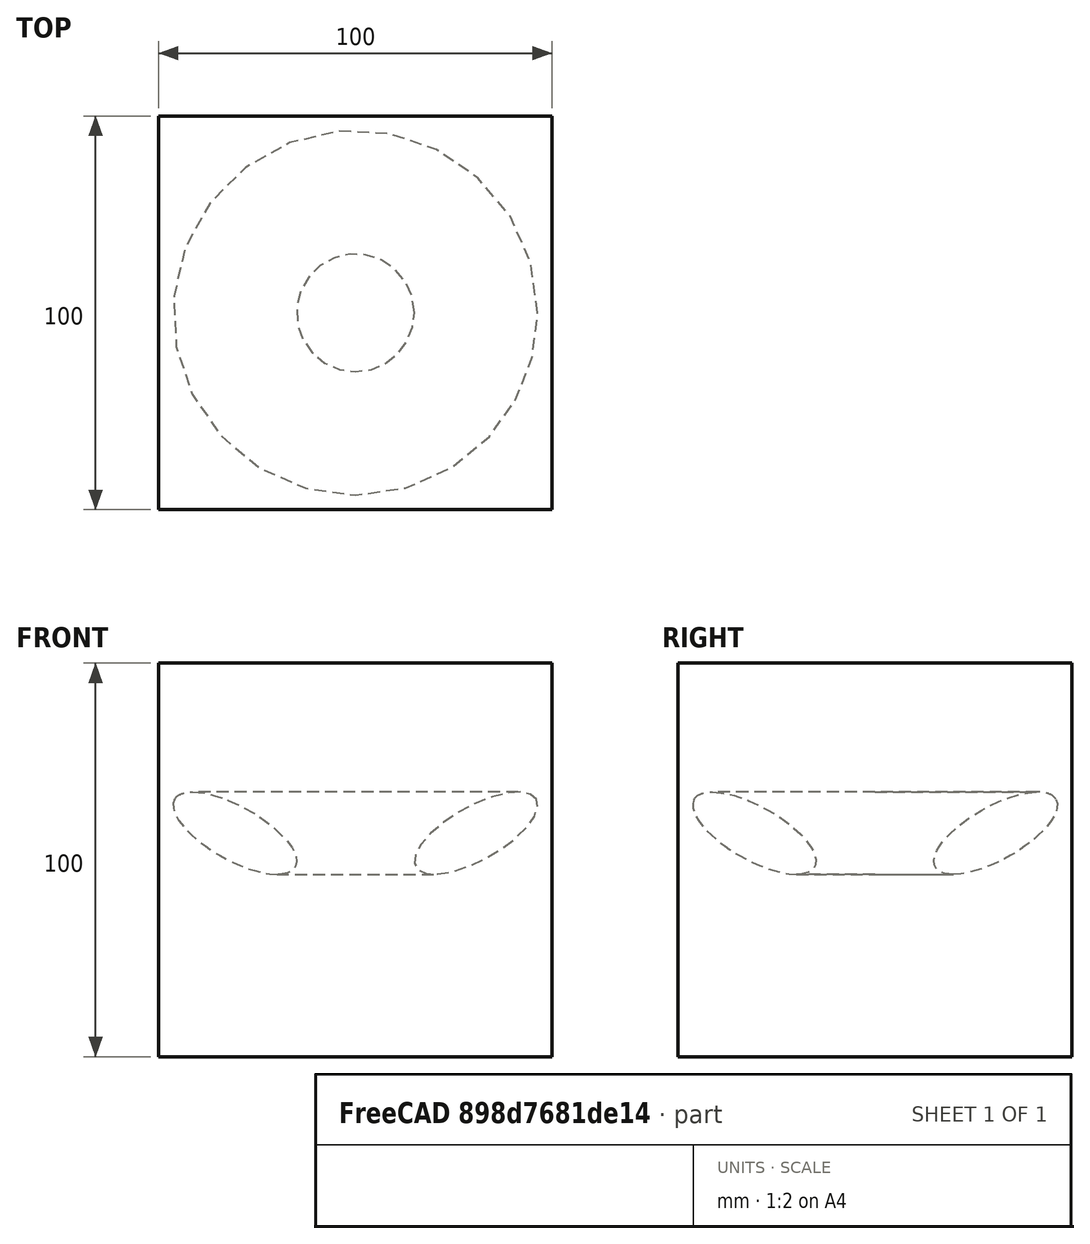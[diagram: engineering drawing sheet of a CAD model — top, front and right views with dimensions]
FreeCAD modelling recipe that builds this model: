
FCSTD DOCUMENT  (FreeCAD 1.0R39109 (Git))
Label: revolveSingleEdge
License: All rights reserved
LicenseURL: http://en.wikipedia.org/wiki/All_rights_reserved
objects: App::DocumentObjectGroupPython×1248, App::Part×2, Part::FeaturePython×1, Sketcher::SketchObject×1, Part::Revolution×1
note: 4 computed .brp shape members not serialized (recipe doc carries the construction recipe); baked Part::Feature solids carry a one-line shape summary decoded from their .brp

FEATURE [App::DocumentObjectGroupPython] HALFPI  # scripted group (container) (typed FeaturePython)
  name = HALFPI
  value = pi/2.
FEATURE [App::DocumentObjectGroupPython] PI  # scripted group (container) (typed FeaturePython)
  name = PI
  value = 1.*pi
FEATURE [App::DocumentObjectGroupPython] TWOPI  # scripted group (container) (typed FeaturePython)
  name = TWOPI
  value = 2.*pi
FEATURE [App::DocumentObjectGroupPython] Constants  # scripted group (container) (typed FeaturePython)
  Group = -> [HALFPI,PI,TWOPI]
FEATURE [App::DocumentObjectGroupPython] Variables  # scripted group (container) (typed FeaturePython)
FEATURE [App::DocumentObjectGroupPython] Quantities  # scripted group (container) (typed FeaturePython)
FEATURE [App::DocumentObjectGroupPython] Isotopes  # scripted group (container) (typed FeaturePython)
FEATURE [App::DocumentObjectGroupPython] Elements  # scripted group (container) (typed FeaturePython)
FEATURE [App::DocumentObjectGroupPython] G4Isotopes  # scripted group (container) (typed FeaturePython)
FEATURE [App::DocumentObjectGroupPython] H_element  # scripted group (container) (typed FeaturePython)
  Z = 1
  atom_value = 1.008
  formula = H
  name = H_element
FEATURE [App::DocumentObjectGroupPython] He_element  # scripted group (container) (typed FeaturePython)
  Z = 2
  atom_value = 4.0026
  formula = He
  name = He_element
FEATURE [App::DocumentObjectGroupPython] Li_element  # scripted group (container) (typed FeaturePython)
  Z = 3
  atom_value = 6.94
  formula = Li
  name = Li_element
FEATURE [App::DocumentObjectGroupPython] Be_element  # scripted group (container) (typed FeaturePython)
  Z = 4
  atom_value = 9.01218
  formula = Be
  name = Be_element
FEATURE [App::DocumentObjectGroupPython] B_element  # scripted group (container) (typed FeaturePython)
  Z = 5
  atom_value = 10.81
  formula = B
  name = B_element
FEATURE [App::DocumentObjectGroupPython] C_element  # scripted group (container) (typed FeaturePython)
  Z = 6
  atom_value = 12.011
  formula = C
  name = C_element
FEATURE [App::DocumentObjectGroupPython] N_element  # scripted group (container) (typed FeaturePython)
  Z = 7
  atom_value = 14.007
  formula = N
  name = N_element
FEATURE [App::DocumentObjectGroupPython] O_element  # scripted group (container) (typed FeaturePython)
  Z = 8
  atom_value = 15.999
  formula = O
  name = O_element
FEATURE [App::DocumentObjectGroupPython] F_element  # scripted group (container) (typed FeaturePython)
  Z = 9
  atom_value = 18.9984
  formula = F
  name = F_element
FEATURE [App::DocumentObjectGroupPython] Ne_element  # scripted group (container) (typed FeaturePython)
  Z = 10
  atom_value = 20.1797
  formula = Ne
  name = Ne_element
FEATURE [App::DocumentObjectGroupPython] Na_element  # scripted group (container) (typed FeaturePython)
  Z = 11
  atom_value = 22.9898
  formula = Na
  name = Na_element
FEATURE [App::DocumentObjectGroupPython] Mg_element  # scripted group (container) (typed FeaturePython)
  Z = 12
  atom_value = 24.305
  formula = Mg
  name = Mg_element
FEATURE [App::DocumentObjectGroupPython] Al_element  # scripted group (container) (typed FeaturePython)
  Z = 13
  atom_value = 26.9815
  formula = Al
  name = Al_element
FEATURE [App::DocumentObjectGroupPython] Si_element  # scripted group (container) (typed FeaturePython)
  Z = 14
  atom_value = 28.085
  formula = Si
  name = Si_element
FEATURE [App::DocumentObjectGroupPython] P_element  # scripted group (container) (typed FeaturePython)
  Z = 15
  atom_value = 30.9738
  formula = P
  name = P_element
FEATURE [App::DocumentObjectGroupPython] S_element  # scripted group (container) (typed FeaturePython)
  Z = 16
  atom_value = 32.06
  formula = S
  name = S_element
FEATURE [App::DocumentObjectGroupPython] Cl_element  # scripted group (container) (typed FeaturePython)
  Z = 17
  atom_value = 35.45
  formula = Cl
  name = Cl_element
FEATURE [App::DocumentObjectGroupPython] Ar_element  # scripted group (container) (typed FeaturePython)
  Z = 18
  atom_value = 39.95
  formula = Ar
  name = Ar_element
FEATURE [App::DocumentObjectGroupPython] K_element  # scripted group (container) (typed FeaturePython)
  Z = 19
  atom_value = 39.0983
  formula = K
  name = K_element
FEATURE [App::DocumentObjectGroupPython] Ca_element  # scripted group (container) (typed FeaturePython)
  Z = 20
  atom_value = 40.078
  formula = Ca
  name = Ca_element
FEATURE [App::DocumentObjectGroupPython] Sc_element  # scripted group (container) (typed FeaturePython)
  Z = 21
  atom_value = 44.9559
  formula = Sc
  name = Sc_element
FEATURE [App::DocumentObjectGroupPython] Ti_element  # scripted group (container) (typed FeaturePython)
  Z = 22
  atom_value = 47.867
  formula = Ti
  name = Ti_element
FEATURE [App::DocumentObjectGroupPython] V_element  # scripted group (container) (typed FeaturePython)
  Z = 23
  atom_value = 50.9415
  formula = V
  name = V_element
FEATURE [App::DocumentObjectGroupPython] Cr_element  # scripted group (container) (typed FeaturePython)
  Z = 24
  atom_value = 51.9961
  formula = Cr
  name = Cr_element
FEATURE [App::DocumentObjectGroupPython] Mn_element  # scripted group (container) (typed FeaturePython)
  Z = 25
  atom_value = 54.938
  formula = Mn
  name = Mn_element
FEATURE [App::DocumentObjectGroupPython] Fe_element  # scripted group (container) (typed FeaturePython)
  Z = 26
  atom_value = 55.845
  formula = Fe
  name = Fe_element
FEATURE [App::DocumentObjectGroupPython] Co_element  # scripted group (container) (typed FeaturePython)
  Z = 27
  atom_value = 58.9332
  formula = Co
  name = Co_element
FEATURE [App::DocumentObjectGroupPython] Ni_element  # scripted group (container) (typed FeaturePython)
  Z = 28
  atom_value = 58.6934
  formula = Ni
  name = Ni_element
FEATURE [App::DocumentObjectGroupPython] Cu_element  # scripted group (container) (typed FeaturePython)
  Z = 29
  atom_value = 63.546
  formula = Cu
  name = Cu_element
FEATURE [App::DocumentObjectGroupPython] Zn_element  # scripted group (container) (typed FeaturePython)
  Z = 30
  atom_value = 65.38
  formula = Zn
  name = Zn_element
FEATURE [App::DocumentObjectGroupPython] Ga_element  # scripted group (container) (typed FeaturePython)
  Z = 31
  atom_value = 69.723
  formula = Ga
  name = Ga_element
FEATURE [App::DocumentObjectGroupPython] Ge_element  # scripted group (container) (typed FeaturePython)
  Z = 32
  atom_value = 72.63
  formula = Ge
  name = Ge_element
FEATURE [App::DocumentObjectGroupPython] As_element  # scripted group (container) (typed FeaturePython)
  Z = 33
  atom_value = 74.9216
  formula = As
  name = As_element
FEATURE [App::DocumentObjectGroupPython] Se_element  # scripted group (container) (typed FeaturePython)
  Z = 34
  atom_value = 78.971
  formula = Se
  name = Se_element
FEATURE [App::DocumentObjectGroupPython] Br_element  # scripted group (container) (typed FeaturePython)
  Z = 35
  atom_value = 79.904
  formula = Br
  name = Br_element
FEATURE [App::DocumentObjectGroupPython] Kr_element  # scripted group (container) (typed FeaturePython)
  Z = 36
  atom_value = 83.798
  formula = Kr
  name = Kr_element
FEATURE [App::DocumentObjectGroupPython] Rb_element  # scripted group (container) (typed FeaturePython)
  Z = 37
  atom_value = 85.4678
  formula = Rb
  name = Rb_element
FEATURE [App::DocumentObjectGroupPython] Sr_element  # scripted group (container) (typed FeaturePython)
  Z = 38
  atom_value = 87.62
  formula = Sr
  name = Sr_element
FEATURE [App::DocumentObjectGroupPython] Y_element  # scripted group (container) (typed FeaturePython)
  Z = 39
  atom_value = 88.9058
  formula = Y
  name = Y_element
FEATURE [App::DocumentObjectGroupPython] Zr_element  # scripted group (container) (typed FeaturePython)
  Z = 40
  atom_value = 91.224
  formula = Zr
  name = Zr_element
FEATURE [App::DocumentObjectGroupPython] Nb_element  # scripted group (container) (typed FeaturePython)
  Z = 41
  atom_value = 92.9064
  formula = Nb
  name = Nb_element
FEATURE [App::DocumentObjectGroupPython] Mo_element  # scripted group (container) (typed FeaturePython)
  Z = 42
  atom_value = 95.95
  formula = Mo
  name = Mo_element
FEATURE [App::DocumentObjectGroupPython] Tc_element  # scripted group (container) (typed FeaturePython)
  Z = 43
  atom_value = 97
  formula = Tc
  name = Tc_element
FEATURE [App::DocumentObjectGroupPython] Ru_element  # scripted group (container) (typed FeaturePython)
  Z = 44
  atom_value = 101.07
  formula = Ru
  name = Ru_element
FEATURE [App::DocumentObjectGroupPython] Rh_element  # scripted group (container) (typed FeaturePython)
  Z = 45
  atom_value = 102.905
  formula = Rh
  name = Rh_element
FEATURE [App::DocumentObjectGroupPython] Pd_element  # scripted group (container) (typed FeaturePython)
  Z = 46
  atom_value = 106.42
  formula = Pd
  name = Pd_element
FEATURE [App::DocumentObjectGroupPython] Ag_element  # scripted group (container) (typed FeaturePython)
  Z = 47
  atom_value = 107.868
  formula = Ag
  name = Ag_element
FEATURE [App::DocumentObjectGroupPython] Cd_element  # scripted group (container) (typed FeaturePython)
  Z = 48
  atom_value = 112.414
  formula = Cd
  name = Cd_element
FEATURE [App::DocumentObjectGroupPython] In_element  # scripted group (container) (typed FeaturePython)
  Z = 49
  atom_value = 114.818
  formula = In
  name = In_element
FEATURE [App::DocumentObjectGroupPython] Sn_element  # scripted group (container) (typed FeaturePython)
  Z = 50
  atom_value = 118.71
  formula = Sn
  name = Sn_element
FEATURE [App::DocumentObjectGroupPython] Sb_element  # scripted group (container) (typed FeaturePython)
  Z = 51
  atom_value = 121.76
  formula = Sb
  name = Sb_element
FEATURE [App::DocumentObjectGroupPython] Te_element  # scripted group (container) (typed FeaturePython)
  Z = 52
  atom_value = 127.6
  formula = Te
  name = Te_element
FEATURE [App::DocumentObjectGroupPython] I_element  # scripted group (container) (typed FeaturePython)
  Z = 53
  atom_value = 126.904
  formula = I
  name = I_element
FEATURE [App::DocumentObjectGroupPython] Xe_element  # scripted group (container) (typed FeaturePython)
  Z = 54
  atom_value = 131.293
  formula = Xe
  name = Xe_element
FEATURE [App::DocumentObjectGroupPython] Cs_element  # scripted group (container) (typed FeaturePython)
  Z = 55
  atom_value = 132.905
  formula = Cs
  name = Cs_element
FEATURE [App::DocumentObjectGroupPython] Ba_element  # scripted group (container) (typed FeaturePython)
  Z = 56
  atom_value = 137.327
  formula = Ba
  name = Ba_element
FEATURE [App::DocumentObjectGroupPython] La_element  # scripted group (container) (typed FeaturePython)
  Z = 57
  atom_value = 138.905
  formula = La
  name = La_element
FEATURE [App::DocumentObjectGroupPython] Ce_element  # scripted group (container) (typed FeaturePython)
  Z = 58
  atom_value = 140.116
  formula = Ce
  name = Ce_element
FEATURE [App::DocumentObjectGroupPython] Pr_element  # scripted group (container) (typed FeaturePython)
  Z = 59
  atom_value = 140.908
  formula = Pr
  name = Pr_element
FEATURE [App::DocumentObjectGroupPython] Nd_element  # scripted group (container) (typed FeaturePython)
  Z = 60
  atom_value = 144.242
  formula = Nd
  name = Nd_element
FEATURE [App::DocumentObjectGroupPython] Pm_element  # scripted group (container) (typed FeaturePython)
  Z = 61
  atom_value = 145
  formula = Pm
  name = Pm_element
FEATURE [App::DocumentObjectGroupPython] Sm_element  # scripted group (container) (typed FeaturePython)
  Z = 62
  atom_value = 150.36
  formula = Sm
  name = Sm_element
FEATURE [App::DocumentObjectGroupPython] Eu_element  # scripted group (container) (typed FeaturePython)
  Z = 63
  atom_value = 151.964
  formula = Eu
  name = Eu_element
FEATURE [App::DocumentObjectGroupPython] Gd_element  # scripted group (container) (typed FeaturePython)
  Z = 64
  atom_value = 157.25
  formula = Gd
  name = Gd_element
FEATURE [App::DocumentObjectGroupPython] Tb_element  # scripted group (container) (typed FeaturePython)
  Z = 65
  atom_value = 158.925
  formula = Tb
  name = Tb_element
FEATURE [App::DocumentObjectGroupPython] Dy_element  # scripted group (container) (typed FeaturePython)
  Z = 66
  atom_value = 162.5
  formula = Dy
  name = Dy_element
FEATURE [App::DocumentObjectGroupPython] Ho_element  # scripted group (container) (typed FeaturePython)
  Z = 67
  atom_value = 164.93
  formula = Ho
  name = Ho_element
FEATURE [App::DocumentObjectGroupPython] Er_element  # scripted group (container) (typed FeaturePython)
  Z = 68
  atom_value = 167.259
  formula = Er
  name = Er_element
FEATURE [App::DocumentObjectGroupPython] Tm_element  # scripted group (container) (typed FeaturePython)
  Z = 69
  atom_value = 168.934
  formula = Tm
  name = Tm_element
FEATURE [App::DocumentObjectGroupPython] Yb_element  # scripted group (container) (typed FeaturePython)
  Z = 70
  atom_value = 173.045
  formula = Yb
  name = Yb_element
FEATURE [App::DocumentObjectGroupPython] Lu_element  # scripted group (container) (typed FeaturePython)
  Z = 71
  atom_value = 174.967
  formula = Lu
  name = Lu_element
FEATURE [App::DocumentObjectGroupPython] Hf_element  # scripted group (container) (typed FeaturePython)
  Z = 72
  atom_value = 178.49
  formula = Hf
  name = Hf_element
FEATURE [App::DocumentObjectGroupPython] Ta_element  # scripted group (container) (typed FeaturePython)
  Z = 73
  atom_value = 180.948
  formula = Ta
  name = Ta_element
FEATURE [App::DocumentObjectGroupPython] W_element  # scripted group (container) (typed FeaturePython)
  Z = 74
  atom_value = 183.84
  formula = W
  name = W_element
FEATURE [App::DocumentObjectGroupPython] Re_element  # scripted group (container) (typed FeaturePython)
  Z = 75
  atom_value = 186.207
  formula = Re
  name = Re_element
FEATURE [App::DocumentObjectGroupPython] Os_element  # scripted group (container) (typed FeaturePython)
  Z = 76
  atom_value = 190.23
  formula = Os
  name = Os_element
FEATURE [App::DocumentObjectGroupPython] Ir_element  # scripted group (container) (typed FeaturePython)
  Z = 77
  atom_value = 192.217
  formula = Ir
  name = Ir_element
FEATURE [App::DocumentObjectGroupPython] Pt_element  # scripted group (container) (typed FeaturePython)
  Z = 78
  atom_value = 195.084
  formula = Pt
  name = Pt_element
FEATURE [App::DocumentObjectGroupPython] Au_element  # scripted group (container) (typed FeaturePython)
  Z = 79
  atom_value = 196.967
  formula = Au
  name = Au_element
FEATURE [App::DocumentObjectGroupPython] Hg_element  # scripted group (container) (typed FeaturePython)
  Z = 80
  atom_value = 200.592
  formula = Hg
  name = Hg_element
FEATURE [App::DocumentObjectGroupPython] Tl_element  # scripted group (container) (typed FeaturePython)
  Z = 81
  atom_value = 204.38
  formula = Tl
  name = Tl_element
FEATURE [App::DocumentObjectGroupPython] Pb_element  # scripted group (container) (typed FeaturePython)
  Z = 82
  atom_value = 207.2
  formula = Pb
  name = Pb_element
FEATURE [App::DocumentObjectGroupPython] Bi_element  # scripted group (container) (typed FeaturePython)
  Z = 83
  atom_value = 208.98
  formula = Bi
  name = Bi_element
FEATURE [App::DocumentObjectGroupPython] Po_element  # scripted group (container) (typed FeaturePython)
  Z = 84
  atom_value = 209
  formula = Po
  name = Po_element
FEATURE [App::DocumentObjectGroupPython] At_element  # scripted group (container) (typed FeaturePython)
  Z = 85
  atom_value = 210
  formula = At
  name = At_element
FEATURE [App::DocumentObjectGroupPython] Rn_element  # scripted group (container) (typed FeaturePython)
  Z = 86
  atom_value = 222
  formula = Rn
  name = Rn_element
FEATURE [App::DocumentObjectGroupPython] Fr_element  # scripted group (container) (typed FeaturePython)
  Z = 87
  atom_value = 223
  formula = Fr
  name = Fr_element
FEATURE [App::DocumentObjectGroupPython] Ra_element  # scripted group (container) (typed FeaturePython)
  Z = 88
  atom_value = 226
  formula = Ra
  name = Ra_element
FEATURE [App::DocumentObjectGroupPython] Ac_element  # scripted group (container) (typed FeaturePython)
  Z = 89
  atom_value = 227
  formula = Ac
  name = Ac_element
FEATURE [App::DocumentObjectGroupPython] Th_element  # scripted group (container) (typed FeaturePython)
  Z = 90
  atom_value = 232.038
  formula = Th
  name = Th_element
FEATURE [App::DocumentObjectGroupPython] Pa_element  # scripted group (container) (typed FeaturePython)
  Z = 91
  atom_value = 231.036
  formula = Pa
  name = Pa_element
FEATURE [App::DocumentObjectGroupPython] U_element  # scripted group (container) (typed FeaturePython)
  Z = 92
  atom_value = 238.029
  formula = U
  name = U_element
FEATURE [App::DocumentObjectGroupPython] Np_element  # scripted group (container) (typed FeaturePython)
  Z = 93
  atom_value = 237
  formula = Np
  name = Np_element
FEATURE [App::DocumentObjectGroupPython] Pu_element  # scripted group (container) (typed FeaturePython)
  Z = 94
  atom_value = 244
  formula = Pu
  name = Pu_element
FEATURE [App::DocumentObjectGroupPython] Am_element  # scripted group (container) (typed FeaturePython)
  Z = 95
  atom_value = 243
  formula = Am
  name = Am_element
FEATURE [App::DocumentObjectGroupPython] Cm_element  # scripted group (container) (typed FeaturePython)
  Z = 96
  atom_value = 247
  formula = Cm
  name = Cm_element
FEATURE [App::DocumentObjectGroupPython] Bk_element  # scripted group (container) (typed FeaturePython)
  Z = 97
  atom_value = 247
  formula = Bk
  name = Bk_element
FEATURE [App::DocumentObjectGroupPython] Cf_element  # scripted group (container) (typed FeaturePython)
  Z = 98
  atom_value = 251
  formula = Cf
  name = Cf_element
FEATURE [App::DocumentObjectGroupPython] G4Elements  # scripted group (container) (typed FeaturePython)
  Group = -> [H_element,He_element,Li_element,Be_element,B_element,C_element,N_element,O_element,F_element,Ne_element,Na_element,Mg_element,Al_element,Si_element,P_element,S_element,Cl_element,Ar_element,K_element,Ca_element,Sc_element,Ti_element,V_element,Cr_element,Mn_element,Fe_element,Co_element,Ni_element,Cu_element,Zn_element,Ga_element,Ge_element,As_element,Se_element,Br_element,Kr_element,Rb_element,+61 more]
FEATURE [App::DocumentObjectGroupPython] H_element001  label="H_element : 0.101"  # scripted group (container) (typed FeaturePython)
  n = 0.101327
FEATURE [App::DocumentObjectGroupPython] C_element001  label="C_element : 0.775"  # scripted group (container) (typed FeaturePython)
  n = 0.7755
FEATURE [App::DocumentObjectGroupPython] N_element001  label="N_element : 0.035"  # scripted group (container) (typed FeaturePython)
  n = 0.035057
FEATURE [App::DocumentObjectGroupPython] O_element001  label="O_element : 0.052"  # scripted group (container) (typed FeaturePython)
  n = 0.0523159
FEATURE [App::DocumentObjectGroupPython] F_element001  label="F_element : 0.017"  # scripted group (container) (typed FeaturePython)
  n = 0.017422
FEATURE [App::DocumentObjectGroupPython] Ca_element001  label="Ca_element : 0.018"  # scripted group (container) (typed FeaturePython)
  n = 0.018378
FEATURE [App::DocumentObjectGroupPython] G4_A_150_TISSUE  label="G4_A-150_TISSUE"  # scripted group (container) (typed FeaturePython)
  Dunit = g/cm3
  Dvalue = 1.127
  Group = -> [H_element001,C_element001,N_element001,O_element001,F_element001,Ca_element001]
  conduct = 2
  density = 1
  expand = 3
  formula = G4_A-150_TISSUE
  name = G4_A-150_TISSUE
  specific = 4
FEATURE [App::DocumentObjectGroupPython] C_element002  label="C_element : 3"  # scripted group (container) (typed FeaturePython)
  n = 3
  ref = C_element
FEATURE [App::DocumentObjectGroupPython] H_element002  label="H_element : 6"  # scripted group (container) (typed FeaturePython)
  n = 6
  ref = H_element
FEATURE [App::DocumentObjectGroupPython] O_element002  label="O_element : 1"  # scripted group (container) (typed FeaturePython)
  n = 1
  ref = O_element
FEATURE [App::DocumentObjectGroupPython] G4_ACETONE  # scripted group (container) (typed FeaturePython)
  Dunit = g/cm3
  Dvalue = 0.7899
  Group = -> [C_element002,H_element002,O_element002]
  conduct = 2
  density = 1
  expand = 3
  formula = G4_ACETONE
  name = G4_ACETONE
  specific = 4
FEATURE [App::DocumentObjectGroupPython] C_element003  label="C_element : 2"  # scripted group (container) (typed FeaturePython)
  n = 2
  ref = C_element
FEATURE [App::DocumentObjectGroupPython] H_element003  label="H_element : 2"  # scripted group (container) (typed FeaturePython)
  n = 2
  ref = H_element
FEATURE [App::DocumentObjectGroupPython] G4_ACETYLENE  # scripted group (container) (typed FeaturePython)
  Dunit = g/cm3
  Dvalue = 0.0010967
  Group = -> [C_element003,H_element003]
  conduct = 2
  density = 1
  expand = 3
  formula = G4_ACETYLENE
  name = G4_ACETYLENE
  specific = 4
FEATURE [App::DocumentObjectGroupPython] C_element004  label="C_element : 5"  # scripted group (container) (typed FeaturePython)
  n = 5
  ref = C_element
FEATURE [App::DocumentObjectGroupPython] H_element004  label="H_element : 5"  # scripted group (container) (typed FeaturePython)
  n = 5
  ref = H_element
FEATURE [App::DocumentObjectGroupPython] N_element002  label="N_element : 5"  # scripted group (container) (typed FeaturePython)
  n = 5
  ref = N_element
FEATURE [App::DocumentObjectGroupPython] G4_ADENINE  # scripted group (container) (typed FeaturePython)
  Dunit = g/cm3
  Dvalue = 1.6
  Group = -> [C_element004,H_element004,N_element002]
  conduct = 2
  density = 1
  expand = 3
  formula = G4_ADENINE
  name = G4_ADENINE
  specific = 4
FEATURE [App::DocumentObjectGroupPython] H_element005  label="H_element : 0.114"  # scripted group (container) (typed FeaturePython)
  n = 0.114
FEATURE [App::DocumentObjectGroupPython] C_element005  label="C_element : 0.598"  # scripted group (container) (typed FeaturePython)
  n = 0.598
FEATURE [App::DocumentObjectGroupPython] N_element003  label="N_element : 0.007"  # scripted group (container) (typed FeaturePython)
  n = 0.007
FEATURE [App::DocumentObjectGroupPython] O_element003  label="O_element : 0.278"  # scripted group (container) (typed FeaturePython)
  n = 0.278
FEATURE [App::DocumentObjectGroupPython] Na_element001  label="Na_element : 0.001"  # scripted group (container) (typed FeaturePython)
  n = 0.001
FEATURE [App::DocumentObjectGroupPython] S_element001  label="S_element : 0.001"  # scripted group (container) (typed FeaturePython)
  n = 0.001
FEATURE [App::DocumentObjectGroupPython] Cl_element001  label="Cl_element : 0.001"  # scripted group (container) (typed FeaturePython)
  n = 0.001
FEATURE [App::DocumentObjectGroupPython] G4_ADIPOSE_TISSUE_ICRP  # scripted group (container) (typed FeaturePython)
  Dunit = g/cm3
  Dvalue = 0.95
  Group = -> [H_element005,C_element005,N_element003,O_element003,Na_element001,S_element001,Cl_element001]
  conduct = 2
  density = 1
  expand = 3
  formula = G4_ADIPOSE_TISSUE_ICRP
  name = G4_ADIPOSE_TISSUE_ICRP
  specific = 4
FEATURE [App::DocumentObjectGroupPython] C_element006  label="C_element : 0.000"  # scripted group (container) (typed FeaturePython)
  n = 0.000124
FEATURE [App::DocumentObjectGroupPython] N_element004  label="N_element : 0.755"  # scripted group (container) (typed FeaturePython)
  n = 0.755268
FEATURE [App::DocumentObjectGroupPython] O_element004  label="O_element : 0.232"  # scripted group (container) (typed FeaturePython)
  n = 0.231781
FEATURE [App::DocumentObjectGroupPython] Ar_element001  label="Ar_element : 0.013"  # scripted group (container) (typed FeaturePython)
  n = 0.012827
FEATURE [App::DocumentObjectGroupPython] G4_AIR  # scripted group (container) (typed FeaturePython)
  Dunit = g/cm3
  Dvalue = 0.00120479
  Group = -> [C_element006,N_element004,O_element004,Ar_element001]
  conduct = 2
  density = 1
  expand = 3
  formula = G4_AIR
  name = G4_AIR
  specific = 4
FEATURE [App::DocumentObjectGroupPython] C_element007  label="C_element : 006"  # scripted group (container) (typed FeaturePython)
  n = 3
  ref = C_element
FEATURE [App::DocumentObjectGroupPython] H_element006  label="H_element : 7"  # scripted group (container) (typed FeaturePython)
  n = 7
  ref = H_element
FEATURE [App::DocumentObjectGroupPython] N_element005  label="N_element : 1"  # scripted group (container) (typed FeaturePython)
  n = 1
  ref = N_element
FEATURE [App::DocumentObjectGroupPython] O_element005  label="O_element : 2"  # scripted group (container) (typed FeaturePython)
  n = 2
  ref = O_element
FEATURE [App::DocumentObjectGroupPython] G4_ALANINE  # scripted group (container) (typed FeaturePython)
  Dunit = g/cm3
  Dvalue = 1.42
  Group = -> [C_element007,H_element006,N_element005,O_element005]
  conduct = 2
  density = 1
  expand = 3
  formula = G4_ALANINE
  name = G4_ALANINE
  specific = 4
FEATURE [App::DocumentObjectGroupPython] Al_element001  label="Al_element : 2"  # scripted group (container) (typed FeaturePython)
  n = 2
  ref = Al_element
FEATURE [App::DocumentObjectGroupPython] O_element006  label="O_element : 3"  # scripted group (container) (typed FeaturePython)
  n = 3
  ref = O_element
FEATURE [App::DocumentObjectGroupPython] G4_ALUMINUM_OXIDE  # scripted group (container) (typed FeaturePython)
  Dunit = g/cm3
  Dvalue = 3.97
  Group = -> [Al_element001,O_element006]
  conduct = 2
  density = 1
  expand = 3
  formula = G4_ALUMINUM_OXIDE
  name = G4_ALUMINUM_OXIDE
  specific = 4
FEATURE [App::DocumentObjectGroupPython] H_element007  label="H_element : 0.106"  # scripted group (container) (typed FeaturePython)
  n = 0.10593
FEATURE [App::DocumentObjectGroupPython] C_element008  label="C_element : 0.789"  # scripted group (container) (typed FeaturePython)
  n = 0.788974
FEATURE [App::DocumentObjectGroupPython] O_element007  label="O_element : 0.105"  # scripted group (container) (typed FeaturePython)
  n = 0.105096
FEATURE [App::DocumentObjectGroupPython] G4_AMBER  # scripted group (container) (typed FeaturePython)
  Dunit = g/cm3
  Dvalue = 1.1
  Group = -> [H_element007,C_element008,O_element007]
  conduct = 2
  density = 1
  expand = 3
  formula = G4_AMBER
  name = G4_AMBER
  specific = 4
FEATURE [App::DocumentObjectGroupPython] N_element006  label="N_element : 006"  # scripted group (container) (typed FeaturePython)
  n = 1
  ref = N_element
FEATURE [App::DocumentObjectGroupPython] H_element008  label="H_element : 3"  # scripted group (container) (typed FeaturePython)
  n = 3
  ref = H_element
FEATURE [App::DocumentObjectGroupPython] G4_AMMONIA  # scripted group (container) (typed FeaturePython)
  Dunit = g/cm3
  Dvalue = 0.000826019
  Group = -> [N_element006,H_element008]
  conduct = 2
  density = 1
  expand = 3
  formula = G4_AMMONIA
  name = G4_AMMONIA
  specific = 4
FEATURE [App::DocumentObjectGroupPython] C_element009  label="C_element : 6"  # scripted group (container) (typed FeaturePython)
  n = 6
  ref = C_element
FEATURE [App::DocumentObjectGroupPython] H_element009  label="H_element : 008"  # scripted group (container) (typed FeaturePython)
  n = 7
  ref = H_element
FEATURE [App::DocumentObjectGroupPython] N_element007  label="N_element : 007"  # scripted group (container) (typed FeaturePython)
  n = 1
  ref = N_element
FEATURE [App::DocumentObjectGroupPython] G4_ANILINE  # scripted group (container) (typed FeaturePython)
  Dunit = g/cm3
  Dvalue = 1.0235
  Group = -> [C_element009,H_element009,N_element007]
  conduct = 2
  density = 1
  expand = 3
  formula = G4_ANILINE
  name = G4_ANILINE
  specific = 4
FEATURE [App::DocumentObjectGroupPython] C_element010  label="C_element : 14"  # scripted group (container) (typed FeaturePython)
  n = 14
  ref = C_element
FEATURE [App::DocumentObjectGroupPython] H_element010  label="H_element : 10"  # scripted group (container) (typed FeaturePython)
  n = 10
  ref = H_element
FEATURE [App::DocumentObjectGroupPython] G4_ANTHRACENE  # scripted group (container) (typed FeaturePython)
  Dunit = g/cm3
  Dvalue = 1.283
  Group = -> [C_element010,H_element010]
  conduct = 2
  density = 1
  expand = 3
  formula = G4_ANTHRACENE
  name = G4_ANTHRACENE
  specific = 4
FEATURE [App::DocumentObjectGroupPython] H_element011  label="H_element : 0.065"  # scripted group (container) (typed FeaturePython)
  n = 0.0654709
FEATURE [App::DocumentObjectGroupPython] C_element011  label="C_element : 0.537"  # scripted group (container) (typed FeaturePython)
  n = 0.536944
FEATURE [App::DocumentObjectGroupPython] N_element008  label="N_element : 0.021"  # scripted group (container) (typed FeaturePython)
  n = 0.0215
FEATURE [App::DocumentObjectGroupPython] O_element008  label="O_element : 0.032"  # scripted group (container) (typed FeaturePython)
  n = 0.032085
FEATURE [App::DocumentObjectGroupPython] F_element002  label="F_element : 0.167"  # scripted group (container) (typed FeaturePython)
  n = 0.167411
FEATURE [App::DocumentObjectGroupPython] Ca_element002  label="Ca_element : 0.177"  # scripted group (container) (typed FeaturePython)
  n = 0.176589
FEATURE [App::DocumentObjectGroupPython] G4_B_100_BONE  label="G4_B-100_BONE"  # scripted group (container) (typed FeaturePython)
  Dunit = g/cm3
  Dvalue = 1.45
  Group = -> [H_element011,C_element011,N_element008,O_element008,F_element002,Ca_element002]
  conduct = 2
  density = 1
  expand = 3
  formula = G4_B-100_BONE
  name = G4_B-100_BONE
  specific = 4
FEATURE [App::DocumentObjectGroupPython] H_element012  label="H_element : 0.057"  # scripted group (container) (typed FeaturePython)
  n = 0.057441
FEATURE [App::DocumentObjectGroupPython] C_element012  label="C_element : 0.790"  # scripted group (container) (typed FeaturePython)
  n = 0.774591
FEATURE [App::DocumentObjectGroupPython] O_element009  label="O_element : 0.168"  # scripted group (container) (typed FeaturePython)
  n = 0.167968
FEATURE [App::DocumentObjectGroupPython] G4_BAKELITE  # scripted group (container) (typed FeaturePython)
  Dunit = g/cm3
  Dvalue = 1.25
  Group = -> [H_element012,C_element012,O_element009]
  conduct = 2
  density = 1
  expand = 3
  formula = G4_BAKELITE
  name = G4_BAKELITE
  specific = 4
FEATURE [App::DocumentObjectGroupPython] Ba_element001  label="Ba_element : 1"  # scripted group (container) (typed FeaturePython)
  n = 1
  ref = Ba_element
FEATURE [App::DocumentObjectGroupPython] F_element003  label="F_element : 2"  # scripted group (container) (typed FeaturePython)
  n = 2
  ref = F_element
FEATURE [App::DocumentObjectGroupPython] G4_BARIUM_FLUORIDE  # scripted group (container) (typed FeaturePython)
  Dunit = g/cm3
  Dvalue = 4.89
  Group = -> [Ba_element001,F_element003]
  conduct = 2
  density = 1
  expand = 3
  formula = G4_BARIUM_FLUORIDE
  name = G4_BARIUM_FLUORIDE
  specific = 4
FEATURE [App::DocumentObjectGroupPython] Ba_element002  label="Ba_element : 002"  # scripted group (container) (typed FeaturePython)
  n = 1
  ref = Ba_element
FEATURE [App::DocumentObjectGroupPython] S_element002  label="S_element : 1"  # scripted group (container) (typed FeaturePython)
  n = 1
  ref = S_element
FEATURE [App::DocumentObjectGroupPython] O_element010  label="O_element : 4"  # scripted group (container) (typed FeaturePython)
  n = 4
  ref = O_element
FEATURE [App::DocumentObjectGroupPython] G4_BARIUM_SULFATE  # scripted group (container) (typed FeaturePython)
  Dunit = g/cm3
  Dvalue = 4.5
  Group = -> [Ba_element002,S_element002,O_element010]
  conduct = 2
  density = 1
  expand = 3
  formula = G4_BARIUM_SULFATE
  name = G4_BARIUM_SULFATE
  specific = 4
FEATURE [App::DocumentObjectGroupPython] C_element013  label="C_element : 007"  # scripted group (container) (typed FeaturePython)
  n = 6
  ref = C_element
FEATURE [App::DocumentObjectGroupPython] H_element013  label="H_element : 009"  # scripted group (container) (typed FeaturePython)
  n = 6
  ref = H_element
FEATURE [App::DocumentObjectGroupPython] G4_BENZENE  # scripted group (container) (typed FeaturePython)
  Dunit = g/cm3
  Dvalue = 0.87865
  Group = -> [C_element013,H_element013]
  conduct = 2
  density = 1
  expand = 3
  formula = G4_BENZENE
  name = G4_BENZENE
  specific = 4
FEATURE [App::DocumentObjectGroupPython] Be_element001  label="Be_element : 1"  # scripted group (container) (typed FeaturePython)
  n = 1
  ref = Be_element
FEATURE [App::DocumentObjectGroupPython] O_element011  label="O_element : 005"  # scripted group (container) (typed FeaturePython)
  n = 1
  ref = O_element
FEATURE [App::DocumentObjectGroupPython] G4_BERYLLIUM_OXIDE  # scripted group (container) (typed FeaturePython)
  Dunit = g/cm3
  Dvalue = 3.01
  Group = -> [Be_element001,O_element011]
  conduct = 2
  density = 1
  expand = 3
  formula = G4_BERYLLIUM_OXIDE
  name = G4_BERYLLIUM_OXIDE
  specific = 4
FEATURE [App::DocumentObjectGroupPython] Bi_element001  label="Bi_element : 4"  # scripted group (container) (typed FeaturePython)
  n = 4
  ref = Bi_element
FEATURE [App::DocumentObjectGroupPython] Ge_element001  label="Ge_element : 3"  # scripted group (container) (typed FeaturePython)
  n = 3
  ref = Ge_element
FEATURE [App::DocumentObjectGroupPython] O_element012  label="O_element : 12"  # scripted group (container) (typed FeaturePython)
  n = 12
  ref = O_element
FEATURE [App::DocumentObjectGroupPython] G4_BGO  # scripted group (container) (typed FeaturePython)
  Dunit = g/cm3
  Dvalue = 7.13
  Group = -> [Bi_element001,Ge_element001,O_element012]
  conduct = 2
  density = 1
  expand = 3
  formula = G4_BGO
  name = G4_BGO
  specific = 4
FEATURE [App::DocumentObjectGroupPython] H_element014  label="H_element : 0.102"  # scripted group (container) (typed FeaturePython)
  n = 0.102
FEATURE [App::DocumentObjectGroupPython] C_element014  label="C_element : 0.110"  # scripted group (container) (typed FeaturePython)
  n = 0.11
FEATURE [App::DocumentObjectGroupPython] N_element009  label="N_element : 0.033"  # scripted group (container) (typed FeaturePython)
  n = 0.033
FEATURE [App::DocumentObjectGroupPython] O_element013  label="O_element : 0.745"  # scripted group (container) (typed FeaturePython)
  n = 0.745
FEATURE [App::DocumentObjectGroupPython] Na_element002  label="Na_element : 0.002"  # scripted group (container) (typed FeaturePython)
  n = 0.001
FEATURE [App::DocumentObjectGroupPython] P_element001  label="P_element : 0.001"  # scripted group (container) (typed FeaturePython)
  n = 0.001
FEATURE [App::DocumentObjectGroupPython] S_element003  label="S_element : 0.002"  # scripted group (container) (typed FeaturePython)
  n = 0.002
FEATURE [App::DocumentObjectGroupPython] Cl_element002  label="Cl_element : 0.003"  # scripted group (container) (typed FeaturePython)
  n = 0.003
FEATURE [App::DocumentObjectGroupPython] K_element001  label="K_element : 0.002"  # scripted group (container) (typed FeaturePython)
  n = 0.002
FEATURE [App::DocumentObjectGroupPython] Fe_element001  label="Fe_element : 0.001"  # scripted group (container) (typed FeaturePython)
  n = 0.001
FEATURE [App::DocumentObjectGroupPython] G4_BLOOD_ICRP  # scripted group (container) (typed FeaturePython)
  Dunit = g/cm3
  Dvalue = 1.06
  Group = -> [H_element014,C_element014,N_element009,O_element013,Na_element002,P_element001,S_element003,Cl_element002,K_element001,Fe_element001]
  conduct = 2
  density = 1
  expand = 3
  formula = G4_BLOOD_ICRP
  name = G4_BLOOD_ICRP
  specific = 4
FEATURE [App::DocumentObjectGroupPython] H_element015  label="H_element : 0.064"  # scripted group (container) (typed FeaturePython)
  n = 0.064
FEATURE [App::DocumentObjectGroupPython] C_element015  label="C_element : 0.278"  # scripted group (container) (typed FeaturePython)
  n = 0.278
FEATURE [App::DocumentObjectGroupPython] N_element010  label="N_element : 0.027"  # scripted group (container) (typed FeaturePython)
  n = 0.027
FEATURE [App::DocumentObjectGroupPython] O_element014  label="O_element : 0.410"  # scripted group (container) (typed FeaturePython)
  n = 0.41
FEATURE [App::DocumentObjectGroupPython] Mg_element001  label="Mg_element : 0.002"  # scripted group (container) (typed FeaturePython)
  n = 0.002
FEATURE [App::DocumentObjectGroupPython] P_element002  label="P_element : 0.070"  # scripted group (container) (typed FeaturePython)
  n = 0.07
FEATURE [App::DocumentObjectGroupPython] S_element004  label="S_element : 0.003"  # scripted group (container) (typed FeaturePython)
  n = 0.002
FEATURE [App::DocumentObjectGroupPython] Ca_element003  label="Ca_element : 0.147"  # scripted group (container) (typed FeaturePython)
  n = 0.147
FEATURE [App::DocumentObjectGroupPython] G4_BONE_COMPACT_ICRU  # scripted group (container) (typed FeaturePython)
  Dunit = g/cm3
  Dvalue = 1.85
  Group = -> [H_element015,C_element015,N_element010,O_element014,Mg_element001,P_element002,S_element004,Ca_element003]
  conduct = 2
  density = 1
  expand = 3
  formula = G4_BONE_COMPACT_ICRU
  name = G4_BONE_COMPACT_ICRU
  specific = 4
FEATURE [App::DocumentObjectGroupPython] H_element016  label="H_element : 0.034"  # scripted group (container) (typed FeaturePython)
  n = 0.034
FEATURE [App::DocumentObjectGroupPython] C_element016  label="C_element : 0.155"  # scripted group (container) (typed FeaturePython)
  n = 0.155
FEATURE [App::DocumentObjectGroupPython] N_element011  label="N_element : 0.042"  # scripted group (container) (typed FeaturePython)
  n = 0.042
FEATURE [App::DocumentObjectGroupPython] O_element015  label="O_element : 0.435"  # scripted group (container) (typed FeaturePython)
  n = 0.435
FEATURE [App::DocumentObjectGroupPython] Na_element003  label="Na_element : 0.003"  # scripted group (container) (typed FeaturePython)
  n = 0.001
FEATURE [App::DocumentObjectGroupPython] Mg_element002  label="Mg_element : 0.003"  # scripted group (container) (typed FeaturePython)
  n = 0.002
FEATURE [App::DocumentObjectGroupPython] P_element003  label="P_element : 0.103"  # scripted group (container) (typed FeaturePython)
  n = 0.103
FEATURE [App::DocumentObjectGroupPython] S_element005  label="S_element : 0.004"  # scripted group (container) (typed FeaturePython)
  n = 0.003
FEATURE [App::DocumentObjectGroupPython] Ca_element004  label="Ca_element : 0.225"  # scripted group (container) (typed FeaturePython)
  n = 0.225
FEATURE [App::DocumentObjectGroupPython] G4_BONE_CORTICAL_ICRP  # scripted group (container) (typed FeaturePython)
  Dunit = g/cm3
  Dvalue = 1.92
  Group = -> [H_element016,C_element016,N_element011,O_element015,Na_element003,Mg_element002,P_element003,S_element005,Ca_element004]
  conduct = 2
  density = 1
  expand = 3
  formula = G4_BONE_CORTICAL_ICRP
  name = G4_BONE_CORTICAL_ICRP
  specific = 4
FEATURE [App::DocumentObjectGroupPython] B_element001  label="B_element : 4"  # scripted group (container) (typed FeaturePython)
  n = 4
  ref = B_element
FEATURE [App::DocumentObjectGroupPython] C_element017  label="C_element : 1"  # scripted group (container) (typed FeaturePython)
  n = 1
  ref = C_element
FEATURE [App::DocumentObjectGroupPython] G4_BORON_CARBIDE  # scripted group (container) (typed FeaturePython)
  Dunit = g/cm3
  Dvalue = 2.52
  Group = -> [B_element001,C_element017]
  conduct = 2
  density = 1
  expand = 3
  formula = G4_BORON_CARBIDE
  name = G4_BORON_CARBIDE
  specific = 4
FEATURE [App::DocumentObjectGroupPython] B_element002  label="B_element : 2"  # scripted group (container) (typed FeaturePython)
  n = 2
  ref = B_element
FEATURE [App::DocumentObjectGroupPython] O_element016  label="O_element : 006"  # scripted group (container) (typed FeaturePython)
  n = 3
  ref = O_element
FEATURE [App::DocumentObjectGroupPython] G4_BORON_OXIDE  # scripted group (container) (typed FeaturePython)
  Dunit = g/cm3
  Dvalue = 1.812
  Group = -> [B_element002,O_element016]
  conduct = 2
  density = 1
  expand = 3
  formula = G4_BORON_OXIDE
  name = G4_BORON_OXIDE
  specific = 4
FEATURE [App::DocumentObjectGroupPython] H_element017  label="H_element : 0.107"  # scripted group (container) (typed FeaturePython)
  n = 0.107
FEATURE [App::DocumentObjectGroupPython] C_element018  label="C_element : 0.145"  # scripted group (container) (typed FeaturePython)
  n = 0.145
FEATURE [App::DocumentObjectGroupPython] N_element012  label="N_element : 0.022"  # scripted group (container) (typed FeaturePython)
  n = 0.022
FEATURE [App::DocumentObjectGroupPython] O_element017  label="O_element : 0.712"  # scripted group (container) (typed FeaturePython)
  n = 0.712
FEATURE [App::DocumentObjectGroupPython] Na_element004  label="Na_element : 0.004"  # scripted group (container) (typed FeaturePython)
  n = 0.002
FEATURE [App::DocumentObjectGroupPython] P_element004  label="P_element : 0.004"  # scripted group (container) (typed FeaturePython)
  n = 0.004
FEATURE [App::DocumentObjectGroupPython] S_element006  label="S_element : 0.005"  # scripted group (container) (typed FeaturePython)
  n = 0.002
FEATURE [App::DocumentObjectGroupPython] Cl_element003  label="Cl_element : 0.004"  # scripted group (container) (typed FeaturePython)
  n = 0.003
FEATURE [App::DocumentObjectGroupPython] K_element002  label="K_element : 0.003"  # scripted group (container) (typed FeaturePython)
  n = 0.003
FEATURE [App::DocumentObjectGroupPython] G4_BRAIN_ICRP  # scripted group (container) (typed FeaturePython)
  Dunit = g/cm3
  Dvalue = 1.04
  Group = -> [H_element017,C_element018,N_element012,O_element017,Na_element004,P_element004,S_element006,Cl_element003,K_element002]
  conduct = 2
  density = 1
  expand = 3
  formula = G4_BRAIN_ICRP
  name = G4_BRAIN_ICRP
  specific = 4
FEATURE [App::DocumentObjectGroupPython] C_element019  label="C_element : 4"  # scripted group (container) (typed FeaturePython)
  n = 4
  ref = C_element
FEATURE [App::DocumentObjectGroupPython] H_element018  label="H_element : 010"  # scripted group (container) (typed FeaturePython)
  n = 10
  ref = H_element
FEATURE [App::DocumentObjectGroupPython] G4_BUTANE  # scripted group (container) (typed FeaturePython)
  Dunit = g/cm3
  Dvalue = 0.00249343
  Group = -> [C_element019,H_element018]
  conduct = 2
  density = 1
  expand = 3
  formula = G4_BUTANE
  name = G4_BUTANE
  specific = 4
FEATURE [App::DocumentObjectGroupPython] C_element020  label="C_element : 008"  # scripted group (container) (typed FeaturePython)
  n = 4
  ref = C_element
FEATURE [App::DocumentObjectGroupPython] H_element019  label="H_element : 011"  # scripted group (container) (typed FeaturePython)
  n = 10
  ref = H_element
FEATURE [App::DocumentObjectGroupPython] O_element018  label="O_element : 007"  # scripted group (container) (typed FeaturePython)
  n = 1
  ref = O_element
FEATURE [App::DocumentObjectGroupPython] G4_N_BUTYL_ALCOHOL  label="G4_N-BUTYL_ALCOHOL"  # scripted group (container) (typed FeaturePython)
  Dunit = g/cm3
  Dvalue = 0.8098
  Group = -> [C_element020,H_element019,O_element018]
  conduct = 2
  density = 1
  expand = 3
  formula = G4_N-BUTYL_ALCOHOL
  name = G4_N-BUTYL_ALCOHOL
  specific = 4
FEATURE [App::DocumentObjectGroupPython] H_element020  label="H_element : 0.025"  # scripted group (container) (typed FeaturePython)
  n = 0.02468
FEATURE [App::DocumentObjectGroupPython] C_element021  label="C_element : 0.502"  # scripted group (container) (typed FeaturePython)
  n = 0.501611
FEATURE [App::DocumentObjectGroupPython] O_element019  label="O_element : 0.005"  # scripted group (container) (typed FeaturePython)
  n = 0.004527
FEATURE [App::DocumentObjectGroupPython] F_element004  label="F_element : 0.465"  # scripted group (container) (typed FeaturePython)
  n = 0.465209
FEATURE [App::DocumentObjectGroupPython] Si_element001  label="Si_element : 0.004"  # scripted group (container) (typed FeaturePython)
  n = 0.003973
FEATURE [App::DocumentObjectGroupPython] G4_C_552  label="G4_C-552"  # scripted group (container) (typed FeaturePython)
  Dunit = g/cm3
  Dvalue = 1.76
  Group = -> [H_element020,C_element021,O_element019,F_element004,Si_element001]
  conduct = 2
  density = 1
  expand = 3
  formula = G4_C-552
  name = G4_C-552
  specific = 4
FEATURE [App::DocumentObjectGroupPython] Cd_element001  label="Cd_element : 1"  # scripted group (container) (typed FeaturePython)
  n = 1
  ref = Cd_element
FEATURE [App::DocumentObjectGroupPython] Te_element001  label="Te_element : 1"  # scripted group (container) (typed FeaturePython)
  n = 1
  ref = Te_element
FEATURE [App::DocumentObjectGroupPython] G4_CADMIUM_TELLURIDE  # scripted group (container) (typed FeaturePython)
  Dunit = g/cm3
  Dvalue = 6.2
  Group = -> [Cd_element001,Te_element001]
  conduct = 2
  density = 1
  expand = 3
  formula = G4_CADMIUM_TELLURIDE
  name = G4_CADMIUM_TELLURIDE
  specific = 4
FEATURE [App::DocumentObjectGroupPython] Cd_element002  label="Cd_element : 002"  # scripted group (container) (typed FeaturePython)
  n = 1
  ref = Cd_element
FEATURE [App::DocumentObjectGroupPython] W_element001  label="W_element : 1"  # scripted group (container) (typed FeaturePython)
  n = 1
  ref = W_element
FEATURE [App::DocumentObjectGroupPython] O_element020  label="O_element : 008"  # scripted group (container) (typed FeaturePython)
  n = 4
  ref = O_element
FEATURE [App::DocumentObjectGroupPython] G4_CADMIUM_TUNGSTATE  # scripted group (container) (typed FeaturePython)
  Dunit = g/cm3
  Dvalue = 7.9
  Group = -> [Cd_element002,W_element001,O_element020]
  conduct = 2
  density = 1
  expand = 3
  formula = G4_CADMIUM_TUNGSTATE
  name = G4_CADMIUM_TUNGSTATE
  specific = 4
FEATURE [App::DocumentObjectGroupPython] Ca_element005  label="Ca_element : 1"  # scripted group (container) (typed FeaturePython)
  n = 1
  ref = Ca_element
FEATURE [App::DocumentObjectGroupPython] C_element022  label="C_element : 009"  # scripted group (container) (typed FeaturePython)
  n = 1
  ref = C_element
FEATURE [App::DocumentObjectGroupPython] O_element021  label="O_element : 009"  # scripted group (container) (typed FeaturePython)
  n = 3
  ref = O_element
FEATURE [App::DocumentObjectGroupPython] G4_CALCIUM_CARBONATE  # scripted group (container) (typed FeaturePython)
  Dunit = g/cm3
  Dvalue = 2.8
  Group = -> [Ca_element005,C_element022,O_element021]
  conduct = 2
  density = 1
  expand = 3
  formula = G4_CALCIUM_CARBONATE
  name = G4_CALCIUM_CARBONATE
  specific = 4
FEATURE [App::DocumentObjectGroupPython] Ca_element006  label="Ca_element : 002"  # scripted group (container) (typed FeaturePython)
  n = 1
  ref = Ca_element
FEATURE [App::DocumentObjectGroupPython] F_element005  label="F_element : 003"  # scripted group (container) (typed FeaturePython)
  n = 2
  ref = F_element
FEATURE [App::DocumentObjectGroupPython] G4_CALCIUM_FLUORIDE  # scripted group (container) (typed FeaturePython)
  Dunit = g/cm3
  Dvalue = 3.18
  Group = -> [Ca_element006,F_element005]
  conduct = 2
  density = 1
  expand = 3
  formula = G4_CALCIUM_FLUORIDE
  name = G4_CALCIUM_FLUORIDE
  specific = 4
FEATURE [App::DocumentObjectGroupPython] Ca_element007  label="Ca_element : 003"  # scripted group (container) (typed FeaturePython)
  n = 1
  ref = Ca_element
FEATURE [App::DocumentObjectGroupPython] O_element022  label="O_element : 010"  # scripted group (container) (typed FeaturePython)
  n = 1
  ref = O_element
FEATURE [App::DocumentObjectGroupPython] G4_CALCIUM_OXIDE  # scripted group (container) (typed FeaturePython)
  Dunit = g/cm3
  Dvalue = 3.3
  Group = -> [Ca_element007,O_element022]
  conduct = 2
  density = 1
  expand = 3
  formula = G4_CALCIUM_OXIDE
  name = G4_CALCIUM_OXIDE
  specific = 4
FEATURE [App::DocumentObjectGroupPython] Ca_element008  label="Ca_element : 004"  # scripted group (container) (typed FeaturePython)
  n = 1
  ref = Ca_element
FEATURE [App::DocumentObjectGroupPython] S_element007  label="S_element : 002"  # scripted group (container) (typed FeaturePython)
  n = 1
  ref = S_element
FEATURE [App::DocumentObjectGroupPython] O_element023  label="O_element : 011"  # scripted group (container) (typed FeaturePython)
  n = 4
  ref = O_element
FEATURE [App::DocumentObjectGroupPython] G4_CALCIUM_SULFATE  # scripted group (container) (typed FeaturePython)
  Dunit = g/cm3
  Dvalue = 2.96
  Group = -> [Ca_element008,S_element007,O_element023]
  conduct = 2
  density = 1
  expand = 3
  formula = G4_CALCIUM_SULFATE
  name = G4_CALCIUM_SULFATE
  specific = 4
FEATURE [App::DocumentObjectGroupPython] Ca_element009  label="Ca_element : 005"  # scripted group (container) (typed FeaturePython)
  n = 1
  ref = Ca_element
FEATURE [App::DocumentObjectGroupPython] W_element002  label="W_element : 002"  # scripted group (container) (typed FeaturePython)
  n = 1
  ref = W_element
FEATURE [App::DocumentObjectGroupPython] O_element024  label="O_element : 012"  # scripted group (container) (typed FeaturePython)
  n = 4
  ref = O_element
FEATURE [App::DocumentObjectGroupPython] G4_CALCIUM_TUNGSTATE  # scripted group (container) (typed FeaturePython)
  Dunit = g/cm3
  Dvalue = 6.062
  Group = -> [Ca_element009,W_element002,O_element024]
  conduct = 2
  density = 1
  expand = 3
  formula = G4_CALCIUM_TUNGSTATE
  name = G4_CALCIUM_TUNGSTATE
  specific = 4
FEATURE [App::DocumentObjectGroupPython] C_element023  label="C_element : 010"  # scripted group (container) (typed FeaturePython)
  n = 1
  ref = C_element
FEATURE [App::DocumentObjectGroupPython] O_element025  label="O_element : 013"  # scripted group (container) (typed FeaturePython)
  n = 2
  ref = O_element
FEATURE [App::DocumentObjectGroupPython] G4_CARBON_DIOXIDE  # scripted group (container) (typed FeaturePython)
  Dunit = g/cm3
  Dvalue = 0.00184212
  Group = -> [C_element023,O_element025]
  conduct = 2
  density = 1
  expand = 3
  formula = G4_CARBON_DIOXIDE
  name = G4_CARBON_DIOXIDE
  specific = 4
FEATURE [App::DocumentObjectGroupPython] C_element024  label="C_element : 011"  # scripted group (container) (typed FeaturePython)
  n = 1
  ref = C_element
FEATURE [App::DocumentObjectGroupPython] Cl_element004  label="Cl_element : 4"  # scripted group (container) (typed FeaturePython)
  n = 4
  ref = Cl_element
FEATURE [App::DocumentObjectGroupPython] G4_CARBON_TETRACHLORIDE  # scripted group (container) (typed FeaturePython)
  Dunit = g/cm3
  Dvalue = 1.594
  Group = -> [C_element024,Cl_element004]
  conduct = 2
  density = 1
  expand = 3
  formula = G4_CARBON_TETRACHLORIDE
  name = G4_CARBON_TETRACHLORIDE
  specific = 4
FEATURE [App::DocumentObjectGroupPython] C_element025  label="C_element : 012"  # scripted group (container) (typed FeaturePython)
  n = 6
  ref = C_element
FEATURE [App::DocumentObjectGroupPython] H_element021  label="H_element : 012"  # scripted group (container) (typed FeaturePython)
  n = 10
  ref = H_element
FEATURE [App::DocumentObjectGroupPython] O_element026  label="O_element : 5"  # scripted group (container) (typed FeaturePython)
  n = 5
  ref = O_element
FEATURE [App::DocumentObjectGroupPython] G4_CELLULOSE_CELLOPHANE  # scripted group (container) (typed FeaturePython)
  Dunit = g/cm3
  Dvalue = 1.42
  Group = -> [C_element025,H_element021,O_element026]
  conduct = 2
  density = 1
  expand = 3
  formula = G4_CELLULOSE_CELLOPHANE
  name = G4_CELLULOSE_CELLOPHANE
  specific = 4
FEATURE [App::DocumentObjectGroupPython] H_element022  label="H_element : 0.067"  # scripted group (container) (typed FeaturePython)
  n = 0.067125
FEATURE [App::DocumentObjectGroupPython] C_element026  label="C_element : 0.545"  # scripted group (container) (typed FeaturePython)
  n = 0.545403
FEATURE [App::DocumentObjectGroupPython] O_element027  label="O_element : 0.387"  # scripted group (container) (typed FeaturePython)
  n = 0.387472
FEATURE [App::DocumentObjectGroupPython] G4_CELLULOSE_BUTYRATE  # scripted group (container) (typed FeaturePython)
  Dunit = g/cm3
  Dvalue = 1.2
  Group = -> [H_element022,C_element026,O_element027]
  conduct = 2
  density = 1
  expand = 3
  formula = G4_CELLULOSE_BUTYRATE
  name = G4_CELLULOSE_BUTYRATE
  specific = 4
FEATURE [App::DocumentObjectGroupPython] H_element023  label="H_element : 0.029"  # scripted group (container) (typed FeaturePython)
  n = 0.029216
FEATURE [App::DocumentObjectGroupPython] C_element027  label="C_element : 0.271"  # scripted group (container) (typed FeaturePython)
  n = 0.271296
FEATURE [App::DocumentObjectGroupPython] N_element013  label="N_element : 0.121"  # scripted group (container) (typed FeaturePython)
  n = 0.121276
FEATURE [App::DocumentObjectGroupPython] O_element028  label="O_element : 0.578"  # scripted group (container) (typed FeaturePython)
  n = 0.578212
FEATURE [App::DocumentObjectGroupPython] G4_CELLULOSE_NITRATE  # scripted group (container) (typed FeaturePython)
  Dunit = g/cm3
  Dvalue = 1.49
  Group = -> [H_element023,C_element027,N_element013,O_element028]
  conduct = 2
  density = 1
  expand = 3
  formula = G4_CELLULOSE_NITRATE
  name = G4_CELLULOSE_NITRATE
  specific = 4
FEATURE [App::DocumentObjectGroupPython] H_element024  label="H_element : 0.108"  # scripted group (container) (typed FeaturePython)
  n = 0.107596
FEATURE [App::DocumentObjectGroupPython] N_element014  label="N_element : 0.001"  # scripted group (container) (typed FeaturePython)
  n = 0.0008
FEATURE [App::DocumentObjectGroupPython] O_element029  label="O_element : 0.875"  # scripted group (container) (typed FeaturePython)
  n = 0.874976
FEATURE [App::DocumentObjectGroupPython] S_element008  label="S_element : 0.015"  # scripted group (container) (typed FeaturePython)
  n = 0.014627
FEATURE [App::DocumentObjectGroupPython] Ce_element001  label="Ce_element : 0.002"  # scripted group (container) (typed FeaturePython)
  n = 0.002001
FEATURE [App::DocumentObjectGroupPython] G4_CERIC_SULFATE  # scripted group (container) (typed FeaturePython)
  Dunit = g/cm3
  Dvalue = 1.03
  Group = -> [H_element024,N_element014,O_element029,S_element008,Ce_element001]
  conduct = 2
  density = 1
  expand = 3
  formula = G4_CERIC_SULFATE
  name = G4_CERIC_SULFATE
  specific = 4
FEATURE [App::DocumentObjectGroupPython] Cs_element001  label="Cs_element : 1"  # scripted group (container) (typed FeaturePython)
  n = 1
  ref = Cs_element
FEATURE [App::DocumentObjectGroupPython] F_element006  label="F_element : 1"  # scripted group (container) (typed FeaturePython)
  n = 1
  ref = F_element
FEATURE [App::DocumentObjectGroupPython] G4_CESIUM_FLUORIDE  # scripted group (container) (typed FeaturePython)
  Dunit = g/cm3
  Dvalue = 4.115
  Group = -> [Cs_element001,F_element006]
  conduct = 2
  density = 1
  expand = 3
  formula = G4_CESIUM_FLUORIDE
  name = G4_CESIUM_FLUORIDE
  specific = 4
FEATURE [App::DocumentObjectGroupPython] Cs_element002  label="Cs_element : 002"  # scripted group (container) (typed FeaturePython)
  n = 1
  ref = Cs_element
FEATURE [App::DocumentObjectGroupPython] I_element001  label="I_element : 1"  # scripted group (container) (typed FeaturePython)
  n = 1
  ref = I_element
FEATURE [App::DocumentObjectGroupPython] G4_CESIUM_IODIDE  # scripted group (container) (typed FeaturePython)
  Dunit = g/cm3
  Dvalue = 4.51
  Group = -> [Cs_element002,I_element001]
  conduct = 2
  density = 1
  expand = 3
  formula = G4_CESIUM_IODIDE
  name = G4_CESIUM_IODIDE
  specific = 4
FEATURE [App::DocumentObjectGroupPython] C_element028  label="C_element : 013"  # scripted group (container) (typed FeaturePython)
  n = 6
  ref = C_element
FEATURE [App::DocumentObjectGroupPython] H_element025  label="H_element : 013"  # scripted group (container) (typed FeaturePython)
  n = 5
  ref = H_element
FEATURE [App::DocumentObjectGroupPython] Cl_element005  label="Cl_element : 1"  # scripted group (container) (typed FeaturePython)
  n = 1
  ref = Cl_element
FEATURE [App::DocumentObjectGroupPython] G4_CHLOROBENZENE  # scripted group (container) (typed FeaturePython)
  Dunit = g/cm3
  Dvalue = 1.1058
  Group = -> [C_element028,H_element025,Cl_element005]
  conduct = 2
  density = 1
  expand = 3
  formula = G4_CHLOROBENZENE
  name = G4_CHLOROBENZENE
  specific = 4
FEATURE [App::DocumentObjectGroupPython] C_element029  label="C_element : 014"  # scripted group (container) (typed FeaturePython)
  n = 1
  ref = C_element
FEATURE [App::DocumentObjectGroupPython] H_element026  label="H_element : 1"  # scripted group (container) (typed FeaturePython)
  n = 1
  ref = H_element
FEATURE [App::DocumentObjectGroupPython] Cl_element006  label="Cl_element : 3"  # scripted group (container) (typed FeaturePython)
  n = 3
  ref = Cl_element
FEATURE [App::DocumentObjectGroupPython] G4_CHLOROFORM  # scripted group (container) (typed FeaturePython)
  Dunit = g/cm3
  Dvalue = 1.4832
  Group = -> [C_element029,H_element026,Cl_element006]
  conduct = 2
  density = 1
  expand = 3
  formula = G4_CHLOROFORM
  name = G4_CHLOROFORM
  specific = 4
FEATURE [App::DocumentObjectGroupPython] H_element027  label="H_element : 0.010"  # scripted group (container) (typed FeaturePython)
  n = 0.01
FEATURE [App::DocumentObjectGroupPython] C_element030  label="C_element : 0.001"  # scripted group (container) (typed FeaturePython)
  n = 0.001
FEATURE [App::DocumentObjectGroupPython] O_element030  label="O_element : 0.529"  # scripted group (container) (typed FeaturePython)
  n = 0.529107
FEATURE [App::DocumentObjectGroupPython] Na_element005  label="Na_element : 0.016"  # scripted group (container) (typed FeaturePython)
  n = 0.016
FEATURE [App::DocumentObjectGroupPython] Mg_element003  label="Mg_element : 0.004"  # scripted group (container) (typed FeaturePython)
  n = 0.002
FEATURE [App::DocumentObjectGroupPython] Al_element002  label="Al_element : 0.034"  # scripted group (container) (typed FeaturePython)
  n = 0.033872
FEATURE [App::DocumentObjectGroupPython] Si_element002  label="Si_element : 0.337"  # scripted group (container) (typed FeaturePython)
  n = 0.337021
FEATURE [App::DocumentObjectGroupPython] K_element003  label="K_element : 0.013"  # scripted group (container) (typed FeaturePython)
  n = 0.013
FEATURE [App::DocumentObjectGroupPython] Ca_element010  label="Ca_element : 0.044"  # scripted group (container) (typed FeaturePython)
  n = 0.044
FEATURE [App::DocumentObjectGroupPython] Fe_element002  label="Fe_element : 0.014"  # scripted group (container) (typed FeaturePython)
  n = 0.014
FEATURE [App::DocumentObjectGroupPython] G4_CONCRETE  # scripted group (container) (typed FeaturePython)
  Dunit = g/cm3
  Dvalue = 2.3
  Group = -> [H_element027,C_element030,O_element030,Na_element005,Mg_element003,Al_element002,Si_element002,K_element003,Ca_element010,Fe_element002]
  conduct = 2
  density = 1
  expand = 3
  formula = G4_CONCRETE
  name = G4_CONCRETE
  specific = 4
FEATURE [App::DocumentObjectGroupPython] C_element031  label="C_element : 015"  # scripted group (container) (typed FeaturePython)
  n = 6
  ref = C_element
FEATURE [App::DocumentObjectGroupPython] H_element028  label="H_element : 12"  # scripted group (container) (typed FeaturePython)
  n = 12
  ref = H_element
FEATURE [App::DocumentObjectGroupPython] G4_CYCLOHEXANE  # scripted group (container) (typed FeaturePython)
  Dunit = g/cm3
  Dvalue = 0.779
  Group = -> [C_element031,H_element028]
  conduct = 2
  density = 1
  expand = 3
  formula = G4_CYCLOHEXANE
  name = G4_CYCLOHEXANE
  specific = 4
FEATURE [App::DocumentObjectGroupPython] C_element032  label="C_element : 016"  # scripted group (container) (typed FeaturePython)
  n = 6
  ref = C_element
FEATURE [App::DocumentObjectGroupPython] H_element029  label="H_element : 4"  # scripted group (container) (typed FeaturePython)
  n = 4
  ref = H_element
FEATURE [App::DocumentObjectGroupPython] Cl_element007  label="Cl_element : 2"  # scripted group (container) (typed FeaturePython)
  n = 2
  ref = Cl_element
FEATURE [App::DocumentObjectGroupPython] G4_1_2_DICHLOROBENZENE  label="G4_1.2-DICHLOROBENZENE"  # scripted group (container) (typed FeaturePython)
  Dunit = g/cm3
  Dvalue = 1.3048
  Group = -> [C_element032,H_element029,Cl_element007]
  conduct = 2
  density = 1
  expand = 3
  formula = G4_1.2-DICHLOROBENZENE
  name = G4_1.2-DICHLOROBENZENE
  specific = 4
FEATURE [App::DocumentObjectGroupPython] C_element033  label="C_element : 017"  # scripted group (container) (typed FeaturePython)
  n = 4
  ref = C_element
FEATURE [App::DocumentObjectGroupPython] H_element030  label="H_element : 8"  # scripted group (container) (typed FeaturePython)
  n = 8
  ref = H_element
FEATURE [App::DocumentObjectGroupPython] O_element031  label="O_element : 014"  # scripted group (container) (typed FeaturePython)
  n = 1
  ref = O_element
FEATURE [App::DocumentObjectGroupPython] Cl_element008  label="Cl_element : 005"  # scripted group (container) (typed FeaturePython)
  n = 2
  ref = Cl_element
FEATURE [App::DocumentObjectGroupPython] G4_DICHLORODIETHYL_ETHER  # scripted group (container) (typed FeaturePython)
  Dunit = g/cm3
  Dvalue = 1.2199
  Group = -> [C_element033,H_element030,O_element031,Cl_element008]
  conduct = 2
  density = 1
  expand = 3
  formula = G4_DICHLORODIETHYL_ETHER
  name = G4_DICHLORODIETHYL_ETHER
  specific = 4
FEATURE [App::DocumentObjectGroupPython] C_element034  label="C_element : 018"  # scripted group (container) (typed FeaturePython)
  n = 2
  ref = C_element
FEATURE [App::DocumentObjectGroupPython] H_element031  label="H_element : 014"  # scripted group (container) (typed FeaturePython)
  n = 4
  ref = H_element
FEATURE [App::DocumentObjectGroupPython] Cl_element009  label="Cl_element : 006"  # scripted group (container) (typed FeaturePython)
  n = 2
  ref = Cl_element
FEATURE [App::DocumentObjectGroupPython] G4_1_2_DICHLOROETHANE  label="G4_1.2-DICHLOROETHANE"  # scripted group (container) (typed FeaturePython)
  Dunit = g/cm3
  Dvalue = 1.2351
  Group = -> [C_element034,H_element031,Cl_element009]
  conduct = 2
  density = 1
  expand = 3
  formula = G4_1.2-DICHLOROETHANE
  name = G4_1.2-DICHLOROETHANE
  specific = 4
FEATURE [App::DocumentObjectGroupPython] C_element035  label="C_element : 019"  # scripted group (container) (typed FeaturePython)
  n = 4
  ref = C_element
FEATURE [App::DocumentObjectGroupPython] H_element032  label="H_element : 015"  # scripted group (container) (typed FeaturePython)
  n = 10
  ref = H_element
FEATURE [App::DocumentObjectGroupPython] O_element032  label="O_element : 015"  # scripted group (container) (typed FeaturePython)
  n = 1
  ref = O_element
FEATURE [App::DocumentObjectGroupPython] G4_DIETHYL_ETHER  # scripted group (container) (typed FeaturePython)
  Dunit = g/cm3
  Dvalue = 0.71378
  Group = -> [C_element035,H_element032,O_element032]
  conduct = 2
  density = 1
  expand = 3
  formula = G4_DIETHYL_ETHER
  name = G4_DIETHYL_ETHER
  specific = 4
FEATURE [App::DocumentObjectGroupPython] C_element036  label="C_element : 020"  # scripted group (container) (typed FeaturePython)
  n = 3
  ref = C_element
FEATURE [App::DocumentObjectGroupPython] H_element033  label="H_element : 016"  # scripted group (container) (typed FeaturePython)
  n = 7
  ref = H_element
FEATURE [App::DocumentObjectGroupPython] N_element015  label="N_element : 008"  # scripted group (container) (typed FeaturePython)
  n = 1
  ref = N_element
FEATURE [App::DocumentObjectGroupPython] O_element033  label="O_element : 016"  # scripted group (container) (typed FeaturePython)
  n = 1
  ref = O_element
FEATURE [App::DocumentObjectGroupPython] G4_N_N_DIMETHYL_FORMAMIDE  label="G4_N.N-DIMETHYL_FORMAMIDE"  # scripted group (container) (typed FeaturePython)
  Dunit = g/cm3
  Dvalue = 0.9487
  Group = -> [C_element036,H_element033,N_element015,O_element033]
  conduct = 2
  density = 1
  expand = 3
  formula = G4_N.N-DIMETHYL_FORMAMIDE
  name = G4_N.N-DIMETHYL_FORMAMIDE
  specific = 4
FEATURE [App::DocumentObjectGroupPython] C_element037  label="C_element : 021"  # scripted group (container) (typed FeaturePython)
  n = 2
  ref = C_element
FEATURE [App::DocumentObjectGroupPython] H_element034  label="H_element : 017"  # scripted group (container) (typed FeaturePython)
  n = 6
  ref = H_element
FEATURE [App::DocumentObjectGroupPython] O_element034  label="O_element : 017"  # scripted group (container) (typed FeaturePython)
  n = 1
  ref = O_element
FEATURE [App::DocumentObjectGroupPython] S_element009  label="S_element : 003"  # scripted group (container) (typed FeaturePython)
  n = 1
  ref = S_element
FEATURE [App::DocumentObjectGroupPython] G4_DIMETHYL_SULFOXIDE  # scripted group (container) (typed FeaturePython)
  Dunit = g/cm3
  Dvalue = 1.1014
  Group = -> [C_element037,H_element034,O_element034,S_element009]
  conduct = 2
  density = 1
  expand = 3
  formula = G4_DIMETHYL_SULFOXIDE
  name = G4_DIMETHYL_SULFOXIDE
  specific = 4
FEATURE [App::DocumentObjectGroupPython] C_element038  label="C_element : 022"  # scripted group (container) (typed FeaturePython)
  n = 2
  ref = C_element
FEATURE [App::DocumentObjectGroupPython] H_element035  label="H_element : 018"  # scripted group (container) (typed FeaturePython)
  n = 6
  ref = H_element
FEATURE [App::DocumentObjectGroupPython] G4_ETHANE  # scripted group (container) (typed FeaturePython)
  Dunit = g/cm3
  Dvalue = 0.00125324
  Group = -> [C_element038,H_element035]
  conduct = 2
  density = 1
  expand = 3
  formula = G4_ETHANE
  name = G4_ETHANE
  specific = 4
FEATURE [App::DocumentObjectGroupPython] C_element039  label="C_element : 023"  # scripted group (container) (typed FeaturePython)
  n = 2
  ref = C_element
FEATURE [App::DocumentObjectGroupPython] H_element036  label="H_element : 019"  # scripted group (container) (typed FeaturePython)
  n = 6
  ref = H_element
FEATURE [App::DocumentObjectGroupPython] O_element035  label="O_element : 018"  # scripted group (container) (typed FeaturePython)
  n = 1
  ref = O_element
FEATURE [App::DocumentObjectGroupPython] G4_ETHYL_ALCOHOL  # scripted group (container) (typed FeaturePython)
  Dunit = g/cm3
  Dvalue = 0.7893
  Group = -> [C_element039,H_element036,O_element035]
  conduct = 2
  density = 1
  expand = 3
  formula = G4_ETHYL_ALCOHOL
  name = G4_ETHYL_ALCOHOL
  specific = 4
FEATURE [App::DocumentObjectGroupPython] H_element037  label="H_element : 0.090"  # scripted group (container) (typed FeaturePython)
  n = 0.090027
FEATURE [App::DocumentObjectGroupPython] C_element040  label="C_element : 0.585"  # scripted group (container) (typed FeaturePython)
  n = 0.585182
FEATURE [App::DocumentObjectGroupPython] O_element036  label="O_element : 0.325"  # scripted group (container) (typed FeaturePython)
  n = 0.324791
FEATURE [App::DocumentObjectGroupPython] G4_ETHYL_CELLULOSE  # scripted group (container) (typed FeaturePython)
  Dunit = g/cm3
  Dvalue = 1.13
  Group = -> [H_element037,C_element040,O_element036]
  conduct = 2
  density = 1
  expand = 3
  formula = G4_ETHYL_CELLULOSE
  name = G4_ETHYL_CELLULOSE
  specific = 4
FEATURE [App::DocumentObjectGroupPython] C_element041  label="C_element : 024"  # scripted group (container) (typed FeaturePython)
  n = 2
  ref = C_element
FEATURE [App::DocumentObjectGroupPython] H_element038  label="H_element : 020"  # scripted group (container) (typed FeaturePython)
  n = 4
  ref = H_element
FEATURE [App::DocumentObjectGroupPython] G4_ETHYLENE  # scripted group (container) (typed FeaturePython)
  Dunit = g/cm3
  Dvalue = 0.00117497
  Group = -> [C_element041,H_element038]
  conduct = 2
  density = 1
  expand = 3
  formula = G4_ETHYLENE
  name = G4_ETHYLENE
  specific = 4
FEATURE [App::DocumentObjectGroupPython] H_element039  label="H_element : 0.096"  # scripted group (container) (typed FeaturePython)
  n = 0.096
FEATURE [App::DocumentObjectGroupPython] C_element042  label="C_element : 0.195"  # scripted group (container) (typed FeaturePython)
  n = 0.195
FEATURE [App::DocumentObjectGroupPython] N_element016  label="N_element : 0.057"  # scripted group (container) (typed FeaturePython)
  n = 0.057
FEATURE [App::DocumentObjectGroupPython] O_element037  label="O_element : 0.646"  # scripted group (container) (typed FeaturePython)
  n = 0.646
FEATURE [App::DocumentObjectGroupPython] Na_element006  label="Na_element : 0.017"  # scripted group (container) (typed FeaturePython)
  n = 0.001
FEATURE [App::DocumentObjectGroupPython] P_element005  label="P_element : 0.104"  # scripted group (container) (typed FeaturePython)
  n = 0.001
FEATURE [App::DocumentObjectGroupPython] S_element010  label="S_element : 0.016"  # scripted group (container) (typed FeaturePython)
  n = 0.003
FEATURE [App::DocumentObjectGroupPython] Cl_element010  label="Cl_element : 0.005"  # scripted group (container) (typed FeaturePython)
  n = 0.001
FEATURE [App::DocumentObjectGroupPython] G4_EYE_LENS_ICRP  # scripted group (container) (typed FeaturePython)
  Dunit = g/cm3
  Dvalue = 1.07
  Group = -> [H_element039,C_element042,N_element016,O_element037,Na_element006,P_element005,S_element010,Cl_element010]
  conduct = 2
  density = 1
  expand = 3
  formula = G4_EYE_LENS_ICRP
  name = G4_EYE_LENS_ICRP
  specific = 4
FEATURE [App::DocumentObjectGroupPython] Fe_element003  label="Fe_element : 2"  # scripted group (container) (typed FeaturePython)
  n = 2
  ref = Fe_element
FEATURE [App::DocumentObjectGroupPython] O_element038  label="O_element : 019"  # scripted group (container) (typed FeaturePython)
  n = 3
  ref = O_element
FEATURE [App::DocumentObjectGroupPython] G4_FERRIC_OXIDE  # scripted group (container) (typed FeaturePython)
  Dunit = g/cm3
  Dvalue = 5.2
  Group = -> [Fe_element003,O_element038]
  conduct = 2
  density = 1
  expand = 3
  formula = G4_FERRIC_OXIDE
  name = G4_FERRIC_OXIDE
  specific = 4
FEATURE [App::DocumentObjectGroupPython] Fe_element004  label="Fe_element : 1"  # scripted group (container) (typed FeaturePython)
  n = 1
  ref = Fe_element
FEATURE [App::DocumentObjectGroupPython] B_element003  label="B_element : 1"  # scripted group (container) (typed FeaturePython)
  n = 1
  ref = B_element
FEATURE [App::DocumentObjectGroupPython] G4_FERROBORIDE  # scripted group (container) (typed FeaturePython)
  Dunit = g/cm3
  Dvalue = 7.15
  Group = -> [Fe_element004,B_element003]
  conduct = 2
  density = 1
  expand = 3
  formula = G4_FERROBORIDE
  name = G4_FERROBORIDE
  specific = 4
FEATURE [App::DocumentObjectGroupPython] Fe_element005  label="Fe_element : 003"  # scripted group (container) (typed FeaturePython)
  n = 1
  ref = Fe_element
FEATURE [App::DocumentObjectGroupPython] O_element039  label="O_element : 020"  # scripted group (container) (typed FeaturePython)
  n = 1
  ref = O_element
FEATURE [App::DocumentObjectGroupPython] G4_FERROUS_OXIDE  # scripted group (container) (typed FeaturePython)
  Dunit = g/cm3
  Dvalue = 5.7
  Group = -> [Fe_element005,O_element039]
  conduct = 2
  density = 1
  expand = 3
  formula = G4_FERROUS_OXIDE
  name = G4_FERROUS_OXIDE
  specific = 4
FEATURE [App::DocumentObjectGroupPython] H_element040  label="H_element : 0.115"  # scripted group (container) (typed FeaturePython)
  n = 0.108259
FEATURE [App::DocumentObjectGroupPython] N_element017  label="N_element : 0.000"  # scripted group (container) (typed FeaturePython)
  n = 2.7e-05
FEATURE [App::DocumentObjectGroupPython] O_element040  label="O_element : 0.879"  # scripted group (container) (typed FeaturePython)
  n = 0.878636
FEATURE [App::DocumentObjectGroupPython] Na_element007  label="Na_element : 0.000"  # scripted group (container) (typed FeaturePython)
  n = 2.2e-05
FEATURE [App::DocumentObjectGroupPython] S_element011  label="S_element : 0.013"  # scripted group (container) (typed FeaturePython)
  n = 0.012968
FEATURE [App::DocumentObjectGroupPython] Cl_element011  label="Cl_element : 0.000"  # scripted group (container) (typed FeaturePython)
  n = 3.4e-05
FEATURE [App::DocumentObjectGroupPython] Fe_element006  label="Fe_element : 0.000"  # scripted group (container) (typed FeaturePython)
  n = 5.4e-05
FEATURE [App::DocumentObjectGroupPython] G4_FERROUS_SULFATE  # scripted group (container) (typed FeaturePython)
  Dunit = g/cm3
  Dvalue = 1.024
  Group = -> [H_element040,N_element017,O_element040,Na_element007,S_element011,Cl_element011,Fe_element006]
  conduct = 2
  density = 1
  expand = 3
  formula = G4_FERROUS_SULFATE
  name = G4_FERROUS_SULFATE
  specific = 4
FEATURE [App::DocumentObjectGroupPython] C_element043  label="C_element : 0.099"  # scripted group (container) (typed FeaturePython)
  n = 0.099335
FEATURE [App::DocumentObjectGroupPython] F_element007  label="F_element : 0.314"  # scripted group (container) (typed FeaturePython)
  n = 0.314247
FEATURE [App::DocumentObjectGroupPython] Cl_element012  label="Cl_element : 0.586"  # scripted group (container) (typed FeaturePython)
  n = 0.586418
FEATURE [App::DocumentObjectGroupPython] G4_FREON_12  label="G4_FREON-12"  # scripted group (container) (typed FeaturePython)
  Dunit = g/cm3
  Dvalue = 1.12
  Group = -> [C_element043,F_element007,Cl_element012]
  conduct = 2
  density = 1
  expand = 3
  formula = G4_FREON-12
  name = G4_FREON-12
  specific = 4
FEATURE [App::DocumentObjectGroupPython] C_element044  label="C_element : 0.057"  # scripted group (container) (typed FeaturePython)
  n = 0.057245
FEATURE [App::DocumentObjectGroupPython] F_element008  label="F_element : 0.181"  # scripted group (container) (typed FeaturePython)
  n = 0.181096
FEATURE [App::DocumentObjectGroupPython] Br_element001  label="Br_element : 0.762"  # scripted group (container) (typed FeaturePython)
  n = 0.761659
FEATURE [App::DocumentObjectGroupPython] G4_FREON_12B2  label="G4_FREON-12B2"  # scripted group (container) (typed FeaturePython)
  Dunit = g/cm3
  Dvalue = 1.8
  Group = -> [C_element044,F_element008,Br_element001]
  conduct = 2
  density = 1
  expand = 3
  formula = G4_FREON-12B2
  name = G4_FREON-12B2
  specific = 4
FEATURE [App::DocumentObjectGroupPython] C_element045  label="C_element : 0.115"  # scripted group (container) (typed FeaturePython)
  n = 0.114983
FEATURE [App::DocumentObjectGroupPython] F_element009  label="F_element : 0.546"  # scripted group (container) (typed FeaturePython)
  n = 0.545621
FEATURE [App::DocumentObjectGroupPython] Cl_element013  label="Cl_element : 0.339"  # scripted group (container) (typed FeaturePython)
  n = 0.339396
FEATURE [App::DocumentObjectGroupPython] G4_FREON_13  label="G4_FREON-13"  # scripted group (container) (typed FeaturePython)
  Dunit = g/cm3
  Dvalue = 0.95
  Group = -> [C_element045,F_element009,Cl_element013]
  conduct = 2
  density = 1
  expand = 3
  formula = G4_FREON-13
  name = G4_FREON-13
  specific = 4
FEATURE [App::DocumentObjectGroupPython] C_element046  label="C_element : 025"  # scripted group (container) (typed FeaturePython)
  n = 1
  ref = C_element
FEATURE [App::DocumentObjectGroupPython] F_element010  label="F_element : 3"  # scripted group (container) (typed FeaturePython)
  n = 3
  ref = F_element
FEATURE [App::DocumentObjectGroupPython] Br_element002  label="Br_element : 1"  # scripted group (container) (typed FeaturePython)
  n = 1
  ref = Br_element
FEATURE [App::DocumentObjectGroupPython] G4_FREON_13B1  label="G4_FREON-13B1"  # scripted group (container) (typed FeaturePython)
  Dunit = g/cm3
  Dvalue = 1.5
  Group = -> [C_element046,F_element010,Br_element002]
  conduct = 2
  density = 1
  expand = 3
  formula = G4_FREON-13B1
  name = G4_FREON-13B1
  specific = 4
FEATURE [App::DocumentObjectGroupPython] C_element047  label="C_element : 0.061"  # scripted group (container) (typed FeaturePython)
  n = 0.061309
FEATURE [App::DocumentObjectGroupPython] F_element011  label="F_element : 0.291"  # scripted group (container) (typed FeaturePython)
  n = 0.290924
FEATURE [App::DocumentObjectGroupPython] I_element002  label="I_element : 0.648"  # scripted group (container) (typed FeaturePython)
  n = 0.647767
FEATURE [App::DocumentObjectGroupPython] G4_FREON_13I1  label="G4_FREON-13I1"  # scripted group (container) (typed FeaturePython)
  Dunit = g/cm3
  Dvalue = 1.8
  Group = -> [C_element047,F_element011,I_element002]
  conduct = 2
  density = 1
  expand = 3
  formula = G4_FREON-13I1
  name = G4_FREON-13I1
  specific = 4
FEATURE [App::DocumentObjectGroupPython] Gd_element001  label="Gd_element : 2"  # scripted group (container) (typed FeaturePython)
  n = 2
  ref = Gd_element
FEATURE [App::DocumentObjectGroupPython] O_element041  label="O_element : 021"  # scripted group (container) (typed FeaturePython)
  n = 2
  ref = O_element
FEATURE [App::DocumentObjectGroupPython] S_element012  label="S_element : 004"  # scripted group (container) (typed FeaturePython)
  n = 1
  ref = S_element
FEATURE [App::DocumentObjectGroupPython] G4_GADOLINIUM_OXYSULFIDE  # scripted group (container) (typed FeaturePython)
  Dunit = g/cm3
  Dvalue = 7.44
  Group = -> [Gd_element001,O_element041,S_element012]
  conduct = 2
  density = 1
  expand = 3
  formula = G4_GADOLINIUM_OXYSULFIDE
  name = G4_GADOLINIUM_OXYSULFIDE
  specific = 4
FEATURE [App::DocumentObjectGroupPython] Ga_element001  label="Ga_element : 1"  # scripted group (container) (typed FeaturePython)
  n = 1
  ref = Ga_element
FEATURE [App::DocumentObjectGroupPython] As_element001  label="As_element : 1"  # scripted group (container) (typed FeaturePython)
  n = 1
  ref = As_element
FEATURE [App::DocumentObjectGroupPython] G4_GALLIUM_ARSENIDE  # scripted group (container) (typed FeaturePython)
  Dunit = g/cm3
  Dvalue = 5.31
  Group = -> [Ga_element001,As_element001]
  conduct = 2
  density = 1
  expand = 3
  formula = G4_GALLIUM_ARSENIDE
  name = G4_GALLIUM_ARSENIDE
  specific = 4
FEATURE [App::DocumentObjectGroupPython] H_element041  label="H_element : 0.081"  # scripted group (container) (typed FeaturePython)
  n = 0.08118
FEATURE [App::DocumentObjectGroupPython] C_element048  label="C_element : 0.416"  # scripted group (container) (typed FeaturePython)
  n = 0.41606
FEATURE [App::DocumentObjectGroupPython] N_element018  label="N_element : 0.111"  # scripted group (container) (typed FeaturePython)
  n = 0.11124
FEATURE [App::DocumentObjectGroupPython] O_element042  label="O_element : 0.381"  # scripted group (container) (typed FeaturePython)
  n = 0.38064
FEATURE [App::DocumentObjectGroupPython] S_element013  label="S_element : 0.011"  # scripted group (container) (typed FeaturePython)
  n = 0.01088
FEATURE [App::DocumentObjectGroupPython] G4_GEL_PHOTO_EMULSION  # scripted group (container) (typed FeaturePython)
  Dunit = g/cm3
  Dvalue = 1.2914
  Group = -> [H_element041,C_element048,N_element018,O_element042,S_element013]
  conduct = 2
  density = 1
  expand = 3
  formula = G4_GEL_PHOTO_EMULSION
  name = G4_GEL_PHOTO_EMULSION
  specific = 4
FEATURE [App::DocumentObjectGroupPython] B_element004  label="B_element : 0.040"  # scripted group (container) (typed FeaturePython)
  n = 0.0400639
FEATURE [App::DocumentObjectGroupPython] O_element043  label="O_element : 0.540"  # scripted group (container) (typed FeaturePython)
  n = 0.539561
FEATURE [App::DocumentObjectGroupPython] Na_element008  label="Na_element : 0.028"  # scripted group (container) (typed FeaturePython)
  n = 0.0281909
FEATURE [App::DocumentObjectGroupPython] Al_element003  label="Al_element : 0.012"  # scripted group (container) (typed FeaturePython)
  n = 0.011644
FEATURE [App::DocumentObjectGroupPython] Si_element003  label="Si_element : 0.377"  # scripted group (container) (typed FeaturePython)
  n = 0.377219
FEATURE [App::DocumentObjectGroupPython] K_element004  label="K_element : 0.014"  # scripted group (container) (typed FeaturePython)
  n = 0.00332099
FEATURE [App::DocumentObjectGroupPython] G4_Pyrex_Glass  # scripted group (container) (typed FeaturePython)
  Dunit = g/cm3
  Dvalue = 2.23
  Group = -> [B_element004,O_element043,Na_element008,Al_element003,Si_element003,K_element004]
  conduct = 2
  density = 1
  expand = 3
  formula = G4_Pyrex_Glass
  name = G4_Pyrex_Glass
  specific = 4
FEATURE [App::DocumentObjectGroupPython] O_element044  label="O_element : 0.156"  # scripted group (container) (typed FeaturePython)
  n = 0.156453
FEATURE [App::DocumentObjectGroupPython] Si_element004  label="Si_element : 0.081"  # scripted group (container) (typed FeaturePython)
  n = 0.080866
FEATURE [App::DocumentObjectGroupPython] Ti_element001  label="Ti_element : 0.008"  # scripted group (container) (typed FeaturePython)
  n = 0.008092
FEATURE [App::DocumentObjectGroupPython] As_element002  label="As_element : 0.003"  # scripted group (container) (typed FeaturePython)
  n = 0.002651
FEATURE [App::DocumentObjectGroupPython] Pb_element001  label="Pb_element : 0.752"  # scripted group (container) (typed FeaturePython)
  n = 0.751938
FEATURE [App::DocumentObjectGroupPython] G4_GLASS_LEAD  # scripted group (container) (typed FeaturePython)
  Dunit = g/cm3
  Dvalue = 6.22
  Group = -> [O_element044,Si_element004,Ti_element001,As_element002,Pb_element001]
  conduct = 2
  density = 1
  expand = 3
  formula = G4_GLASS_LEAD
  name = G4_GLASS_LEAD
  specific = 4
FEATURE [App::DocumentObjectGroupPython] O_element045  label="O_element : 0.460"  # scripted group (container) (typed FeaturePython)
  n = 0.4598
FEATURE [App::DocumentObjectGroupPython] Na_element009  label="Na_element : 0.096"  # scripted group (container) (typed FeaturePython)
  n = 0.0964411
FEATURE [App::DocumentObjectGroupPython] Si_element005  label="Si_element : 0.378"  # scripted group (container) (typed FeaturePython)
  n = 0.336553
FEATURE [App::DocumentObjectGroupPython] Ca_element011  label="Ca_element : 0.107"  # scripted group (container) (typed FeaturePython)
  n = 0.107205
FEATURE [App::DocumentObjectGroupPython] G4_GLASS_PLATE  # scripted group (container) (typed FeaturePython)
  Dunit = g/cm3
  Dvalue = 2.4
  Group = -> [O_element045,Na_element009,Si_element005,Ca_element011]
  conduct = 2
  density = 1
  expand = 3
  formula = G4_GLASS_PLATE
  name = G4_GLASS_PLATE
  specific = 4
FEATURE [App::DocumentObjectGroupPython] C_element049  label="C_element : 026"  # scripted group (container) (typed FeaturePython)
  n = 5
  ref = C_element
FEATURE [App::DocumentObjectGroupPython] H_element042  label="H_element : 021"  # scripted group (container) (typed FeaturePython)
  n = 10
  ref = H_element
FEATURE [App::DocumentObjectGroupPython] N_element019  label="N_element : 2"  # scripted group (container) (typed FeaturePython)
  n = 2
  ref = N_element
FEATURE [App::DocumentObjectGroupPython] O_element046  label="O_element : 022"  # scripted group (container) (typed FeaturePython)
  n = 3
  ref = O_element
FEATURE [App::DocumentObjectGroupPython] G4_GLUTAMINE  # scripted group (container) (typed FeaturePython)
  Dunit = g/cm3
  Dvalue = 1.46
  Group = -> [C_element049,H_element042,N_element019,O_element046]
  conduct = 2
  density = 1
  expand = 3
  formula = G4_GLUTAMINE
  name = G4_GLUTAMINE
  specific = 4
FEATURE [App::DocumentObjectGroupPython] C_element050  label="C_element : 027"  # scripted group (container) (typed FeaturePython)
  n = 3
  ref = C_element
FEATURE [App::DocumentObjectGroupPython] H_element043  label="H_element : 022"  # scripted group (container) (typed FeaturePython)
  n = 8
  ref = H_element
FEATURE [App::DocumentObjectGroupPython] O_element047  label="O_element : 023"  # scripted group (container) (typed FeaturePython)
  n = 3
  ref = O_element
FEATURE [App::DocumentObjectGroupPython] G4_GLYCEROL  # scripted group (container) (typed FeaturePython)
  Dunit = g/cm3
  Dvalue = 1.2613
  Group = -> [C_element050,H_element043,O_element047]
  conduct = 2
  density = 1
  expand = 3
  formula = G4_GLYCEROL
  name = G4_GLYCEROL
  specific = 4
FEATURE [App::DocumentObjectGroupPython] C_element051  label="C_element : 028"  # scripted group (container) (typed FeaturePython)
  n = 5
  ref = C_element
FEATURE [App::DocumentObjectGroupPython] H_element044  label="H_element : 023"  # scripted group (container) (typed FeaturePython)
  n = 5
  ref = H_element
FEATURE [App::DocumentObjectGroupPython] N_element020  label="N_element : 009"  # scripted group (container) (typed FeaturePython)
  n = 5
  ref = N_element
FEATURE [App::DocumentObjectGroupPython] O_element048  label="O_element : 024"  # scripted group (container) (typed FeaturePython)
  n = 1
  ref = O_element
FEATURE [App::DocumentObjectGroupPython] G4_GUANINE  # scripted group (container) (typed FeaturePython)
  Dunit = g/cm3
  Dvalue = 2.2
  Group = -> [C_element051,H_element044,N_element020,O_element048]
  conduct = 2
  density = 1
  expand = 3
  formula = G4_GUANINE
  name = G4_GUANINE
  specific = 4
FEATURE [App::DocumentObjectGroupPython] Ca_element012  label="Ca_element : 006"  # scripted group (container) (typed FeaturePython)
  n = 1
  ref = Ca_element
FEATURE [App::DocumentObjectGroupPython] S_element014  label="S_element : 005"  # scripted group (container) (typed FeaturePython)
  n = 1
  ref = S_element
FEATURE [App::DocumentObjectGroupPython] O_element049  label="O_element : 6"  # scripted group (container) (typed FeaturePython)
  n = 6
  ref = O_element
FEATURE [App::DocumentObjectGroupPython] H_element045  label="H_element : 024"  # scripted group (container) (typed FeaturePython)
  n = 4
  ref = H_element
FEATURE [App::DocumentObjectGroupPython] G4_GYPSUM  # scripted group (container) (typed FeaturePython)
  Dunit = g/cm3
  Dvalue = 2.32
  Group = -> [Ca_element012,S_element014,O_element049,H_element045]
  conduct = 2
  density = 1
  expand = 3
  formula = G4_GYPSUM
  name = G4_GYPSUM
  specific = 4
FEATURE [App::DocumentObjectGroupPython] C_element052  label="C_element : 7"  # scripted group (container) (typed FeaturePython)
  n = 7
  ref = C_element
FEATURE [App::DocumentObjectGroupPython] H_element046  label="H_element : 16"  # scripted group (container) (typed FeaturePython)
  n = 16
  ref = H_element
FEATURE [App::DocumentObjectGroupPython] G4_N_HEPTANE  label="G4_N-HEPTANE"  # scripted group (container) (typed FeaturePython)
  Dunit = g/cm3
  Dvalue = 0.68376
  Group = -> [C_element052,H_element046]
  conduct = 2
  density = 1
  expand = 3
  formula = G4_N-HEPTANE
  name = G4_N-HEPTANE
  specific = 4
FEATURE [App::DocumentObjectGroupPython] C_element053  label="C_element : 029"  # scripted group (container) (typed FeaturePython)
  n = 6
  ref = C_element
FEATURE [App::DocumentObjectGroupPython] H_element047  label="H_element : 14"  # scripted group (container) (typed FeaturePython)
  n = 14
  ref = H_element
FEATURE [App::DocumentObjectGroupPython] G4_N_HEXANE  label="G4_N-HEXANE"  # scripted group (container) (typed FeaturePython)
  Dunit = g/cm3
  Dvalue = 0.6603
  Group = -> [C_element053,H_element047]
  conduct = 2
  density = 1
  expand = 3
  formula = G4_N-HEXANE
  name = G4_N-HEXANE
  specific = 4
FEATURE [App::DocumentObjectGroupPython] C_element054  label="C_element : 22"  # scripted group (container) (typed FeaturePython)
  n = 22
  ref = C_element
FEATURE [App::DocumentObjectGroupPython] H_element048  label="H_element : 025"  # scripted group (container) (typed FeaturePython)
  n = 10
  ref = H_element
FEATURE [App::DocumentObjectGroupPython] N_element021  label="N_element : 010"  # scripted group (container) (typed FeaturePython)
  n = 2
  ref = N_element
FEATURE [App::DocumentObjectGroupPython] O_element050  label="O_element : 025"  # scripted group (container) (typed FeaturePython)
  n = 5
  ref = O_element
FEATURE [App::DocumentObjectGroupPython] G4_KAPTON  # scripted group (container) (typed FeaturePython)
  Dunit = g/cm3
  Dvalue = 1.42
  Group = -> [C_element054,H_element048,N_element021,O_element050]
  conduct = 2
  density = 1
  expand = 3
  formula = G4_KAPTON
  name = G4_KAPTON
  specific = 4
FEATURE [App::DocumentObjectGroupPython] La_element001  label="La_element : 1"  # scripted group (container) (typed FeaturePython)
  n = 1
  ref = La_element
FEATURE [App::DocumentObjectGroupPython] Br_element003  label="Br_element : 002"  # scripted group (container) (typed FeaturePython)
  n = 1
  ref = Br_element
FEATURE [App::DocumentObjectGroupPython] O_element051  label="O_element : 026"  # scripted group (container) (typed FeaturePython)
  n = 1
  ref = O_element
FEATURE [App::DocumentObjectGroupPython] G4_LANTHANUM_OXYBROMIDE  # scripted group (container) (typed FeaturePython)
  Dunit = g/cm3
  Dvalue = 6.28
  Group = -> [La_element001,Br_element003,O_element051]
  conduct = 2
  density = 1
  expand = 3
  formula = G4_LANTHANUM_OXYBROMIDE
  name = G4_LANTHANUM_OXYBROMIDE
  specific = 4
FEATURE [App::DocumentObjectGroupPython] La_element002  label="La_element : 2"  # scripted group (container) (typed FeaturePython)
  n = 2
  ref = La_element
FEATURE [App::DocumentObjectGroupPython] O_element052  label="O_element : 027"  # scripted group (container) (typed FeaturePython)
  n = 2
  ref = O_element
FEATURE [App::DocumentObjectGroupPython] S_element015  label="S_element : 006"  # scripted group (container) (typed FeaturePython)
  n = 1
  ref = S_element
FEATURE [App::DocumentObjectGroupPython] G4_LANTHANUM_OXYSULFIDE  # scripted group (container) (typed FeaturePython)
  Dunit = g/cm3
  Dvalue = 5.86
  Group = -> [La_element002,O_element052,S_element015]
  conduct = 2
  density = 1
  expand = 3
  formula = G4_LANTHANUM_OXYSULFIDE
  name = G4_LANTHANUM_OXYSULFIDE
  specific = 4
FEATURE [App::DocumentObjectGroupPython] O_element053  label="O_element : 0.072"  # scripted group (container) (typed FeaturePython)
  n = 0.071682
FEATURE [App::DocumentObjectGroupPython] Pb_element002  label="Pb_element : 0.928"  # scripted group (container) (typed FeaturePython)
  n = 0.928318
FEATURE [App::DocumentObjectGroupPython] G4_LEAD_OXIDE  # scripted group (container) (typed FeaturePython)
  Dunit = g/cm3
  Dvalue = 9.53
  Group = -> [O_element053,Pb_element002]
  conduct = 2
  density = 1
  expand = 3
  formula = G4_LEAD_OXIDE
  name = G4_LEAD_OXIDE
  specific = 4
FEATURE [App::DocumentObjectGroupPython] Li_element001  label="Li_element : 1"  # scripted group (container) (typed FeaturePython)
  n = 1
  ref = Li_element
FEATURE [App::DocumentObjectGroupPython] N_element022  label="N_element : 011"  # scripted group (container) (typed FeaturePython)
  n = 1
  ref = N_element
FEATURE [App::DocumentObjectGroupPython] H_element049  label="H_element : 026"  # scripted group (container) (typed FeaturePython)
  n = 2
  ref = H_element
FEATURE [App::DocumentObjectGroupPython] G4_LITHIUM_AMIDE  # scripted group (container) (typed FeaturePython)
  Dunit = g/cm3
  Dvalue = 1.178
  Group = -> [Li_element001,N_element022,H_element049]
  conduct = 2
  density = 1
  expand = 3
  formula = G4_LITHIUM_AMIDE
  name = G4_LITHIUM_AMIDE
  specific = 4
FEATURE [App::DocumentObjectGroupPython] Li_element002  label="Li_element : 2"  # scripted group (container) (typed FeaturePython)
  n = 2
  ref = Li_element
FEATURE [App::DocumentObjectGroupPython] C_element055  label="C_element : 030"  # scripted group (container) (typed FeaturePython)
  n = 1
  ref = C_element
FEATURE [App::DocumentObjectGroupPython] O_element054  label="O_element : 028"  # scripted group (container) (typed FeaturePython)
  n = 3
  ref = O_element
FEATURE [App::DocumentObjectGroupPython] G4_LITHIUM_CARBONATE  # scripted group (container) (typed FeaturePython)
  Dunit = g/cm3
  Dvalue = 2.11
  Group = -> [Li_element002,C_element055,O_element054]
  conduct = 2
  density = 1
  expand = 3
  formula = G4_LITHIUM_CARBONATE
  name = G4_LITHIUM_CARBONATE
  specific = 4
FEATURE [App::DocumentObjectGroupPython] Li_element003  label="Li_element : 003"  # scripted group (container) (typed FeaturePython)
  n = 1
  ref = Li_element
FEATURE [App::DocumentObjectGroupPython] F_element012  label="F_element : 004"  # scripted group (container) (typed FeaturePython)
  n = 1
  ref = F_element
FEATURE [App::DocumentObjectGroupPython] G4_LITHIUM_FLUORIDE  # scripted group (container) (typed FeaturePython)
  Dunit = g/cm3
  Dvalue = 2.635
  Group = -> [Li_element003,F_element012]
  conduct = 2
  density = 1
  expand = 3
  formula = G4_LITHIUM_FLUORIDE
  name = G4_LITHIUM_FLUORIDE
  specific = 4
FEATURE [App::DocumentObjectGroupPython] Li_element004  label="Li_element : 004"  # scripted group (container) (typed FeaturePython)
  n = 1
  ref = Li_element
FEATURE [App::DocumentObjectGroupPython] H_element050  label="H_element : 027"  # scripted group (container) (typed FeaturePython)
  n = 1
  ref = H_element
FEATURE [App::DocumentObjectGroupPython] G4_LITHIUM_HYDRIDE  # scripted group (container) (typed FeaturePython)
  Dunit = g/cm3
  Dvalue = 0.82
  Group = -> [Li_element004,H_element050]
  conduct = 2
  density = 1
  expand = 3
  formula = G4_LITHIUM_HYDRIDE
  name = G4_LITHIUM_HYDRIDE
  specific = 4
FEATURE [App::DocumentObjectGroupPython] Li_element005  label="Li_element : 005"  # scripted group (container) (typed FeaturePython)
  n = 1
  ref = Li_element
FEATURE [App::DocumentObjectGroupPython] I_element003  label="I_element : 002"  # scripted group (container) (typed FeaturePython)
  n = 1
  ref = I_element
FEATURE [App::DocumentObjectGroupPython] G4_LITHIUM_IODIDE  # scripted group (container) (typed FeaturePython)
  Dunit = g/cm3
  Dvalue = 3.494
  Group = -> [Li_element005,I_element003]
  conduct = 2
  density = 1
  expand = 3
  formula = G4_LITHIUM_IODIDE
  name = G4_LITHIUM_IODIDE
  specific = 4
FEATURE [App::DocumentObjectGroupPython] Li_element006  label="Li_element : 006"  # scripted group (container) (typed FeaturePython)
  n = 2
  ref = Li_element
FEATURE [App::DocumentObjectGroupPython] O_element055  label="O_element : 029"  # scripted group (container) (typed FeaturePython)
  n = 1
  ref = O_element
FEATURE [App::DocumentObjectGroupPython] G4_LITHIUM_OXIDE  # scripted group (container) (typed FeaturePython)
  Dunit = g/cm3
  Dvalue = 2.013
  Group = -> [Li_element006,O_element055]
  conduct = 2
  density = 1
  expand = 3
  formula = G4_LITHIUM_OXIDE
  name = G4_LITHIUM_OXIDE
  specific = 4
FEATURE [App::DocumentObjectGroupPython] Li_element007  label="Li_element : 007"  # scripted group (container) (typed FeaturePython)
  n = 2
  ref = Li_element
FEATURE [App::DocumentObjectGroupPython] B_element005  label="B_element : 005"  # scripted group (container) (typed FeaturePython)
  n = 4
  ref = B_element
FEATURE [App::DocumentObjectGroupPython] O_element056  label="O_element : 7"  # scripted group (container) (typed FeaturePython)
  n = 7
  ref = O_element
FEATURE [App::DocumentObjectGroupPython] G4_LITHIUM_TETRABORATE  # scripted group (container) (typed FeaturePython)
  Dunit = g/cm3
  Dvalue = 2.44
  Group = -> [Li_element007,B_element005,O_element056]
  conduct = 2
  density = 1
  expand = 3
  formula = G4_LITHIUM_TETRABORATE
  name = G4_LITHIUM_TETRABORATE
  specific = 4
FEATURE [App::DocumentObjectGroupPython] H_element051  label="H_element : 0.105"  # scripted group (container) (typed FeaturePython)
  n = 0.105
FEATURE [App::DocumentObjectGroupPython] C_element056  label="C_element : 0.083"  # scripted group (container) (typed FeaturePython)
  n = 0.083
FEATURE [App::DocumentObjectGroupPython] N_element023  label="N_element : 0.023"  # scripted group (container) (typed FeaturePython)
  n = 0.023
FEATURE [App::DocumentObjectGroupPython] O_element057  label="O_element : 0.779"  # scripted group (container) (typed FeaturePython)
  n = 0.779
FEATURE [App::DocumentObjectGroupPython] Na_element010  label="Na_element : 0.097"  # scripted group (container) (typed FeaturePython)
  n = 0.002
FEATURE [App::DocumentObjectGroupPython] P_element006  label="P_element : 0.105"  # scripted group (container) (typed FeaturePython)
  n = 0.001
FEATURE [App::DocumentObjectGroupPython] S_element016  label="S_element : 0.017"  # scripted group (container) (typed FeaturePython)
  n = 0.002
FEATURE [App::DocumentObjectGroupPython] Cl_element014  label="Cl_element : 0.587"  # scripted group (container) (typed FeaturePython)
  n = 0.003
FEATURE [App::DocumentObjectGroupPython] K_element005  label="K_element : 0.015"  # scripted group (container) (typed FeaturePython)
  n = 0.002
FEATURE [App::DocumentObjectGroupPython] G4_LUNG_ICRP  # scripted group (container) (typed FeaturePython)
  Dunit = g/cm3
  Dvalue = 1.04
  Group = -> [H_element051,C_element056,N_element023,O_element057,Na_element010,P_element006,S_element016,Cl_element014,K_element005]
  conduct = 2
  density = 1
  expand = 3
  formula = G4_LUNG_ICRP
  name = G4_LUNG_ICRP
  specific = 4
FEATURE [App::DocumentObjectGroupPython] H_element052  label="H_element : 0.116"  # scripted group (container) (typed FeaturePython)
  n = 0.114318
FEATURE [App::DocumentObjectGroupPython] C_element057  label="C_element : 0.656"  # scripted group (container) (typed FeaturePython)
  n = 0.655824
FEATURE [App::DocumentObjectGroupPython] O_element058  label="O_element : 0.092"  # scripted group (container) (typed FeaturePython)
  n = 0.0921831
FEATURE [App::DocumentObjectGroupPython] Mg_element004  label="Mg_element : 0.135"  # scripted group (container) (typed FeaturePython)
  n = 0.134792
FEATURE [App::DocumentObjectGroupPython] Ca_element013  label="Ca_element : 0.003"  # scripted group (container) (typed FeaturePython)
  n = 0.002883
FEATURE [App::DocumentObjectGroupPython] G4_M3_WAX  # scripted group (container) (typed FeaturePython)
  Dunit = g/cm3
  Dvalue = 1.05
  Group = -> [H_element052,C_element057,O_element058,Mg_element004,Ca_element013]
  conduct = 2
  density = 1
  expand = 3
  formula = G4_M3_WAX
  name = G4_M3_WAX
  specific = 4
FEATURE [App::DocumentObjectGroupPython] Mg_element005  label="Mg_element : 1"  # scripted group (container) (typed FeaturePython)
  n = 1
  ref = Mg_element
FEATURE [App::DocumentObjectGroupPython] C_element058  label="C_element : 031"  # scripted group (container) (typed FeaturePython)
  n = 1
  ref = C_element
FEATURE [App::DocumentObjectGroupPython] O_element059  label="O_element : 030"  # scripted group (container) (typed FeaturePython)
  n = 3
  ref = O_element
FEATURE [App::DocumentObjectGroupPython] G4_MAGNESIUM_CARBONATE  # scripted group (container) (typed FeaturePython)
  Dunit = g/cm3
  Dvalue = 2.958
  Group = -> [Mg_element005,C_element058,O_element059]
  conduct = 2
  density = 1
  expand = 3
  formula = G4_MAGNESIUM_CARBONATE
  name = G4_MAGNESIUM_CARBONATE
  specific = 4
FEATURE [App::DocumentObjectGroupPython] Mg_element006  label="Mg_element : 002"  # scripted group (container) (typed FeaturePython)
  n = 1
  ref = Mg_element
FEATURE [App::DocumentObjectGroupPython] F_element013  label="F_element : 005"  # scripted group (container) (typed FeaturePython)
  n = 2
  ref = F_element
FEATURE [App::DocumentObjectGroupPython] G4_MAGNESIUM_FLUORIDE  # scripted group (container) (typed FeaturePython)
  Dunit = g/cm3
  Dvalue = 3
  Group = -> [Mg_element006,F_element013]
  conduct = 2
  density = 1
  expand = 3
  formula = G4_MAGNESIUM_FLUORIDE
  name = G4_MAGNESIUM_FLUORIDE
  specific = 4
FEATURE [App::DocumentObjectGroupPython] Mg_element007  label="Mg_element : 003"  # scripted group (container) (typed FeaturePython)
  n = 1
  ref = Mg_element
FEATURE [App::DocumentObjectGroupPython] O_element060  label="O_element : 031"  # scripted group (container) (typed FeaturePython)
  n = 1
  ref = O_element
FEATURE [App::DocumentObjectGroupPython] G4_MAGNESIUM_OXIDE  # scripted group (container) (typed FeaturePython)
  Dunit = g/cm3
  Dvalue = 3.58
  Group = -> [Mg_element007,O_element060]
  conduct = 2
  density = 1
  expand = 3
  formula = G4_MAGNESIUM_OXIDE
  name = G4_MAGNESIUM_OXIDE
  specific = 4
FEATURE [App::DocumentObjectGroupPython] Mg_element008  label="Mg_element : 004"  # scripted group (container) (typed FeaturePython)
  n = 1
  ref = Mg_element
FEATURE [App::DocumentObjectGroupPython] B_element006  label="B_element : 006"  # scripted group (container) (typed FeaturePython)
  n = 4
  ref = B_element
FEATURE [App::DocumentObjectGroupPython] O_element061  label="O_element : 032"  # scripted group (container) (typed FeaturePython)
  n = 7
  ref = O_element
FEATURE [App::DocumentObjectGroupPython] G4_MAGNESIUM_TETRABORATE  # scripted group (container) (typed FeaturePython)
  Dunit = g/cm3
  Dvalue = 2.53
  Group = -> [Mg_element008,B_element006,O_element061]
  conduct = 2
  density = 1
  expand = 3
  formula = G4_MAGNESIUM_TETRABORATE
  name = G4_MAGNESIUM_TETRABORATE
  specific = 4
FEATURE [App::DocumentObjectGroupPython] Hg_element001  label="Hg_element : 1"  # scripted group (container) (typed FeaturePython)
  n = 1
  ref = Hg_element
FEATURE [App::DocumentObjectGroupPython] I_element004  label="I_element : 2"  # scripted group (container) (typed FeaturePython)
  n = 2
  ref = I_element
FEATURE [App::DocumentObjectGroupPython] G4_MERCURIC_IODIDE  # scripted group (container) (typed FeaturePython)
  Dunit = g/cm3
  Dvalue = 6.36
  Group = -> [Hg_element001,I_element004]
  conduct = 2
  density = 1
  expand = 3
  formula = G4_MERCURIC_IODIDE
  name = G4_MERCURIC_IODIDE
  specific = 4
FEATURE [App::DocumentObjectGroupPython] C_element059  label="C_element : 032"  # scripted group (container) (typed FeaturePython)
  n = 1
  ref = C_element
FEATURE [App::DocumentObjectGroupPython] H_element053  label="H_element : 028"  # scripted group (container) (typed FeaturePython)
  n = 4
  ref = H_element
FEATURE [App::DocumentObjectGroupPython] G4_METHANE  # scripted group (container) (typed FeaturePython)
  Dunit = g/cm3
  Dvalue = 0.000667151
  Group = -> [C_element059,H_element053]
  conduct = 2
  density = 1
  expand = 3
  formula = G4_METHANE
  name = G4_METHANE
  specific = 4
FEATURE [App::DocumentObjectGroupPython] C_element060  label="C_element : 033"  # scripted group (container) (typed FeaturePython)
  n = 1
  ref = C_element
FEATURE [App::DocumentObjectGroupPython] H_element054  label="H_element : 029"  # scripted group (container) (typed FeaturePython)
  n = 4
  ref = H_element
FEATURE [App::DocumentObjectGroupPython] O_element062  label="O_element : 033"  # scripted group (container) (typed FeaturePython)
  n = 1
  ref = O_element
FEATURE [App::DocumentObjectGroupPython] G4_METHANOL  # scripted group (container) (typed FeaturePython)
  Dunit = g/cm3
  Dvalue = 0.7914
  Group = -> [C_element060,H_element054,O_element062]
  conduct = 2
  density = 1
  expand = 3
  formula = G4_METHANOL
  name = G4_METHANOL
  specific = 4
FEATURE [App::DocumentObjectGroupPython] H_element055  label="H_element : 0.134"  # scripted group (container) (typed FeaturePython)
  n = 0.13404
FEATURE [App::DocumentObjectGroupPython] C_element061  label="C_element : 0.778"  # scripted group (container) (typed FeaturePython)
  n = 0.77796
FEATURE [App::DocumentObjectGroupPython] O_element063  label="O_element : 0.035"  # scripted group (container) (typed FeaturePython)
  n = 0.03502
FEATURE [App::DocumentObjectGroupPython] Mg_element009  label="Mg_element : 0.039"  # scripted group (container) (typed FeaturePython)
  n = 0.038594
FEATURE [App::DocumentObjectGroupPython] Ti_element002  label="Ti_element : 0.014"  # scripted group (container) (typed FeaturePython)
  n = 0.014386
FEATURE [App::DocumentObjectGroupPython] G4_MIX_D_WAX  # scripted group (container) (typed FeaturePython)
  Dunit = g/cm3
  Dvalue = 0.99
  Group = -> [H_element055,C_element061,O_element063,Mg_element009,Ti_element002]
  conduct = 2
  density = 1
  expand = 3
  formula = G4_MIX_D_WAX
  name = G4_MIX_D_WAX
  specific = 4
FEATURE [App::DocumentObjectGroupPython] H_element056  label="H_element : 0.135"  # scripted group (container) (typed FeaturePython)
  n = 0.081192
FEATURE [App::DocumentObjectGroupPython] C_element062  label="C_element : 0.583"  # scripted group (container) (typed FeaturePython)
  n = 0.583442
FEATURE [App::DocumentObjectGroupPython] N_element024  label="N_element : 0.018"  # scripted group (container) (typed FeaturePython)
  n = 0.017798
FEATURE [App::DocumentObjectGroupPython] O_element064  label="O_element : 0.186"  # scripted group (container) (typed FeaturePython)
  n = 0.186381
FEATURE [App::DocumentObjectGroupPython] Mg_element010  label="Mg_element : 0.130"  # scripted group (container) (typed FeaturePython)
  n = 0.130287
FEATURE [App::DocumentObjectGroupPython] Cl_element015  label="Cl_element : 0.588"  # scripted group (container) (typed FeaturePython)
  n = 0.0009
FEATURE [App::DocumentObjectGroupPython] G4_MS20_TISSUE  # scripted group (container) (typed FeaturePython)
  Dunit = g/cm3
  Dvalue = 1
  Group = -> [H_element056,C_element062,N_element024,O_element064,Mg_element010,Cl_element015]
  conduct = 2
  density = 1
  expand = 3
  formula = G4_MS20_TISSUE
  name = G4_MS20_TISSUE
  specific = 4
FEATURE [App::DocumentObjectGroupPython] H_element057  label="H_element : 0.136"  # scripted group (container) (typed FeaturePython)
  n = 0.102
FEATURE [App::DocumentObjectGroupPython] C_element063  label="C_element : 0.143"  # scripted group (container) (typed FeaturePython)
  n = 0.143
FEATURE [App::DocumentObjectGroupPython] N_element025  label="N_element : 0.034"  # scripted group (container) (typed FeaturePython)
  n = 0.034
FEATURE [App::DocumentObjectGroupPython] O_element065  label="O_element : 0.710"  # scripted group (container) (typed FeaturePython)
  n = 0.71
FEATURE [App::DocumentObjectGroupPython] Na_element011  label="Na_element : 0.098"  # scripted group (container) (typed FeaturePython)
  n = 0.001
FEATURE [App::DocumentObjectGroupPython] P_element007  label="P_element : 0.002"  # scripted group (container) (typed FeaturePython)
  n = 0.002
FEATURE [App::DocumentObjectGroupPython] S_element017  label="S_element : 0.018"  # scripted group (container) (typed FeaturePython)
  n = 0.003
FEATURE [App::DocumentObjectGroupPython] Cl_element016  label="Cl_element : 0.589"  # scripted group (container) (typed FeaturePython)
  n = 0.001
FEATURE [App::DocumentObjectGroupPython] K_element006  label="K_element : 0.004"  # scripted group (container) (typed FeaturePython)
  n = 0.004
FEATURE [App::DocumentObjectGroupPython] G4_MUSCLE_SKELETAL_ICRP  # scripted group (container) (typed FeaturePython)
  Dunit = g/cm3
  Dvalue = 1.05
  Group = -> [H_element057,C_element063,N_element025,O_element065,Na_element011,P_element007,S_element017,Cl_element016,K_element006]
  conduct = 2
  density = 1
  expand = 3
  formula = G4_MUSCLE_SKELETAL_ICRP
  name = G4_MUSCLE_SKELETAL_ICRP
  specific = 4
FEATURE [App::DocumentObjectGroupPython] H_element058  label="H_element : 0.137"  # scripted group (container) (typed FeaturePython)
  n = 0.102102
FEATURE [App::DocumentObjectGroupPython] C_element064  label="C_element : 0.123"  # scripted group (container) (typed FeaturePython)
  n = 0.123123
FEATURE [App::DocumentObjectGroupPython] N_element026  label="N_element : 0.756"  # scripted group (container) (typed FeaturePython)
  n = 0.035035
FEATURE [App::DocumentObjectGroupPython] O_element066  label="O_element : 0.730"  # scripted group (container) (typed FeaturePython)
  n = 0.72973
FEATURE [App::DocumentObjectGroupPython] Na_element012  label="Na_element : 0.099"  # scripted group (container) (typed FeaturePython)
  n = 0.001001
FEATURE [App::DocumentObjectGroupPython] P_element008  label="P_element : 0.106"  # scripted group (container) (typed FeaturePython)
  n = 0.002002
FEATURE [App::DocumentObjectGroupPython] S_element018  label="S_element : 0.019"  # scripted group (container) (typed FeaturePython)
  n = 0.004004
FEATURE [App::DocumentObjectGroupPython] K_element007  label="K_element : 0.016"  # scripted group (container) (typed FeaturePython)
  n = 0.003003
FEATURE [App::DocumentObjectGroupPython] G4_MUSCLE_STRIATED_ICRU  # scripted group (container) (typed FeaturePython)
  Dunit = g/cm3
  Dvalue = 1.04
  Group = -> [H_element058,C_element064,N_element026,O_element066,Na_element012,P_element008,S_element018,K_element007]
  conduct = 2
  density = 1
  expand = 3
  formula = G4_MUSCLE_STRIATED_ICRU
  name = G4_MUSCLE_STRIATED_ICRU
  specific = 4
FEATURE [App::DocumentObjectGroupPython] H_element059  label="H_element : 0.098"  # scripted group (container) (typed FeaturePython)
  n = 0.0982341
FEATURE [App::DocumentObjectGroupPython] C_element065  label="C_element : 0.156"  # scripted group (container) (typed FeaturePython)
  n = 0.156214
FEATURE [App::DocumentObjectGroupPython] N_element027  label="N_element : 0.757"  # scripted group (container) (typed FeaturePython)
  n = 0.035451
FEATURE [App::DocumentObjectGroupPython] O_element067  label="O_element : 0.880"  # scripted group (container) (typed FeaturePython)
  n = 0.710101
FEATURE [App::DocumentObjectGroupPython] G4_MUSCLE_WITH_SUCROSE  # scripted group (container) (typed FeaturePython)
  Dunit = g/cm3
  Dvalue = 1.11
  Group = -> [H_element059,C_element065,N_element027,O_element067]
  conduct = 2
  density = 1
  expand = 3
  formula = G4_MUSCLE_WITH_SUCROSE
  name = G4_MUSCLE_WITH_SUCROSE
  specific = 4
FEATURE [App::DocumentObjectGroupPython] H_element060  label="H_element : 0.138"  # scripted group (container) (typed FeaturePython)
  n = 0.101969
FEATURE [App::DocumentObjectGroupPython] C_element066  label="C_element : 0.120"  # scripted group (container) (typed FeaturePython)
  n = 0.120058
FEATURE [App::DocumentObjectGroupPython] N_element028  label="N_element : 0.758"  # scripted group (container) (typed FeaturePython)
  n = 0.035451
FEATURE [App::DocumentObjectGroupPython] O_element068  label="O_element : 0.743"  # scripted group (container) (typed FeaturePython)
  n = 0.742522
FEATURE [App::DocumentObjectGroupPython] G4_MUSCLE_WITHOUT_SUCROSE  # scripted group (container) (typed FeaturePython)
  Dunit = g/cm3
  Dvalue = 1.07
  Group = -> [H_element060,C_element066,N_element028,O_element068]
  conduct = 2
  density = 1
  expand = 3
  formula = G4_MUSCLE_WITHOUT_SUCROSE
  name = G4_MUSCLE_WITHOUT_SUCROSE
  specific = 4
FEATURE [App::DocumentObjectGroupPython] C_element067  label="C_element : 10"  # scripted group (container) (typed FeaturePython)
  n = 10
  ref = C_element
FEATURE [App::DocumentObjectGroupPython] H_element061  label="H_element : 030"  # scripted group (container) (typed FeaturePython)
  n = 8
  ref = H_element
FEATURE [App::DocumentObjectGroupPython] G4_NAPHTHALENE  # scripted group (container) (typed FeaturePython)
  Dunit = g/cm3
  Dvalue = 1.145
  Group = -> [C_element067,H_element061]
  conduct = 2
  density = 1
  expand = 3
  formula = G4_NAPHTHALENE
  name = G4_NAPHTHALENE
  specific = 4
FEATURE [App::DocumentObjectGroupPython] C_element068  label="C_element : 034"  # scripted group (container) (typed FeaturePython)
  n = 6
  ref = C_element
FEATURE [App::DocumentObjectGroupPython] H_element062  label="H_element : 031"  # scripted group (container) (typed FeaturePython)
  n = 5
  ref = H_element
FEATURE [App::DocumentObjectGroupPython] N_element029  label="N_element : 012"  # scripted group (container) (typed FeaturePython)
  n = 1
  ref = N_element
FEATURE [App::DocumentObjectGroupPython] O_element069  label="O_element : 034"  # scripted group (container) (typed FeaturePython)
  n = 2
  ref = O_element
FEATURE [App::DocumentObjectGroupPython] G4_NITROBENZENE  # scripted group (container) (typed FeaturePython)
  Dunit = g/cm3
  Dvalue = 1.19867
  Group = -> [C_element068,H_element062,N_element029,O_element069]
  conduct = 2
  density = 1
  expand = 3
  formula = G4_NITROBENZENE
  name = G4_NITROBENZENE
  specific = 4
FEATURE [App::DocumentObjectGroupPython] N_element030  label="N_element : 013"  # scripted group (container) (typed FeaturePython)
  n = 2
  ref = N_element
FEATURE [App::DocumentObjectGroupPython] O_element070  label="O_element : 035"  # scripted group (container) (typed FeaturePython)
  n = 1
  ref = O_element
FEATURE [App::DocumentObjectGroupPython] G4_NITROUS_OXIDE  # scripted group (container) (typed FeaturePython)
  Dunit = g/cm3
  Dvalue = 0.00183094
  Group = -> [N_element030,O_element070]
  conduct = 2
  density = 1
  expand = 3
  formula = G4_NITROUS_OXIDE
  name = G4_NITROUS_OXIDE
  specific = 4
FEATURE [App::DocumentObjectGroupPython] H_element063  label="H_element : 0.104"  # scripted group (container) (typed FeaturePython)
  n = 0.103509
FEATURE [App::DocumentObjectGroupPython] C_element069  label="C_element : 0.648"  # scripted group (container) (typed FeaturePython)
  n = 0.648416
FEATURE [App::DocumentObjectGroupPython] N_element031  label="N_element : 0.100"  # scripted group (container) (typed FeaturePython)
  n = 0.0995361
FEATURE [App::DocumentObjectGroupPython] O_element071  label="O_element : 0.149"  # scripted group (container) (typed FeaturePython)
  n = 0.148539
FEATURE [App::DocumentObjectGroupPython] G4_NYLON_8062  label="G4_NYLON-8062"  # scripted group (container) (typed FeaturePython)
  Dunit = g/cm3
  Dvalue = 1.08
  Group = -> [H_element063,C_element069,N_element031,O_element071]
  conduct = 2
  density = 1
  expand = 3
  formula = G4_NYLON-8062
  name = G4_NYLON-8062
  specific = 4
FEATURE [App::DocumentObjectGroupPython] C_element070  label="C_element : 035"  # scripted group (container) (typed FeaturePython)
  n = 6
  ref = C_element
FEATURE [App::DocumentObjectGroupPython] H_element064  label="H_element : 11"  # scripted group (container) (typed FeaturePython)
  n = 11
  ref = H_element
FEATURE [App::DocumentObjectGroupPython] N_element032  label="N_element : 014"  # scripted group (container) (typed FeaturePython)
  n = 1
  ref = N_element
FEATURE [App::DocumentObjectGroupPython] O_element072  label="O_element : 036"  # scripted group (container) (typed FeaturePython)
  n = 1
  ref = O_element
FEATURE [App::DocumentObjectGroupPython] G4_NYLON_6_6  label="G4_NYLON-6-6"  # scripted group (container) (typed FeaturePython)
  Dunit = g/cm3
  Dvalue = 1.14
  Group = -> [C_element070,H_element064,N_element032,O_element072]
  conduct = 2
  density = 1
  expand = 3
  formula = G4_NYLON-6-6
  name = G4_NYLON-6-6
  specific = 4
FEATURE [App::DocumentObjectGroupPython] H_element065  label="H_element : 0.139"  # scripted group (container) (typed FeaturePython)
  n = 0.107062
FEATURE [App::DocumentObjectGroupPython] C_element071  label="C_element : 0.680"  # scripted group (container) (typed FeaturePython)
  n = 0.680449
FEATURE [App::DocumentObjectGroupPython] N_element033  label="N_element : 0.099"  # scripted group (container) (typed FeaturePython)
  n = 0.099189
FEATURE [App::DocumentObjectGroupPython] O_element073  label="O_element : 0.113"  # scripted group (container) (typed FeaturePython)
  n = 0.1133
FEATURE [App::DocumentObjectGroupPython] G4_NYLON_6_10  label="G4_NYLON-6-10"  # scripted group (container) (typed FeaturePython)
  Dunit = g/cm3
  Dvalue = 1.14
  Group = -> [H_element065,C_element071,N_element033,O_element073]
  conduct = 2
  density = 1
  expand = 3
  formula = G4_NYLON-6-10
  name = G4_NYLON-6-10
  specific = 4
FEATURE [App::DocumentObjectGroupPython] H_element066  label="H_element : 0.140"  # scripted group (container) (typed FeaturePython)
  n = 0.115476
FEATURE [App::DocumentObjectGroupPython] C_element072  label="C_element : 0.721"  # scripted group (container) (typed FeaturePython)
  n = 0.720818
FEATURE [App::DocumentObjectGroupPython] N_element034  label="N_element : 0.076"  # scripted group (container) (typed FeaturePython)
  n = 0.0764169
FEATURE [App::DocumentObjectGroupPython] O_element074  label="O_element : 0.087"  # scripted group (container) (typed FeaturePython)
  n = 0.0872889
FEATURE [App::DocumentObjectGroupPython] G4_NYLON_11_RILSAN  label="G4_NYLON-11_RILSAN"  # scripted group (container) (typed FeaturePython)
  Dunit = g/cm3
  Dvalue = 1.425
  Group = -> [H_element066,C_element072,N_element034,O_element074]
  conduct = 2
  density = 1
  expand = 3
  formula = G4_NYLON-11_RILSAN
  name = G4_NYLON-11_RILSAN
  specific = 4
FEATURE [App::DocumentObjectGroupPython] C_element073  label="C_element : 8"  # scripted group (container) (typed FeaturePython)
  n = 8
  ref = C_element
FEATURE [App::DocumentObjectGroupPython] H_element067  label="H_element : 18"  # scripted group (container) (typed FeaturePython)
  n = 18
  ref = H_element
FEATURE [App::DocumentObjectGroupPython] G4_OCTANE  # scripted group (container) (typed FeaturePython)
  Dunit = g/cm3
  Dvalue = 0.7026
  Group = -> [C_element073,H_element067]
  conduct = 2
  density = 1
  expand = 3
  formula = G4_OCTANE
  name = G4_OCTANE
  specific = 4
FEATURE [App::DocumentObjectGroupPython] C_element074  label="C_element : 25"  # scripted group (container) (typed FeaturePython)
  n = 25
  ref = C_element
FEATURE [App::DocumentObjectGroupPython] H_element068  label="H_element : 52"  # scripted group (container) (typed FeaturePython)
  n = 52
  ref = H_element
FEATURE [App::DocumentObjectGroupPython] G4_PARAFFIN  # scripted group (container) (typed FeaturePython)
  Dunit = g/cm3
  Dvalue = 0.93
  Group = -> [C_element074,H_element068]
  conduct = 2
  density = 1
  expand = 3
  formula = G4_PARAFFIN
  name = G4_PARAFFIN
  specific = 4
FEATURE [App::DocumentObjectGroupPython] C_element075  label="C_element : 036"  # scripted group (container) (typed FeaturePython)
  n = 5
  ref = C_element
FEATURE [App::DocumentObjectGroupPython] H_element069  label="H_element : 032"  # scripted group (container) (typed FeaturePython)
  n = 12
  ref = H_element
FEATURE [App::DocumentObjectGroupPython] G4_N_PENTANE  label="G4_N-PENTANE"  # scripted group (container) (typed FeaturePython)
  Dunit = g/cm3
  Dvalue = 0.6262
  Group = -> [C_element075,H_element069]
  conduct = 2
  density = 1
  expand = 3
  formula = G4_N-PENTANE
  name = G4_N-PENTANE
  specific = 4
FEATURE [App::DocumentObjectGroupPython] H_element070  label="H_element : 0.014"  # scripted group (container) (typed FeaturePython)
  n = 0.0141
FEATURE [App::DocumentObjectGroupPython] C_element076  label="C_element : 0.072"  # scripted group (container) (typed FeaturePython)
  n = 0.072261
FEATURE [App::DocumentObjectGroupPython] N_element035  label="N_element : 0.019"  # scripted group (container) (typed FeaturePython)
  n = 0.01932
FEATURE [App::DocumentObjectGroupPython] O_element075  label="O_element : 0.066"  # scripted group (container) (typed FeaturePython)
  n = 0.066101
FEATURE [App::DocumentObjectGroupPython] S_element019  label="S_element : 0.020"  # scripted group (container) (typed FeaturePython)
  n = 0.00189
FEATURE [App::DocumentObjectGroupPython] Br_element004  label="Br_element : 0.349"  # scripted group (container) (typed FeaturePython)
  n = 0.349103
FEATURE [App::DocumentObjectGroupPython] Ag_element001  label="Ag_element : 0.474"  # scripted group (container) (typed FeaturePython)
  n = 0.474105
FEATURE [App::DocumentObjectGroupPython] I_element005  label="I_element : 0.003"  # scripted group (container) (typed FeaturePython)
  n = 0.00312
FEATURE [App::DocumentObjectGroupPython] G4_PHOTO_EMULSION  # scripted group (container) (typed FeaturePython)
  Dunit = g/cm3
  Dvalue = 3.815
  Group = -> [H_element070,C_element076,N_element035,O_element075,S_element019,Br_element004,Ag_element001,I_element005]
  conduct = 2
  density = 1
  expand = 3
  formula = G4_PHOTO_EMULSION
  name = G4_PHOTO_EMULSION
  specific = 4
FEATURE [App::DocumentObjectGroupPython] C_element077  label="C_element : 9"  # scripted group (container) (typed FeaturePython)
  n = 9
  ref = C_element
FEATURE [App::DocumentObjectGroupPython] H_element071  label="H_element : 033"  # scripted group (container) (typed FeaturePython)
  n = 10
  ref = H_element
FEATURE [App::DocumentObjectGroupPython] G4_PLASTIC_SC_VINYLTOLUENE  # scripted group (container) (typed FeaturePython)
  Dunit = g/cm3
  Dvalue = 1.032
  Group = -> [C_element077,H_element071]
  conduct = 2
  density = 1
  expand = 3
  formula = G4_PLASTIC_SC_VINYLTOLUENE
  name = G4_PLASTIC_SC_VINYLTOLUENE
  specific = 4
FEATURE [App::DocumentObjectGroupPython] Pu_element001  label="Pu_element : 1"  # scripted group (container) (typed FeaturePython)
  n = 1
  ref = Pu_element
FEATURE [App::DocumentObjectGroupPython] O_element076  label="O_element : 037"  # scripted group (container) (typed FeaturePython)
  n = 2
  ref = O_element
FEATURE [App::DocumentObjectGroupPython] G4_PLUTONIUM_DIOXIDE  # scripted group (container) (typed FeaturePython)
  Dunit = g/cm3
  Dvalue = 11.46
  Group = -> [Pu_element001,O_element076]
  conduct = 2
  density = 1
  expand = 3
  formula = G4_PLUTONIUM_DIOXIDE
  name = G4_PLUTONIUM_DIOXIDE
  specific = 4
FEATURE [App::DocumentObjectGroupPython] C_element078  label="C_element : 037"  # scripted group (container) (typed FeaturePython)
  n = 3
  ref = C_element
FEATURE [App::DocumentObjectGroupPython] H_element072  label="H_element : 034"  # scripted group (container) (typed FeaturePython)
  n = 3
  ref = H_element
FEATURE [App::DocumentObjectGroupPython] N_element036  label="N_element : 015"  # scripted group (container) (typed FeaturePython)
  n = 1
  ref = N_element
FEATURE [App::DocumentObjectGroupPython] G4_POLYACRYLONITRILE  # scripted group (container) (typed FeaturePython)
  Dunit = g/cm3
  Dvalue = 1.17
  Group = -> [C_element078,H_element072,N_element036]
  conduct = 2
  density = 1
  expand = 3
  formula = G4_POLYACRYLONITRILE
  name = G4_POLYACRYLONITRILE
  specific = 4
FEATURE [App::DocumentObjectGroupPython] C_element079  label="C_element : 16"  # scripted group (container) (typed FeaturePython)
  n = 16
  ref = C_element
FEATURE [App::DocumentObjectGroupPython] H_element073  label="H_element : 035"  # scripted group (container) (typed FeaturePython)
  n = 14
  ref = H_element
FEATURE [App::DocumentObjectGroupPython] O_element077  label="O_element : 038"  # scripted group (container) (typed FeaturePython)
  n = 3
  ref = O_element
FEATURE [App::DocumentObjectGroupPython] G4_POLYCARBONATE  # scripted group (container) (typed FeaturePython)
  Dunit = g/cm3
  Dvalue = 1.2
  Group = -> [C_element079,H_element073,O_element077]
  conduct = 2
  density = 1
  expand = 3
  formula = G4_POLYCARBONATE
  name = G4_POLYCARBONATE
  specific = 4
FEATURE [App::DocumentObjectGroupPython] C_element080  label="C_element : 038"  # scripted group (container) (typed FeaturePython)
  n = 8
  ref = C_element
FEATURE [App::DocumentObjectGroupPython] H_element074  label="H_element : 036"  # scripted group (container) (typed FeaturePython)
  n = 7
  ref = H_element
FEATURE [App::DocumentObjectGroupPython] Cl_element017  label="Cl_element : 007"  # scripted group (container) (typed FeaturePython)
  n = 1
  ref = Cl_element
FEATURE [App::DocumentObjectGroupPython] G4_POLYCHLOROSTYRENE  # scripted group (container) (typed FeaturePython)
  Dunit = g/cm3
  Dvalue = 1.3
  Group = -> [C_element080,H_element074,Cl_element017]
  conduct = 2
  density = 1
  expand = 3
  formula = G4_POLYCHLOROSTYRENE
  name = G4_POLYCHLOROSTYRENE
  specific = 4
FEATURE [App::DocumentObjectGroupPython] C_element081  label="C_element : 039"  # scripted group (container) (typed FeaturePython)
  n = 1
  ref = C_element
FEATURE [App::DocumentObjectGroupPython] H_element075  label="H_element : 037"  # scripted group (container) (typed FeaturePython)
  n = 2
  ref = H_element
FEATURE [App::DocumentObjectGroupPython] G4_POLYETHYLENE  # scripted group (container) (typed FeaturePython)
  Dunit = g/cm3
  Dvalue = 0.94
  Group = -> [C_element081,H_element075]
  conduct = 2
  density = 1
  expand = 3
  formula = G4_POLYETHYLENE
  name = G4_POLYETHYLENE
  specific = 4
FEATURE [App::DocumentObjectGroupPython] C_element082  label="C_element : 040"  # scripted group (container) (typed FeaturePython)
  n = 10
  ref = C_element
FEATURE [App::DocumentObjectGroupPython] H_element076  label="H_element : 038"  # scripted group (container) (typed FeaturePython)
  n = 8
  ref = H_element
FEATURE [App::DocumentObjectGroupPython] O_element078  label="O_element : 039"  # scripted group (container) (typed FeaturePython)
  n = 4
  ref = O_element
FEATURE [App::DocumentObjectGroupPython] G4_MYLAR  # scripted group (container) (typed FeaturePython)
  Dunit = g/cm3
  Dvalue = 1.4
  Group = -> [C_element082,H_element076,O_element078]
  conduct = 2
  density = 1
  expand = 3
  formula = G4_MYLAR
  name = G4_MYLAR
  specific = 4
FEATURE [App::DocumentObjectGroupPython] C_element083  label="C_element : 041"  # scripted group (container) (typed FeaturePython)
  n = 5
  ref = C_element
FEATURE [App::DocumentObjectGroupPython] H_element077  label="H_element : 039"  # scripted group (container) (typed FeaturePython)
  n = 8
  ref = H_element
FEATURE [App::DocumentObjectGroupPython] O_element079  label="O_element : 040"  # scripted group (container) (typed FeaturePython)
  n = 2
  ref = O_element
FEATURE [App::DocumentObjectGroupPython] G4_PLEXIGLASS  # scripted group (container) (typed FeaturePython)
  Dunit = g/cm3
  Dvalue = 1.19
  Group = -> [C_element083,H_element077,O_element079]
  conduct = 2
  density = 1
  expand = 3
  formula = G4_PLEXIGLASS
  name = G4_PLEXIGLASS
  specific = 4
FEATURE [App::DocumentObjectGroupPython] C_element084  label="C_element : 042"  # scripted group (container) (typed FeaturePython)
  n = 1
  ref = C_element
FEATURE [App::DocumentObjectGroupPython] H_element078  label="H_element : 040"  # scripted group (container) (typed FeaturePython)
  n = 2
  ref = H_element
FEATURE [App::DocumentObjectGroupPython] O_element080  label="O_element : 041"  # scripted group (container) (typed FeaturePython)
  n = 1
  ref = O_element
FEATURE [App::DocumentObjectGroupPython] G4_POLYOXYMETHYLENE  # scripted group (container) (typed FeaturePython)
  Dunit = g/cm3
  Dvalue = 1.425
  Group = -> [C_element084,H_element078,O_element080]
  conduct = 2
  density = 1
  expand = 3
  formula = G4_POLYOXYMETHYLENE
  name = G4_POLYOXYMETHYLENE
  specific = 4
FEATURE [App::DocumentObjectGroupPython] C_element085  label="C_element : 043"  # scripted group (container) (typed FeaturePython)
  n = 2
  ref = C_element
FEATURE [App::DocumentObjectGroupPython] H_element079  label="H_element : 041"  # scripted group (container) (typed FeaturePython)
  n = 4
  ref = H_element
FEATURE [App::DocumentObjectGroupPython] G4_POLYPROPYLENE  # scripted group (container) (typed FeaturePython)
  Dunit = g/cm3
  Dvalue = 0.9
  Group = -> [C_element085,H_element079]
  conduct = 2
  density = 1
  expand = 3
  formula = G4_POLYPROPYLENE
  name = G4_POLYPROPYLENE
  specific = 4
FEATURE [App::DocumentObjectGroupPython] C_element086  label="C_element : 044"  # scripted group (container) (typed FeaturePython)
  n = 8
  ref = C_element
FEATURE [App::DocumentObjectGroupPython] H_element080  label="H_element : 042"  # scripted group (container) (typed FeaturePython)
  n = 8
  ref = H_element
FEATURE [App::DocumentObjectGroupPython] G4_POLYSTYRENE  # scripted group (container) (typed FeaturePython)
  Dunit = g/cm3
  Dvalue = 1.06
  Group = -> [C_element086,H_element080]
  conduct = 2
  density = 1
  expand = 3
  formula = G4_POLYSTYRENE
  name = G4_POLYSTYRENE
  specific = 4
FEATURE [App::DocumentObjectGroupPython] C_element087  label="C_element : 045"  # scripted group (container) (typed FeaturePython)
  n = 2
  ref = C_element
FEATURE [App::DocumentObjectGroupPython] F_element014  label="F_element : 4"  # scripted group (container) (typed FeaturePython)
  n = 4
  ref = F_element
FEATURE [App::DocumentObjectGroupPython] G4_TEFLON  # scripted group (container) (typed FeaturePython)
  Dunit = g/cm3
  Dvalue = 2.2
  Group = -> [C_element087,F_element014]
  conduct = 2
  density = 1
  expand = 3
  formula = G4_TEFLON
  name = G4_TEFLON
  specific = 4
FEATURE [App::DocumentObjectGroupPython] C_element088  label="C_element : 046"  # scripted group (container) (typed FeaturePython)
  n = 2
  ref = C_element
FEATURE [App::DocumentObjectGroupPython] F_element015  label="F_element : 006"  # scripted group (container) (typed FeaturePython)
  n = 3
  ref = F_element
FEATURE [App::DocumentObjectGroupPython] Cl_element018  label="Cl_element : 008"  # scripted group (container) (typed FeaturePython)
  n = 1
  ref = Cl_element
FEATURE [App::DocumentObjectGroupPython] G4_POLYTRIFLUOROCHLOROETHYLENE  # scripted group (container) (typed FeaturePython)
  Dunit = g/cm3
  Dvalue = 2.1
  Group = -> [C_element088,F_element015,Cl_element018]
  conduct = 2
  density = 1
  expand = 3
  formula = G4_POLYTRIFLUOROCHLOROETHYLENE
  name = G4_POLYTRIFLUOROCHLOROETHYLENE
  specific = 4
FEATURE [App::DocumentObjectGroupPython] C_element089  label="C_element : 047"  # scripted group (container) (typed FeaturePython)
  n = 4
  ref = C_element
FEATURE [App::DocumentObjectGroupPython] H_element081  label="H_element : 043"  # scripted group (container) (typed FeaturePython)
  n = 6
  ref = H_element
FEATURE [App::DocumentObjectGroupPython] O_element081  label="O_element : 042"  # scripted group (container) (typed FeaturePython)
  n = 2
  ref = O_element
FEATURE [App::DocumentObjectGroupPython] G4_POLYVINYL_ACETATE  # scripted group (container) (typed FeaturePython)
  Dunit = g/cm3
  Dvalue = 1.19
  Group = -> [C_element089,H_element081,O_element081]
  conduct = 2
  density = 1
  expand = 3
  formula = G4_POLYVINYL_ACETATE
  name = G4_POLYVINYL_ACETATE
  specific = 4
FEATURE [App::DocumentObjectGroupPython] C_element090  label="C_element : 048"  # scripted group (container) (typed FeaturePython)
  n = 2
  ref = C_element
FEATURE [App::DocumentObjectGroupPython] H_element082  label="H_element : 044"  # scripted group (container) (typed FeaturePython)
  n = 4
  ref = H_element
FEATURE [App::DocumentObjectGroupPython] O_element082  label="O_element : 043"  # scripted group (container) (typed FeaturePython)
  n = 1
  ref = O_element
FEATURE [App::DocumentObjectGroupPython] G4_POLYVINYL_ALCOHOL  # scripted group (container) (typed FeaturePython)
  Dunit = g/cm3
  Dvalue = 1.3
  Group = -> [C_element090,H_element082,O_element082]
  conduct = 2
  density = 1
  expand = 3
  formula = G4_POLYVINYL_ALCOHOL
  name = G4_POLYVINYL_ALCOHOL
  specific = 4
FEATURE [App::DocumentObjectGroupPython] C_element091  label="C_element : 049"  # scripted group (container) (typed FeaturePython)
  n = 8
  ref = C_element
FEATURE [App::DocumentObjectGroupPython] H_element083  label="H_element : 045"  # scripted group (container) (typed FeaturePython)
  n = 14
  ref = H_element
FEATURE [App::DocumentObjectGroupPython] O_element083  label="O_element : 044"  # scripted group (container) (typed FeaturePython)
  n = 2
  ref = O_element
FEATURE [App::DocumentObjectGroupPython] G4_POLYVINYL_BUTYRAL  # scripted group (container) (typed FeaturePython)
  Dunit = g/cm3
  Dvalue = 1.12
  Group = -> [C_element091,H_element083,O_element083]
  conduct = 2
  density = 1
  expand = 3
  formula = G4_POLYVINYL_BUTYRAL
  name = G4_POLYVINYL_BUTYRAL
  specific = 4
FEATURE [App::DocumentObjectGroupPython] C_element092  label="C_element : 050"  # scripted group (container) (typed FeaturePython)
  n = 2
  ref = C_element
FEATURE [App::DocumentObjectGroupPython] H_element084  label="H_element : 046"  # scripted group (container) (typed FeaturePython)
  n = 3
  ref = H_element
FEATURE [App::DocumentObjectGroupPython] Cl_element019  label="Cl_element : 009"  # scripted group (container) (typed FeaturePython)
  n = 1
  ref = Cl_element
FEATURE [App::DocumentObjectGroupPython] G4_POLYVINYL_CHLORIDE  # scripted group (container) (typed FeaturePython)
  Dunit = g/cm3
  Dvalue = 1.3
  Group = -> [C_element092,H_element084,Cl_element019]
  conduct = 2
  density = 1
  expand = 3
  formula = G4_POLYVINYL_CHLORIDE
  name = G4_POLYVINYL_CHLORIDE
  specific = 4
FEATURE [App::DocumentObjectGroupPython] C_element093  label="C_element : 051"  # scripted group (container) (typed FeaturePython)
  n = 2
  ref = C_element
FEATURE [App::DocumentObjectGroupPython] H_element085  label="H_element : 047"  # scripted group (container) (typed FeaturePython)
  n = 2
  ref = H_element
FEATURE [App::DocumentObjectGroupPython] Cl_element020  label="Cl_element : 010"  # scripted group (container) (typed FeaturePython)
  n = 2
  ref = Cl_element
FEATURE [App::DocumentObjectGroupPython] G4_POLYVINYLIDENE_CHLORIDE  # scripted group (container) (typed FeaturePython)
  Dunit = g/cm3
  Dvalue = 1.7
  Group = -> [C_element093,H_element085,Cl_element020]
  conduct = 2
  density = 1
  expand = 3
  formula = G4_POLYVINYLIDENE_CHLORIDE
  name = G4_POLYVINYLIDENE_CHLORIDE
  specific = 4
FEATURE [App::DocumentObjectGroupPython] C_element094  label="C_element : 052"  # scripted group (container) (typed FeaturePython)
  n = 2
  ref = C_element
FEATURE [App::DocumentObjectGroupPython] H_element086  label="H_element : 048"  # scripted group (container) (typed FeaturePython)
  n = 2
  ref = H_element
FEATURE [App::DocumentObjectGroupPython] F_element016  label="F_element : 007"  # scripted group (container) (typed FeaturePython)
  n = 2
  ref = F_element
FEATURE [App::DocumentObjectGroupPython] G4_POLYVINYLIDENE_FLUORIDE  # scripted group (container) (typed FeaturePython)
  Dunit = g/cm3
  Dvalue = 1.76
  Group = -> [C_element094,H_element086,F_element016]
  conduct = 2
  density = 1
  expand = 3
  formula = G4_POLYVINYLIDENE_FLUORIDE
  name = G4_POLYVINYLIDENE_FLUORIDE
  specific = 4
FEATURE [App::DocumentObjectGroupPython] C_element095  label="C_element : 053"  # scripted group (container) (typed FeaturePython)
  n = 6
  ref = C_element
FEATURE [App::DocumentObjectGroupPython] H_element087  label="H_element : 9"  # scripted group (container) (typed FeaturePython)
  n = 9
  ref = H_element
FEATURE [App::DocumentObjectGroupPython] N_element037  label="N_element : 016"  # scripted group (container) (typed FeaturePython)
  n = 1
  ref = N_element
FEATURE [App::DocumentObjectGroupPython] O_element084  label="O_element : 045"  # scripted group (container) (typed FeaturePython)
  n = 1
  ref = O_element
FEATURE [App::DocumentObjectGroupPython] G4_POLYVINYL_PYRROLIDONE  # scripted group (container) (typed FeaturePython)
  Dunit = g/cm3
  Dvalue = 1.25
  Group = -> [C_element095,H_element087,N_element037,O_element084]
  conduct = 2
  density = 1
  expand = 3
  formula = G4_POLYVINYL_PYRROLIDONE
  name = G4_POLYVINYL_PYRROLIDONE
  specific = 4
FEATURE [App::DocumentObjectGroupPython] K_element008  label="K_element : 1"  # scripted group (container) (typed FeaturePython)
  n = 1
  ref = K_element
FEATURE [App::DocumentObjectGroupPython] I_element006  label="I_element : 003"  # scripted group (container) (typed FeaturePython)
  n = 1
  ref = I_element
FEATURE [App::DocumentObjectGroupPython] G4_POTASSIUM_IODIDE  # scripted group (container) (typed FeaturePython)
  Dunit = g/cm3
  Dvalue = 3.13
  Group = -> [K_element008,I_element006]
  conduct = 2
  density = 1
  expand = 3
  formula = G4_POTASSIUM_IODIDE
  name = G4_POTASSIUM_IODIDE
  specific = 4
FEATURE [App::DocumentObjectGroupPython] K_element009  label="K_element : 2"  # scripted group (container) (typed FeaturePython)
  n = 2
  ref = K_element
FEATURE [App::DocumentObjectGroupPython] O_element085  label="O_element : 046"  # scripted group (container) (typed FeaturePython)
  n = 1
  ref = O_element
FEATURE [App::DocumentObjectGroupPython] G4_POTASSIUM_OXIDE  # scripted group (container) (typed FeaturePython)
  Dunit = g/cm3
  Dvalue = 2.32
  Group = -> [K_element009,O_element085]
  conduct = 2
  density = 1
  expand = 3
  formula = G4_POTASSIUM_OXIDE
  name = G4_POTASSIUM_OXIDE
  specific = 4
FEATURE [App::DocumentObjectGroupPython] C_element096  label="C_element : 054"  # scripted group (container) (typed FeaturePython)
  n = 3
  ref = C_element
FEATURE [App::DocumentObjectGroupPython] H_element088  label="H_element : 049"  # scripted group (container) (typed FeaturePython)
  n = 8
  ref = H_element
FEATURE [App::DocumentObjectGroupPython] G4_PROPANE  # scripted group (container) (typed FeaturePython)
  Dunit = g/cm3
  Dvalue = 0.00187939
  Group = -> [C_element096,H_element088]
  conduct = 2
  density = 1
  expand = 3
  formula = G4_PROPANE
  name = G4_PROPANE
  specific = 4
FEATURE [App::DocumentObjectGroupPython] C_element097  label="C_element : 055"  # scripted group (container) (typed FeaturePython)
  n = 3
  ref = C_element
FEATURE [App::DocumentObjectGroupPython] H_element089  label="H_element : 050"  # scripted group (container) (typed FeaturePython)
  n = 8
  ref = H_element
FEATURE [App::DocumentObjectGroupPython] G4_lPROPANE  # scripted group (container) (typed FeaturePython)
  Dunit = g/cm3
  Dvalue = 0.43
  Group = -> [C_element097,H_element089]
  conduct = 2
  density = 1
  expand = 3
  formula = G4_lPROPANE
  name = G4_lPROPANE
  specific = 4
FEATURE [App::DocumentObjectGroupPython] C_element098  label="C_element : 056"  # scripted group (container) (typed FeaturePython)
  n = 3
  ref = C_element
FEATURE [App::DocumentObjectGroupPython] H_element090  label="H_element : 051"  # scripted group (container) (typed FeaturePython)
  n = 8
  ref = H_element
FEATURE [App::DocumentObjectGroupPython] O_element086  label="O_element : 047"  # scripted group (container) (typed FeaturePython)
  n = 1
  ref = O_element
FEATURE [App::DocumentObjectGroupPython] G4_N_PROPYL_ALCOHOL  label="G4_N-PROPYL_ALCOHOL"  # scripted group (container) (typed FeaturePython)
  Dunit = g/cm3
  Dvalue = 0.8035
  Group = -> [C_element098,H_element090,O_element086]
  conduct = 2
  density = 1
  expand = 3
  formula = G4_N-PROPYL_ALCOHOL
  name = G4_N-PROPYL_ALCOHOL
  specific = 4
FEATURE [App::DocumentObjectGroupPython] C_element099  label="C_element : 057"  # scripted group (container) (typed FeaturePython)
  n = 5
  ref = C_element
FEATURE [App::DocumentObjectGroupPython] H_element091  label="H_element : 052"  # scripted group (container) (typed FeaturePython)
  n = 5
  ref = H_element
FEATURE [App::DocumentObjectGroupPython] N_element038  label="N_element : 017"  # scripted group (container) (typed FeaturePython)
  n = 1
  ref = N_element
FEATURE [App::DocumentObjectGroupPython] G4_PYRIDINE  # scripted group (container) (typed FeaturePython)
  Dunit = g/cm3
  Dvalue = 0.9819
  Group = -> [C_element099,H_element091,N_element038]
  conduct = 2
  density = 1
  expand = 3
  formula = G4_PYRIDINE
  name = G4_PYRIDINE
  specific = 4
FEATURE [App::DocumentObjectGroupPython] H_element092  label="H_element : 0.144"  # scripted group (container) (typed FeaturePython)
  n = 0.143711
FEATURE [App::DocumentObjectGroupPython] C_element100  label="C_element : 0.856"  # scripted group (container) (typed FeaturePython)
  n = 0.856289
FEATURE [App::DocumentObjectGroupPython] G4_RUBBER_BUTYL  # scripted group (container) (typed FeaturePython)
  Dunit = g/cm3
  Dvalue = 0.92
  Group = -> [H_element092,C_element100]
  conduct = 2
  density = 1
  expand = 3
  formula = G4_RUBBER_BUTYL
  name = G4_RUBBER_BUTYL
  specific = 4
FEATURE [App::DocumentObjectGroupPython] H_element093  label="H_element : 0.118"  # scripted group (container) (typed FeaturePython)
  n = 0.118371
FEATURE [App::DocumentObjectGroupPython] C_element101  label="C_element : 0.882"  # scripted group (container) (typed FeaturePython)
  n = 0.881629
FEATURE [App::DocumentObjectGroupPython] G4_RUBBER_NATURAL  # scripted group (container) (typed FeaturePython)
  Dunit = g/cm3
  Dvalue = 0.92
  Group = -> [H_element093,C_element101]
  conduct = 2
  density = 1
  expand = 3
  formula = G4_RUBBER_NATURAL
  name = G4_RUBBER_NATURAL
  specific = 4
FEATURE [App::DocumentObjectGroupPython] H_element094  label="H_element : 0.145"  # scripted group (container) (typed FeaturePython)
  n = 0.05692
FEATURE [App::DocumentObjectGroupPython] C_element102  label="C_element : 0.543"  # scripted group (container) (typed FeaturePython)
  n = 0.542646
FEATURE [App::DocumentObjectGroupPython] Cl_element021  label="Cl_element : 0.400"  # scripted group (container) (typed FeaturePython)
  n = 0.400434
FEATURE [App::DocumentObjectGroupPython] G4_RUBBER_NEOPRENE  # scripted group (container) (typed FeaturePython)
  Dunit = g/cm3
  Dvalue = 1.23
  Group = -> [H_element094,C_element102,Cl_element021]
  conduct = 2
  density = 1
  expand = 3
  formula = G4_RUBBER_NEOPRENE
  name = G4_RUBBER_NEOPRENE
  specific = 4
FEATURE [App::DocumentObjectGroupPython] Si_element006  label="Si_element : 1"  # scripted group (container) (typed FeaturePython)
  n = 1
  ref = Si_element
FEATURE [App::DocumentObjectGroupPython] O_element087  label="O_element : 048"  # scripted group (container) (typed FeaturePython)
  n = 2
  ref = O_element
FEATURE [App::DocumentObjectGroupPython] G4_SILICON_DIOXIDE  # scripted group (container) (typed FeaturePython)
  Dunit = g/cm3
  Dvalue = 2.32
  Group = -> [Si_element006,O_element087]
  conduct = 2
  density = 1
  expand = 3
  formula = G4_SILICON_DIOXIDE
  name = G4_SILICON_DIOXIDE
  specific = 4
FEATURE [App::DocumentObjectGroupPython] Ag_element002  label="Ag_element : 1"  # scripted group (container) (typed FeaturePython)
  n = 1
  ref = Ag_element
FEATURE [App::DocumentObjectGroupPython] Br_element005  label="Br_element : 003"  # scripted group (container) (typed FeaturePython)
  n = 1
  ref = Br_element
FEATURE [App::DocumentObjectGroupPython] G4_SILVER_BROMIDE  # scripted group (container) (typed FeaturePython)
  Dunit = g/cm3
  Dvalue = 6.473
  Group = -> [Ag_element002,Br_element005]
  conduct = 2
  density = 1
  expand = 3
  formula = G4_SILVER_BROMIDE
  name = G4_SILVER_BROMIDE
  specific = 4
FEATURE [App::DocumentObjectGroupPython] Ag_element003  label="Ag_element : 002"  # scripted group (container) (typed FeaturePython)
  n = 1
  ref = Ag_element
FEATURE [App::DocumentObjectGroupPython] Cl_element022  label="Cl_element : 011"  # scripted group (container) (typed FeaturePython)
  n = 1
  ref = Cl_element
FEATURE [App::DocumentObjectGroupPython] G4_SILVER_CHLORIDE  # scripted group (container) (typed FeaturePython)
  Dunit = g/cm3
  Dvalue = 5.56
  Group = -> [Ag_element003,Cl_element022]
  conduct = 2
  density = 1
  expand = 3
  formula = G4_SILVER_CHLORIDE
  name = G4_SILVER_CHLORIDE
  specific = 4
FEATURE [App::DocumentObjectGroupPython] Br_element006  label="Br_element : 0.423"  # scripted group (container) (typed FeaturePython)
  n = 0.422895
FEATURE [App::DocumentObjectGroupPython] Ag_element004  label="Ag_element : 0.574"  # scripted group (container) (typed FeaturePython)
  n = 0.573748
FEATURE [App::DocumentObjectGroupPython] I_element007  label="I_element : 0.649"  # scripted group (container) (typed FeaturePython)
  n = 0.003357
FEATURE [App::DocumentObjectGroupPython] G4_SILVER_HALIDES  # scripted group (container) (typed FeaturePython)
  Dunit = g/cm3
  Dvalue = 6.47
  Group = -> [Br_element006,Ag_element004,I_element007]
  conduct = 2
  density = 1
  expand = 3
  formula = G4_SILVER_HALIDES
  name = G4_SILVER_HALIDES
  specific = 4
FEATURE [App::DocumentObjectGroupPython] Ag_element005  label="Ag_element : 003"  # scripted group (container) (typed FeaturePython)
  n = 1
  ref = Ag_element
FEATURE [App::DocumentObjectGroupPython] I_element008  label="I_element : 004"  # scripted group (container) (typed FeaturePython)
  n = 1
  ref = I_element
FEATURE [App::DocumentObjectGroupPython] G4_SILVER_IODIDE  # scripted group (container) (typed FeaturePython)
  Dunit = g/cm3
  Dvalue = 6.01
  Group = -> [Ag_element005,I_element008]
  conduct = 2
  density = 1
  expand = 3
  formula = G4_SILVER_IODIDE
  name = G4_SILVER_IODIDE
  specific = 4
FEATURE [App::DocumentObjectGroupPython] H_element095  label="H_element : 0.100"  # scripted group (container) (typed FeaturePython)
  n = 0.1
FEATURE [App::DocumentObjectGroupPython] C_element103  label="C_element : 0.204"  # scripted group (container) (typed FeaturePython)
  n = 0.204
FEATURE [App::DocumentObjectGroupPython] N_element039  label="N_element : 0.759"  # scripted group (container) (typed FeaturePython)
  n = 0.042
FEATURE [App::DocumentObjectGroupPython] O_element088  label="O_element : 0.645"  # scripted group (container) (typed FeaturePython)
  n = 0.645
FEATURE [App::DocumentObjectGroupPython] Na_element013  label="Na_element : 0.100"  # scripted group (container) (typed FeaturePython)
  n = 0.002
FEATURE [App::DocumentObjectGroupPython] P_element009  label="P_element : 0.107"  # scripted group (container) (typed FeaturePython)
  n = 0.001
FEATURE [App::DocumentObjectGroupPython] S_element020  label="S_element : 0.021"  # scripted group (container) (typed FeaturePython)
  n = 0.002
FEATURE [App::DocumentObjectGroupPython] Cl_element023  label="Cl_element : 0.590"  # scripted group (container) (typed FeaturePython)
  n = 0.003
FEATURE [App::DocumentObjectGroupPython] K_element010  label="K_element : 0.001"  # scripted group (container) (typed FeaturePython)
  n = 0.001
FEATURE [App::DocumentObjectGroupPython] G4_SKIN_ICRP  # scripted group (container) (typed FeaturePython)
  Dunit = g/cm3
  Dvalue = 1.09
  Group = -> [H_element095,C_element103,N_element039,O_element088,Na_element013,P_element009,S_element020,Cl_element023,K_element010]
  conduct = 2
  density = 1
  expand = 3
  formula = G4_SKIN_ICRP
  name = G4_SKIN_ICRP
  specific = 4
FEATURE [App::DocumentObjectGroupPython] Na_element014  label="Na_element : 2"  # scripted group (container) (typed FeaturePython)
  n = 2
  ref = Na_element
FEATURE [App::DocumentObjectGroupPython] C_element104  label="C_element : 058"  # scripted group (container) (typed FeaturePython)
  n = 1
  ref = C_element
FEATURE [App::DocumentObjectGroupPython] O_element089  label="O_element : 049"  # scripted group (container) (typed FeaturePython)
  n = 3
  ref = O_element
FEATURE [App::DocumentObjectGroupPython] G4_SODIUM_CARBONATE  # scripted group (container) (typed FeaturePython)
  Dunit = g/cm3
  Dvalue = 2.532
  Group = -> [Na_element014,C_element104,O_element089]
  conduct = 2
  density = 1
  expand = 3
  formula = G4_SODIUM_CARBONATE
  name = G4_SODIUM_CARBONATE
  specific = 4
FEATURE [App::DocumentObjectGroupPython] Na_element015  label="Na_element : 1"  # scripted group (container) (typed FeaturePython)
  n = 1
  ref = Na_element
FEATURE [App::DocumentObjectGroupPython] I_element009  label="I_element : 005"  # scripted group (container) (typed FeaturePython)
  n = 1
  ref = I_element
FEATURE [App::DocumentObjectGroupPython] G4_SODIUM_IODIDE  # scripted group (container) (typed FeaturePython)
  Dunit = g/cm3
  Dvalue = 3.667
  Group = -> [Na_element015,I_element009]
  conduct = 2
  density = 1
  expand = 3
  formula = G4_SODIUM_IODIDE
  name = G4_SODIUM_IODIDE
  specific = 4
FEATURE [App::DocumentObjectGroupPython] Na_element016  label="Na_element : 003"  # scripted group (container) (typed FeaturePython)
  n = 2
  ref = Na_element
FEATURE [App::DocumentObjectGroupPython] O_element090  label="O_element : 050"  # scripted group (container) (typed FeaturePython)
  n = 1
  ref = O_element
FEATURE [App::DocumentObjectGroupPython] G4_SODIUM_MONOXIDE  # scripted group (container) (typed FeaturePython)
  Dunit = g/cm3
  Dvalue = 2.27
  Group = -> [Na_element016,O_element090]
  conduct = 2
  density = 1
  expand = 3
  formula = G4_SODIUM_MONOXIDE
  name = G4_SODIUM_MONOXIDE
  specific = 4
FEATURE [App::DocumentObjectGroupPython] Na_element017  label="Na_element : 004"  # scripted group (container) (typed FeaturePython)
  n = 1
  ref = Na_element
FEATURE [App::DocumentObjectGroupPython] N_element040  label="N_element : 018"  # scripted group (container) (typed FeaturePython)
  n = 1
  ref = N_element
FEATURE [App::DocumentObjectGroupPython] O_element091  label="O_element : 051"  # scripted group (container) (typed FeaturePython)
  n = 3
  ref = O_element
FEATURE [App::DocumentObjectGroupPython] G4_SODIUM_NITRATE  # scripted group (container) (typed FeaturePython)
  Dunit = g/cm3
  Dvalue = 2.261
  Group = -> [Na_element017,N_element040,O_element091]
  conduct = 2
  density = 1
  expand = 3
  formula = G4_SODIUM_NITRATE
  name = G4_SODIUM_NITRATE
  specific = 4
FEATURE [App::DocumentObjectGroupPython] C_element105  label="C_element : 059"  # scripted group (container) (typed FeaturePython)
  n = 14
  ref = C_element
FEATURE [App::DocumentObjectGroupPython] H_element096  label="H_element : 053"  # scripted group (container) (typed FeaturePython)
  n = 12
  ref = H_element
FEATURE [App::DocumentObjectGroupPython] G4_STILBENE  # scripted group (container) (typed FeaturePython)
  Dunit = g/cm3
  Dvalue = 0.9707
  Group = -> [C_element105,H_element096]
  conduct = 2
  density = 1
  expand = 3
  formula = G4_STILBENE
  name = G4_STILBENE
  specific = 4
FEATURE [App::DocumentObjectGroupPython] C_element106  label="C_element : 12"  # scripted group (container) (typed FeaturePython)
  n = 12
  ref = C_element
FEATURE [App::DocumentObjectGroupPython] H_element097  label="H_element : 22"  # scripted group (container) (typed FeaturePython)
  n = 22
  ref = H_element
FEATURE [App::DocumentObjectGroupPython] O_element092  label="O_element : 11"  # scripted group (container) (typed FeaturePython)
  n = 11
  ref = O_element
FEATURE [App::DocumentObjectGroupPython] G4_SUCROSE  # scripted group (container) (typed FeaturePython)
  Dunit = g/cm3
  Dvalue = 1.5805
  Group = -> [C_element106,H_element097,O_element092]
  conduct = 2
  density = 1
  expand = 3
  formula = G4_SUCROSE
  name = G4_SUCROSE
  specific = 4
FEATURE [App::DocumentObjectGroupPython] C_element107  label="C_element : 18"  # scripted group (container) (typed FeaturePython)
  n = 18
  ref = C_element
FEATURE [App::DocumentObjectGroupPython] H_element098  label="H_element : 054"  # scripted group (container) (typed FeaturePython)
  n = 14
  ref = H_element
FEATURE [App::DocumentObjectGroupPython] G4_TERPHENYL  # scripted group (container) (typed FeaturePython)
  Dunit = g/cm3
  Dvalue = 1.24
  Group = -> [C_element107,H_element098]
  conduct = 2
  density = 1
  expand = 3
  formula = G4_TERPHENYL
  name = G4_TERPHENYL
  specific = 4
FEATURE [App::DocumentObjectGroupPython] H_element099  label="H_element : 0.146"  # scripted group (container) (typed FeaturePython)
  n = 0.106
FEATURE [App::DocumentObjectGroupPython] C_element108  label="C_element : 0.883"  # scripted group (container) (typed FeaturePython)
  n = 0.099
FEATURE [App::DocumentObjectGroupPython] N_element041  label="N_element : 0.020"  # scripted group (container) (typed FeaturePython)
  n = 0.02
FEATURE [App::DocumentObjectGroupPython] O_element093  label="O_element : 0.766"  # scripted group (container) (typed FeaturePython)
  n = 0.766
FEATURE [App::DocumentObjectGroupPython] Na_element018  label="Na_element : 0.101"  # scripted group (container) (typed FeaturePython)
  n = 0.002
FEATURE [App::DocumentObjectGroupPython] P_element010  label="P_element : 0.108"  # scripted group (container) (typed FeaturePython)
  n = 0.001
FEATURE [App::DocumentObjectGroupPython] S_element021  label="S_element : 0.022"  # scripted group (container) (typed FeaturePython)
  n = 0.002
FEATURE [App::DocumentObjectGroupPython] Cl_element024  label="Cl_element : 0.002"  # scripted group (container) (typed FeaturePython)
  n = 0.002
FEATURE [App::DocumentObjectGroupPython] K_element011  label="K_element : 0.017"  # scripted group (container) (typed FeaturePython)
  n = 0.002
FEATURE [App::DocumentObjectGroupPython] G4_TESTIS_ICRP  # scripted group (container) (typed FeaturePython)
  Dunit = g/cm3
  Dvalue = 1.04
  Group = -> [H_element099,C_element108,N_element041,O_element093,Na_element018,P_element010,S_element021,Cl_element024,K_element011]
  conduct = 2
  density = 1
  expand = 3
  formula = G4_TESTIS_ICRP
  name = G4_TESTIS_ICRP
  specific = 4
FEATURE [App::DocumentObjectGroupPython] C_element109  label="C_element : 060"  # scripted group (container) (typed FeaturePython)
  n = 2
  ref = C_element
FEATURE [App::DocumentObjectGroupPython] Cl_element025  label="Cl_element : 012"  # scripted group (container) (typed FeaturePython)
  n = 4
  ref = Cl_element
FEATURE [App::DocumentObjectGroupPython] G4_TETRACHLOROETHYLENE  # scripted group (container) (typed FeaturePython)
  Dunit = g/cm3
  Dvalue = 1.625
  Group = -> [C_element109,Cl_element025]
  conduct = 2
  density = 1
  expand = 3
  formula = G4_TETRACHLOROETHYLENE
  name = G4_TETRACHLOROETHYLENE
  specific = 4
FEATURE [App::DocumentObjectGroupPython] Tl_element001  label="Tl_element : 1"  # scripted group (container) (typed FeaturePython)
  n = 1
  ref = Tl_element
FEATURE [App::DocumentObjectGroupPython] Cl_element026  label="Cl_element : 013"  # scripted group (container) (typed FeaturePython)
  n = 1
  ref = Cl_element
FEATURE [App::DocumentObjectGroupPython] G4_THALLIUM_CHLORIDE  # scripted group (container) (typed FeaturePython)
  Dunit = g/cm3
  Dvalue = 7.004
  Group = -> [Tl_element001,Cl_element026]
  conduct = 2
  density = 1
  expand = 3
  formula = G4_THALLIUM_CHLORIDE
  name = G4_THALLIUM_CHLORIDE
  specific = 4
FEATURE [App::DocumentObjectGroupPython] H_element100  label="H_element : 0.147"  # scripted group (container) (typed FeaturePython)
  n = 0.105
FEATURE [App::DocumentObjectGroupPython] C_element110  label="C_element : 0.256"  # scripted group (container) (typed FeaturePython)
  n = 0.256
FEATURE [App::DocumentObjectGroupPython] N_element042  label="N_element : 0.760"  # scripted group (container) (typed FeaturePython)
  n = 0.027
FEATURE [App::DocumentObjectGroupPython] O_element094  label="O_element : 0.602"  # scripted group (container) (typed FeaturePython)
  n = 0.602
FEATURE [App::DocumentObjectGroupPython] Na_element019  label="Na_element : 0.102"  # scripted group (container) (typed FeaturePython)
  n = 0.001
FEATURE [App::DocumentObjectGroupPython] P_element011  label="P_element : 0.109"  # scripted group (container) (typed FeaturePython)
  n = 0.002
FEATURE [App::DocumentObjectGroupPython] S_element022  label="S_element : 0.023"  # scripted group (container) (typed FeaturePython)
  n = 0.003
FEATURE [App::DocumentObjectGroupPython] Cl_element027  label="Cl_element : 0.591"  # scripted group (container) (typed FeaturePython)
  n = 0.002
FEATURE [App::DocumentObjectGroupPython] K_element012  label="K_element : 0.018"  # scripted group (container) (typed FeaturePython)
  n = 0.002
FEATURE [App::DocumentObjectGroupPython] G4_TISSUE_SOFT_ICRP  # scripted group (container) (typed FeaturePython)
  Dunit = g/cm3
  Dvalue = 1.03
  Group = -> [H_element100,C_element110,N_element042,O_element094,Na_element019,P_element011,S_element022,Cl_element027,K_element012]
  conduct = 2
  density = 1
  expand = 3
  formula = G4_TISSUE_SOFT_ICRP
  name = G4_TISSUE_SOFT_ICRP
  specific = 4
FEATURE [App::DocumentObjectGroupPython] H_element101  label="H_element : 0.148"  # scripted group (container) (typed FeaturePython)
  n = 0.101
FEATURE [App::DocumentObjectGroupPython] C_element111  label="C_element : 0.111"  # scripted group (container) (typed FeaturePython)
  n = 0.111
FEATURE [App::DocumentObjectGroupPython] N_element043  label="N_element : 0.026"  # scripted group (container) (typed FeaturePython)
  n = 0.026
FEATURE [App::DocumentObjectGroupPython] O_element095  label="O_element : 0.762"  # scripted group (container) (typed FeaturePython)
  n = 0.762
FEATURE [App::DocumentObjectGroupPython] G4_TISSUE_SOFT_ICRU_4  label="G4_TISSUE_SOFT_ICRU-4"  # scripted group (container) (typed FeaturePython)
  Dunit = g/cm3
  Dvalue = 1
  Group = -> [H_element101,C_element111,N_element043,O_element095]
  conduct = 2
  density = 1
  expand = 3
  formula = G4_TISSUE_SOFT_ICRU-4
  name = G4_TISSUE_SOFT_ICRU-4
  specific = 4
FEATURE [App::DocumentObjectGroupPython] H_element102  label="H_element : 0.149"  # scripted group (container) (typed FeaturePython)
  n = 0.101869
FEATURE [App::DocumentObjectGroupPython] C_element112  label="C_element : 0.456"  # scripted group (container) (typed FeaturePython)
  n = 0.456179
FEATURE [App::DocumentObjectGroupPython] N_element044  label="N_element : 0.761"  # scripted group (container) (typed FeaturePython)
  n = 0.035172
FEATURE [App::DocumentObjectGroupPython] O_element096  label="O_element : 0.407"  # scripted group (container) (typed FeaturePython)
  n = 0.40678
FEATURE [App::DocumentObjectGroupPython] G4_TISSUE_METHANE  label="G4_TISSUE-METHANE"  # scripted group (container) (typed FeaturePython)
  Dunit = g/cm3
  Dvalue = 0.00106409
  Group = -> [H_element102,C_element112,N_element044,O_element096]
  conduct = 2
  density = 1
  expand = 3
  formula = G4_TISSUE-METHANE
  name = G4_TISSUE-METHANE
  specific = 4
FEATURE [App::DocumentObjectGroupPython] H_element103  label="H_element : 0.103"  # scripted group (container) (typed FeaturePython)
  n = 0.102672
FEATURE [App::DocumentObjectGroupPython] C_element113  label="C_element : 0.569"  # scripted group (container) (typed FeaturePython)
  n = 0.56894
FEATURE [App::DocumentObjectGroupPython] N_element045  label="N_element : 0.762"  # scripted group (container) (typed FeaturePython)
  n = 0.035022
FEATURE [App::DocumentObjectGroupPython] O_element097  label="O_element : 0.293"  # scripted group (container) (typed FeaturePython)
  n = 0.293366
FEATURE [App::DocumentObjectGroupPython] G4_TISSUE_PROPANE  label="G4_TISSUE-PROPANE"  # scripted group (container) (typed FeaturePython)
  Dunit = g/cm3
  Dvalue = 0.00182628
  Group = -> [H_element103,C_element113,N_element045,O_element097]
  conduct = 2
  density = 1
  expand = 3
  formula = G4_TISSUE-PROPANE
  name = G4_TISSUE-PROPANE
  specific = 4
FEATURE [App::DocumentObjectGroupPython] Ti_element003  label="Ti_element : 1"  # scripted group (container) (typed FeaturePython)
  n = 1
  ref = Ti_element
FEATURE [App::DocumentObjectGroupPython] O_element098  label="O_element : 052"  # scripted group (container) (typed FeaturePython)
  n = 2
  ref = O_element
FEATURE [App::DocumentObjectGroupPython] G4_TITANIUM_DIOXIDE  # scripted group (container) (typed FeaturePython)
  Dunit = g/cm3
  Dvalue = 4.26
  Group = -> [Ti_element003,O_element098]
  conduct = 2
  density = 1
  expand = 3
  formula = G4_TITANIUM_DIOXIDE
  name = G4_TITANIUM_DIOXIDE
  specific = 4
FEATURE [App::DocumentObjectGroupPython] C_element114  label="C_element : 061"  # scripted group (container) (typed FeaturePython)
  n = 7
  ref = C_element
FEATURE [App::DocumentObjectGroupPython] H_element104  label="H_element : 055"  # scripted group (container) (typed FeaturePython)
  n = 8
  ref = H_element
FEATURE [App::DocumentObjectGroupPython] G4_TOLUENE  # scripted group (container) (typed FeaturePython)
  Dunit = g/cm3
  Dvalue = 0.8669
  Group = -> [C_element114,H_element104]
  conduct = 2
  density = 1
  expand = 3
  formula = G4_TOLUENE
  name = G4_TOLUENE
  specific = 4
FEATURE [App::DocumentObjectGroupPython] C_element115  label="C_element : 062"  # scripted group (container) (typed FeaturePython)
  n = 2
  ref = C_element
FEATURE [App::DocumentObjectGroupPython] H_element105  label="H_element : 056"  # scripted group (container) (typed FeaturePython)
  n = 1
  ref = H_element
FEATURE [App::DocumentObjectGroupPython] Cl_element028  label="Cl_element : 014"  # scripted group (container) (typed FeaturePython)
  n = 3
  ref = Cl_element
FEATURE [App::DocumentObjectGroupPython] G4_TRICHLOROETHYLENE  # scripted group (container) (typed FeaturePython)
  Dunit = g/cm3
  Dvalue = 1.46
  Group = -> [C_element115,H_element105,Cl_element028]
  conduct = 2
  density = 1
  expand = 3
  formula = G4_TRICHLOROETHYLENE
  name = G4_TRICHLOROETHYLENE
  specific = 4
FEATURE [App::DocumentObjectGroupPython] C_element116  label="C_element : 063"  # scripted group (container) (typed FeaturePython)
  n = 6
  ref = C_element
FEATURE [App::DocumentObjectGroupPython] H_element106  label="H_element : 15"  # scripted group (container) (typed FeaturePython)
  n = 15
  ref = H_element
FEATURE [App::DocumentObjectGroupPython] O_element099  label="O_element : 053"  # scripted group (container) (typed FeaturePython)
  n = 4
  ref = O_element
FEATURE [App::DocumentObjectGroupPython] P_element012  label="P_element : 1"  # scripted group (container) (typed FeaturePython)
  n = 1
  ref = P_element
FEATURE [App::DocumentObjectGroupPython] G4_TRIETHYL_PHOSPHATE  # scripted group (container) (typed FeaturePython)
  Dunit = g/cm3
  Dvalue = 1.07
  Group = -> [C_element116,H_element106,O_element099,P_element012]
  conduct = 2
  density = 1
  expand = 3
  formula = G4_TRIETHYL_PHOSPHATE
  name = G4_TRIETHYL_PHOSPHATE
  specific = 4
FEATURE [App::DocumentObjectGroupPython] W_element003  label="W_element : 003"  # scripted group (container) (typed FeaturePython)
  n = 1
  ref = W_element
FEATURE [App::DocumentObjectGroupPython] F_element017  label="F_element : 6"  # scripted group (container) (typed FeaturePython)
  n = 6
  ref = F_element
FEATURE [App::DocumentObjectGroupPython] G4_TUNGSTEN_HEXAFLUORIDE  # scripted group (container) (typed FeaturePython)
  Dunit = g/cm3
  Dvalue = 2.4
  Group = -> [W_element003,F_element017]
  conduct = 2
  density = 1
  expand = 3
  formula = G4_TUNGSTEN_HEXAFLUORIDE
  name = G4_TUNGSTEN_HEXAFLUORIDE
  specific = 4
FEATURE [App::DocumentObjectGroupPython] U_element001  label="U_element : 1"  # scripted group (container) (typed FeaturePython)
  n = 1
  ref = U_element
FEATURE [App::DocumentObjectGroupPython] C_element117  label="C_element : 064"  # scripted group (container) (typed FeaturePython)
  n = 2
  ref = C_element
FEATURE [App::DocumentObjectGroupPython] G4_URANIUM_DICARBIDE  # scripted group (container) (typed FeaturePython)
  Dunit = g/cm3
  Dvalue = 11.28
  Group = -> [U_element001,C_element117]
  conduct = 2
  density = 1
  expand = 3
  formula = G4_URANIUM_DICARBIDE
  name = G4_URANIUM_DICARBIDE
  specific = 4
FEATURE [App::DocumentObjectGroupPython] U_element002  label="U_element : 002"  # scripted group (container) (typed FeaturePython)
  n = 1
  ref = U_element
FEATURE [App::DocumentObjectGroupPython] C_element118  label="C_element : 065"  # scripted group (container) (typed FeaturePython)
  n = 1
  ref = C_element
FEATURE [App::DocumentObjectGroupPython] G4_URANIUM_MONOCARBIDE  # scripted group (container) (typed FeaturePython)
  Dunit = g/cm3
  Dvalue = 13.63
  Group = -> [U_element002,C_element118]
  conduct = 2
  density = 1
  expand = 3
  formula = G4_URANIUM_MONOCARBIDE
  name = G4_URANIUM_MONOCARBIDE
  specific = 4
FEATURE [App::DocumentObjectGroupPython] U_element003  label="U_element : 003"  # scripted group (container) (typed FeaturePython)
  n = 1
  ref = U_element
FEATURE [App::DocumentObjectGroupPython] O_element100  label="O_element : 054"  # scripted group (container) (typed FeaturePython)
  n = 2
  ref = O_element
FEATURE [App::DocumentObjectGroupPython] G4_URANIUM_OXIDE  # scripted group (container) (typed FeaturePython)
  Dunit = g/cm3
  Dvalue = 10.96
  Group = -> [U_element003,O_element100]
  conduct = 2
  density = 1
  expand = 3
  formula = G4_URANIUM_OXIDE
  name = G4_URANIUM_OXIDE
  specific = 4
FEATURE [App::DocumentObjectGroupPython] C_element119  label="C_element : 066"  # scripted group (container) (typed FeaturePython)
  n = 1
  ref = C_element
FEATURE [App::DocumentObjectGroupPython] H_element107  label="H_element : 057"  # scripted group (container) (typed FeaturePython)
  n = 4
  ref = H_element
FEATURE [App::DocumentObjectGroupPython] N_element046  label="N_element : 019"  # scripted group (container) (typed FeaturePython)
  n = 2
  ref = N_element
FEATURE [App::DocumentObjectGroupPython] O_element101  label="O_element : 055"  # scripted group (container) (typed FeaturePython)
  n = 1
  ref = O_element
FEATURE [App::DocumentObjectGroupPython] G4_UREA  # scripted group (container) (typed FeaturePython)
  Dunit = g/cm3
  Dvalue = 1.323
  Group = -> [C_element119,H_element107,N_element046,O_element101]
  conduct = 2
  density = 1
  expand = 3
  formula = G4_UREA
  name = G4_UREA
  specific = 4
FEATURE [App::DocumentObjectGroupPython] C_element120  label="C_element : 067"  # scripted group (container) (typed FeaturePython)
  n = 5
  ref = C_element
FEATURE [App::DocumentObjectGroupPython] H_element108  label="H_element : 058"  # scripted group (container) (typed FeaturePython)
  n = 11
  ref = H_element
FEATURE [App::DocumentObjectGroupPython] N_element047  label="N_element : 020"  # scripted group (container) (typed FeaturePython)
  n = 1
  ref = N_element
FEATURE [App::DocumentObjectGroupPython] O_element102  label="O_element : 056"  # scripted group (container) (typed FeaturePython)
  n = 2
  ref = O_element
FEATURE [App::DocumentObjectGroupPython] G4_VALINE  # scripted group (container) (typed FeaturePython)
  Dunit = g/cm3
  Dvalue = 1.23
  Group = -> [C_element120,H_element108,N_element047,O_element102]
  conduct = 2
  density = 1
  expand = 3
  formula = G4_VALINE
  name = G4_VALINE
  specific = 4
FEATURE [App::DocumentObjectGroupPython] H_element109  label="H_element : 0.009"  # scripted group (container) (typed FeaturePython)
  n = 0.009417
FEATURE [App::DocumentObjectGroupPython] C_element121  label="C_element : 0.281"  # scripted group (container) (typed FeaturePython)
  n = 0.280555
FEATURE [App::DocumentObjectGroupPython] F_element018  label="F_element : 0.710"  # scripted group (container) (typed FeaturePython)
  n = 0.710028
FEATURE [App::DocumentObjectGroupPython] G4_VITON  # scripted group (container) (typed FeaturePython)
  Dunit = g/cm3
  Dvalue = 1.8
  Group = -> [H_element109,C_element121,F_element018]
  conduct = 2
  density = 1
  expand = 3
  formula = G4_VITON
  name = G4_VITON
  specific = 4
FEATURE [App::DocumentObjectGroupPython] H_element110  label="H_element : 059"  # scripted group (container) (typed FeaturePython)
  n = 2
  ref = H_element
FEATURE [App::DocumentObjectGroupPython] O_element103  label="O_element : 057"  # scripted group (container) (typed FeaturePython)
  n = 1
  ref = O_element
FEATURE [App::DocumentObjectGroupPython] G4_WATER  # scripted group (container) (typed FeaturePython)
  Dunit = g/cm3
  Dvalue = 1
  Group = -> [H_element110,O_element103]
  conduct = 2
  density = 1
  expand = 3
  formula = G4_WATER
  name = G4_WATER
  specific = 4
FEATURE [App::DocumentObjectGroupPython] H_element111  label="H_element : 060"  # scripted group (container) (typed FeaturePython)
  n = 2
  ref = H_element
FEATURE [App::DocumentObjectGroupPython] O_element104  label="O_element : 058"  # scripted group (container) (typed FeaturePython)
  n = 1
  ref = O_element
FEATURE [App::DocumentObjectGroupPython] G4_WATER_VAPOR  # scripted group (container) (typed FeaturePython)
  Dunit = g/cm3
  Dvalue = 0.000756182
  Group = -> [H_element111,O_element104]
  conduct = 2
  density = 1
  expand = 3
  formula = G4_WATER_VAPOR
  name = G4_WATER_VAPOR
  specific = 4
FEATURE [App::DocumentObjectGroupPython] C_element122  label="C_element : 068"  # scripted group (container) (typed FeaturePython)
  n = 8
  ref = C_element
FEATURE [App::DocumentObjectGroupPython] H_element112  label="H_element : 061"  # scripted group (container) (typed FeaturePython)
  n = 10
  ref = H_element
FEATURE [App::DocumentObjectGroupPython] G4_XYLENE  # scripted group (container) (typed FeaturePython)
  Dunit = g/cm3
  Dvalue = 0.87
  Group = -> [C_element122,H_element112]
  conduct = 2
  density = 1
  expand = 3
  formula = G4_XYLENE
  name = G4_XYLENE
  specific = 4
FEATURE [App::DocumentObjectGroupPython] C_element123  label="C_element : 069"  # scripted group (container) (typed FeaturePython)
  n = 1
  ref = C_element
FEATURE [App::DocumentObjectGroupPython] G4_GRAPHITE  # scripted group (container) (typed FeaturePython)
  Dunit = g/cm3
  Dvalue = 2.21
  Group = -> [C_element123]
  conduct = 2
  density = 1
  expand = 3
  formula = G4_GRAPHITE
  name = G4_GRAPHITE
  specific = 4
FEATURE [App::DocumentObjectGroupPython] NIST  # scripted group (container) (typed FeaturePython)
  Group = -> [G4_A_150_TISSUE,G4_ACETONE,G4_ACETYLENE,G4_ADENINE,G4_ADIPOSE_TISSUE_ICRP,G4_AIR,G4_ALANINE,G4_ALUMINUM_OXIDE,G4_AMBER,G4_AMMONIA,G4_ANILINE,G4_ANTHRACENE,G4_B_100_BONE,G4_BAKELITE,G4_BARIUM_FLUORIDE,G4_BARIUM_SULFATE,G4_BENZENE,G4_BERYLLIUM_OXIDE,G4_BGO,G4_BLOOD_ICRP,G4_BONE_COMPACT_ICRU,G4_BONE_CORTICAL_ICRP,G4_BORON_CARBIDE,G4_BORON_OXIDE,G4_BRAIN_ICRP,G4_BUTANE,G4_N_BUTYL_ALCOHOL,G4_C_552,+152 more]
FEATURE [App::DocumentObjectGroupPython] H_element113  label="H_element : 062"  # scripted group (container) (typed FeaturePython)
  n = 1
  ref = H_element
FEATURE [App::DocumentObjectGroupPython] G4_H  # scripted group (container) (typed FeaturePython)
  Dunit = g/cm3
  Dvalue = 8.3748e-05
  Group = -> [H_element113]
  conduct = 2
  density = 1
  expand = 3
  formula = H
  name = G4_H
  specific = 4
FEATURE [App::DocumentObjectGroupPython] He_element001  label="He_element : 1"  # scripted group (container) (typed FeaturePython)
  n = 1
  ref = He_element
FEATURE [App::DocumentObjectGroupPython] G4_He  # scripted group (container) (typed FeaturePython)
  Dunit = g/cm3
  Dvalue = 0.000166322
  Group = -> [He_element001]
  conduct = 2
  density = 1
  expand = 3
  formula = He
  name = G4_He
  specific = 4
FEATURE [App::DocumentObjectGroupPython] Li_element008  label="Li_element : 008"  # scripted group (container) (typed FeaturePython)
  n = 1
  ref = Li_element
FEATURE [App::DocumentObjectGroupPython] G4_Li  # scripted group (container) (typed FeaturePython)
  Dunit = g/cm3
  Dvalue = 0.534
  Group = -> [Li_element008]
  conduct = 2
  density = 1
  expand = 3
  formula = Li
  name = G4_Li
  specific = 4
FEATURE [App::DocumentObjectGroupPython] Be_element002  label="Be_element : 002"  # scripted group (container) (typed FeaturePython)
  n = 1
  ref = Be_element
FEATURE [App::DocumentObjectGroupPython] G4_Be  # scripted group (container) (typed FeaturePython)
  Dunit = g/cm3
  Dvalue = 1.848
  Group = -> [Be_element002]
  conduct = 2
  density = 1
  expand = 3
  formula = Be
  name = G4_Be
  specific = 4
FEATURE [App::DocumentObjectGroupPython] B_element007  label="B_element : 007"  # scripted group (container) (typed FeaturePython)
  n = 1
  ref = B_element
FEATURE [App::DocumentObjectGroupPython] G4_B  # scripted group (container) (typed FeaturePython)
  Dunit = g/cm3
  Dvalue = 2.37
  Group = -> [B_element007]
  conduct = 2
  density = 1
  expand = 3
  formula = B
  name = G4_B
  specific = 4
FEATURE [App::DocumentObjectGroupPython] C_element124  label="C_element : 070"  # scripted group (container) (typed FeaturePython)
  n = 1
  ref = C_element
FEATURE [App::DocumentObjectGroupPython] G4_C  # scripted group (container) (typed FeaturePython)
  Dunit = g/cm3
  Dvalue = 2
  Group = -> [C_element124]
  conduct = 2
  density = 1
  expand = 3
  formula = C
  name = G4_C
  specific = 4
FEATURE [App::DocumentObjectGroupPython] N_element048  label="N_element : 021"  # scripted group (container) (typed FeaturePython)
  n = 1
  ref = N_element
FEATURE [App::DocumentObjectGroupPython] G4_N  # scripted group (container) (typed FeaturePython)
  Dunit = g/cm3
  Dvalue = 0.0011652
  Group = -> [N_element048]
  conduct = 2
  density = 1
  expand = 3
  formula = N
  name = G4_N
  specific = 4
FEATURE [App::DocumentObjectGroupPython] O_element105  label="O_element : 059"  # scripted group (container) (typed FeaturePython)
  n = 1
  ref = O_element
FEATURE [App::DocumentObjectGroupPython] G4_O  # scripted group (container) (typed FeaturePython)
  Dunit = g/cm3
  Dvalue = 0.00133151
  Group = -> [O_element105]
  conduct = 2
  density = 1
  expand = 3
  formula = O
  name = G4_O
  specific = 4
FEATURE [App::DocumentObjectGroupPython] F_element019  label="F_element : 008"  # scripted group (container) (typed FeaturePython)
  n = 1
  ref = F_element
FEATURE [App::DocumentObjectGroupPython] G4_F  # scripted group (container) (typed FeaturePython)
  Dunit = g/cm3
  Dvalue = 0.00158029
  Group = -> [F_element019]
  conduct = 2
  density = 1
  expand = 3
  formula = F
  name = G4_F
  specific = 4
FEATURE [App::DocumentObjectGroupPython] Ne_element001  label="Ne_element : 1"  # scripted group (container) (typed FeaturePython)
  n = 1
  ref = Ne_element
FEATURE [App::DocumentObjectGroupPython] G4_Ne  # scripted group (container) (typed FeaturePython)
  Dunit = g/cm3
  Dvalue = 0.000838505
  Group = -> [Ne_element001]
  conduct = 2
  density = 1
  expand = 3
  formula = Ne
  name = G4_Ne
  specific = 4
FEATURE [App::DocumentObjectGroupPython] Na_element020  label="Na_element : 005"  # scripted group (container) (typed FeaturePython)
  n = 1
  ref = Na_element
FEATURE [App::DocumentObjectGroupPython] G4_Na  # scripted group (container) (typed FeaturePython)
  Dunit = g/cm3
  Dvalue = 0.971
  Group = -> [Na_element020]
  conduct = 2
  density = 1
  expand = 3
  formula = Na
  name = G4_Na
  specific = 4
FEATURE [App::DocumentObjectGroupPython] Mg_element011  label="Mg_element : 005"  # scripted group (container) (typed FeaturePython)
  n = 1
  ref = Mg_element
FEATURE [App::DocumentObjectGroupPython] G4_Mg  # scripted group (container) (typed FeaturePython)
  Dunit = g/cm3
  Dvalue = 1.74
  Group = -> [Mg_element011]
  conduct = 2
  density = 1
  expand = 3
  formula = Mg
  name = G4_Mg
  specific = 4
FEATURE [App::DocumentObjectGroupPython] Al_element004  label="Al_element : 1"  # scripted group (container) (typed FeaturePython)
  n = 1
  ref = Al_element
FEATURE [App::DocumentObjectGroupPython] G4_Al  # scripted group (container) (typed FeaturePython)
  Dunit = g/cm3
  Dvalue = 2.699
  Group = -> [Al_element004]
  conduct = 2
  density = 1
  expand = 3
  formula = Al
  name = G4_Al
  specific = 4
FEATURE [App::DocumentObjectGroupPython] Si_element007  label="Si_element : 002"  # scripted group (container) (typed FeaturePython)
  n = 1
  ref = Si_element
FEATURE [App::DocumentObjectGroupPython] G4_Si  # scripted group (container) (typed FeaturePython)
  Dunit = g/cm3
  Dvalue = 2.33
  Group = -> [Si_element007]
  conduct = 2
  density = 1
  expand = 3
  formula = Si
  name = G4_Si
  specific = 4
FEATURE [App::DocumentObjectGroupPython] P_element013  label="P_element : 002"  # scripted group (container) (typed FeaturePython)
  n = 1
  ref = P_element
FEATURE [App::DocumentObjectGroupPython] G4_P  # scripted group (container) (typed FeaturePython)
  Dunit = g/cm3
  Dvalue = 2.2
  Group = -> [P_element013]
  conduct = 2
  density = 1
  expand = 3
  formula = P
  name = G4_P
  specific = 4
FEATURE [App::DocumentObjectGroupPython] S_element023  label="S_element : 007"  # scripted group (container) (typed FeaturePython)
  n = 1
  ref = S_element
FEATURE [App::DocumentObjectGroupPython] G4_S  # scripted group (container) (typed FeaturePython)
  Dunit = g/cm3
  Dvalue = 2
  Group = -> [S_element023]
  conduct = 2
  density = 1
  expand = 3
  formula = S
  name = G4_S
  specific = 4
FEATURE [App::DocumentObjectGroupPython] Cl_element029  label="Cl_element : 015"  # scripted group (container) (typed FeaturePython)
  n = 1
  ref = Cl_element
FEATURE [App::DocumentObjectGroupPython] G4_Cl  # scripted group (container) (typed FeaturePython)
  Dunit = g/cm3
  Dvalue = 0.00299473
  Group = -> [Cl_element029]
  conduct = 2
  density = 1
  expand = 3
  formula = Cl
  name = G4_Cl
  specific = 4
FEATURE [App::DocumentObjectGroupPython] Ar_element002  label="Ar_element : 1"  # scripted group (container) (typed FeaturePython)
  n = 1
  ref = Ar_element
FEATURE [App::DocumentObjectGroupPython] G4_Ar  # scripted group (container) (typed FeaturePython)
  Dunit = g/cm3
  Dvalue = 0.00166201
  Group = -> [Ar_element002]
  conduct = 2
  density = 1
  expand = 3
  formula = Ar
  name = G4_Ar
  specific = 4
FEATURE [App::DocumentObjectGroupPython] K_element013  label="K_element : 003"  # scripted group (container) (typed FeaturePython)
  n = 1
  ref = K_element
FEATURE [App::DocumentObjectGroupPython] G4_K  # scripted group (container) (typed FeaturePython)
  Dunit = g/cm3
  Dvalue = 0.862
  Group = -> [K_element013]
  conduct = 2
  density = 1
  expand = 3
  formula = K
  name = G4_K
  specific = 4
FEATURE [App::DocumentObjectGroupPython] Ca_element014  label="Ca_element : 007"  # scripted group (container) (typed FeaturePython)
  n = 1
  ref = Ca_element
FEATURE [App::DocumentObjectGroupPython] G4_Ca  # scripted group (container) (typed FeaturePython)
  Dunit = g/cm3
  Dvalue = 1.55
  Group = -> [Ca_element014]
  conduct = 2
  density = 1
  expand = 3
  formula = Ca
  name = G4_Ca
  specific = 4
FEATURE [App::DocumentObjectGroupPython] Sc_element001  label="Sc_element : 1"  # scripted group (container) (typed FeaturePython)
  n = 1
  ref = Sc_element
FEATURE [App::DocumentObjectGroupPython] G4_Sc  # scripted group (container) (typed FeaturePython)
  Dunit = g/cm3
  Dvalue = 2.989
  Group = -> [Sc_element001]
  conduct = 2
  density = 1
  expand = 3
  formula = Sc
  name = G4_Sc
  specific = 4
FEATURE [App::DocumentObjectGroupPython] Ti_element004  label="Ti_element : 002"  # scripted group (container) (typed FeaturePython)
  n = 1
  ref = Ti_element
FEATURE [App::DocumentObjectGroupPython] G4_Ti  # scripted group (container) (typed FeaturePython)
  Dunit = g/cm3
  Dvalue = 4.54
  Group = -> [Ti_element004]
  conduct = 2
  density = 1
  expand = 3
  formula = Ti
  name = G4_Ti
  specific = 4
FEATURE [App::DocumentObjectGroupPython] V_element001  label="V_element : 1"  # scripted group (container) (typed FeaturePython)
  n = 1
  ref = V_element
FEATURE [App::DocumentObjectGroupPython] G4_V  # scripted group (container) (typed FeaturePython)
  Dunit = g/cm3
  Dvalue = 6.11
  Group = -> [V_element001]
  conduct = 2
  density = 1
  expand = 3
  formula = V
  name = G4_V
  specific = 4
FEATURE [App::DocumentObjectGroupPython] Cr_element001  label="Cr_element : 1"  # scripted group (container) (typed FeaturePython)
  n = 1
  ref = Cr_element
FEATURE [App::DocumentObjectGroupPython] G4_Cr  # scripted group (container) (typed FeaturePython)
  Dunit = g/cm3
  Dvalue = 7.18
  Group = -> [Cr_element001]
  conduct = 2
  density = 1
  expand = 3
  formula = Cr
  name = G4_Cr
  specific = 4
FEATURE [App::DocumentObjectGroupPython] Mn_element001  label="Mn_element : 1"  # scripted group (container) (typed FeaturePython)
  n = 1
  ref = Mn_element
FEATURE [App::DocumentObjectGroupPython] G4_Mn  # scripted group (container) (typed FeaturePython)
  Dunit = g/cm3
  Dvalue = 7.44
  Group = -> [Mn_element001]
  conduct = 2
  density = 1
  expand = 3
  formula = Mn
  name = G4_Mn
  specific = 4
FEATURE [App::DocumentObjectGroupPython] Fe_element007  label="Fe_element : 004"  # scripted group (container) (typed FeaturePython)
  n = 1
  ref = Fe_element
FEATURE [App::DocumentObjectGroupPython] G4_Fe  # scripted group (container) (typed FeaturePython)
  Dunit = g/cm3
  Dvalue = 7.874
  Group = -> [Fe_element007]
  conduct = 2
  density = 1
  expand = 3
  formula = Fe
  name = G4_Fe
  specific = 4
FEATURE [App::DocumentObjectGroupPython] Co_element001  label="Co_element : 1"  # scripted group (container) (typed FeaturePython)
  n = 1
  ref = Co_element
FEATURE [App::DocumentObjectGroupPython] G4_Co  # scripted group (container) (typed FeaturePython)
  Dunit = g/cm3
  Dvalue = 8.9
  Group = -> [Co_element001]
  conduct = 2
  density = 1
  expand = 3
  formula = Co
  name = G4_Co
  specific = 4
FEATURE [App::DocumentObjectGroupPython] Ni_element001  label="Ni_element : 1"  # scripted group (container) (typed FeaturePython)
  n = 1
  ref = Ni_element
FEATURE [App::DocumentObjectGroupPython] G4_Ni  # scripted group (container) (typed FeaturePython)
  Dunit = g/cm3
  Dvalue = 8.902
  Group = -> [Ni_element001]
  conduct = 2
  density = 1
  expand = 3
  formula = Ni
  name = G4_Ni
  specific = 4
FEATURE [App::DocumentObjectGroupPython] Cu_element001  label="Cu_element : 1"  # scripted group (container) (typed FeaturePython)
  n = 1
  ref = Cu_element
FEATURE [App::DocumentObjectGroupPython] G4_Cu  # scripted group (container) (typed FeaturePython)
  Dunit = g/cm3
  Dvalue = 8.96
  Group = -> [Cu_element001]
  conduct = 2
  density = 1
  expand = 3
  formula = Cu
  name = G4_Cu
  specific = 4
FEATURE [App::DocumentObjectGroupPython] Zn_element001  label="Zn_element : 1"  # scripted group (container) (typed FeaturePython)
  n = 1
  ref = Zn_element
FEATURE [App::DocumentObjectGroupPython] G4_Zn  # scripted group (container) (typed FeaturePython)
  Dunit = g/cm3
  Dvalue = 7.133
  Group = -> [Zn_element001]
  conduct = 2
  density = 1
  expand = 3
  formula = Zn
  name = G4_Zn
  specific = 4
FEATURE [App::DocumentObjectGroupPython] Ga_element002  label="Ga_element : 002"  # scripted group (container) (typed FeaturePython)
  n = 1
  ref = Ga_element
FEATURE [App::DocumentObjectGroupPython] G4_Ga  # scripted group (container) (typed FeaturePython)
  Dunit = g/cm3
  Dvalue = 5.904
  Group = -> [Ga_element002]
  conduct = 2
  density = 1
  expand = 3
  formula = Ga
  name = G4_Ga
  specific = 4
FEATURE [App::DocumentObjectGroupPython] Ge_element002  label="Ge_element : 1"  # scripted group (container) (typed FeaturePython)
  n = 1
  ref = Ge_element
FEATURE [App::DocumentObjectGroupPython] G4_Ge  # scripted group (container) (typed FeaturePython)
  Dunit = g/cm3
  Dvalue = 5.323
  Group = -> [Ge_element002]
  conduct = 2
  density = 1
  expand = 3
  formula = Ge
  name = G4_Ge
  specific = 4
FEATURE [App::DocumentObjectGroupPython] As_element003  label="As_element : 002"  # scripted group (container) (typed FeaturePython)
  n = 1
  ref = As_element
FEATURE [App::DocumentObjectGroupPython] G4_As  # scripted group (container) (typed FeaturePython)
  Dunit = g/cm3
  Dvalue = 5.73
  Group = -> [As_element003]
  conduct = 2
  density = 1
  expand = 3
  formula = As
  name = G4_As
  specific = 4
FEATURE [App::DocumentObjectGroupPython] Se_element001  label="Se_element : 1"  # scripted group (container) (typed FeaturePython)
  n = 1
  ref = Se_element
FEATURE [App::DocumentObjectGroupPython] G4_Se  # scripted group (container) (typed FeaturePython)
  Dunit = g/cm3
  Dvalue = 4.5
  Group = -> [Se_element001]
  conduct = 2
  density = 1
  expand = 3
  formula = Se
  name = G4_Se
  specific = 4
FEATURE [App::DocumentObjectGroupPython] Br_element007  label="Br_element : 004"  # scripted group (container) (typed FeaturePython)
  n = 1
  ref = Br_element
FEATURE [App::DocumentObjectGroupPython] G4_Br  # scripted group (container) (typed FeaturePython)
  Dunit = g/cm3
  Dvalue = 0.0070721
  Group = -> [Br_element007]
  conduct = 2
  density = 1
  expand = 3
  formula = Br
  name = G4_Br
  specific = 4
FEATURE [App::DocumentObjectGroupPython] Kr_element001  label="Kr_element : 1"  # scripted group (container) (typed FeaturePython)
  n = 1
  ref = Kr_element
FEATURE [App::DocumentObjectGroupPython] G4_Kr  # scripted group (container) (typed FeaturePython)
  Dunit = g/cm3
  Dvalue = 0.00347832
  Group = -> [Kr_element001]
  conduct = 2
  density = 1
  expand = 3
  formula = Kr
  name = G4_Kr
  specific = 4
FEATURE [App::DocumentObjectGroupPython] Rb_element001  label="Rb_element : 1"  # scripted group (container) (typed FeaturePython)
  n = 1
  ref = Rb_element
FEATURE [App::DocumentObjectGroupPython] G4_Rb  # scripted group (container) (typed FeaturePython)
  Dunit = g/cm3
  Dvalue = 1.532
  Group = -> [Rb_element001]
  conduct = 2
  density = 1
  expand = 3
  formula = Rb
  name = G4_Rb
  specific = 4
FEATURE [App::DocumentObjectGroupPython] Sr_element001  label="Sr_element : 1"  # scripted group (container) (typed FeaturePython)
  n = 1
  ref = Sr_element
FEATURE [App::DocumentObjectGroupPython] G4_Sr  # scripted group (container) (typed FeaturePython)
  Dunit = g/cm3
  Dvalue = 2.54
  Group = -> [Sr_element001]
  conduct = 2
  density = 1
  expand = 3
  formula = Sr
  name = G4_Sr
  specific = 4
FEATURE [App::DocumentObjectGroupPython] Y_element001  label="Y_element : 1"  # scripted group (container) (typed FeaturePython)
  n = 1
  ref = Y_element
FEATURE [App::DocumentObjectGroupPython] G4_Y  # scripted group (container) (typed FeaturePython)
  Dunit = g/cm3
  Dvalue = 4.469
  Group = -> [Y_element001]
  conduct = 2
  density = 1
  expand = 3
  formula = Y
  name = G4_Y
  specific = 4
FEATURE [App::DocumentObjectGroupPython] Zr_element001  label="Zr_element : 1"  # scripted group (container) (typed FeaturePython)
  n = 1
  ref = Zr_element
FEATURE [App::DocumentObjectGroupPython] G4_Zr  # scripted group (container) (typed FeaturePython)
  Dunit = g/cm3
  Dvalue = 6.506
  Group = -> [Zr_element001]
  conduct = 2
  density = 1
  expand = 3
  formula = Zr
  name = G4_Zr
  specific = 4
FEATURE [App::DocumentObjectGroupPython] Nb_element001  label="Nb_element : 1"  # scripted group (container) (typed FeaturePython)
  n = 1
  ref = Nb_element
FEATURE [App::DocumentObjectGroupPython] G4_Nb  # scripted group (container) (typed FeaturePython)
  Dunit = g/cm3
  Dvalue = 8.57
  Group = -> [Nb_element001]
  conduct = 2
  density = 1
  expand = 3
  formula = Nb
  name = G4_Nb
  specific = 4
FEATURE [App::DocumentObjectGroupPython] Mo_element001  label="Mo_element : 1"  # scripted group (container) (typed FeaturePython)
  n = 1
  ref = Mo_element
FEATURE [App::DocumentObjectGroupPython] G4_Mo  # scripted group (container) (typed FeaturePython)
  Dunit = g/cm3
  Dvalue = 10.22
  Group = -> [Mo_element001]
  conduct = 2
  density = 1
  expand = 3
  formula = Mo
  name = G4_Mo
  specific = 4
FEATURE [App::DocumentObjectGroupPython] Tc_element001  label="Tc_element : 1"  # scripted group (container) (typed FeaturePython)
  n = 1
  ref = Tc_element
FEATURE [App::DocumentObjectGroupPython] G4_Tc  # scripted group (container) (typed FeaturePython)
  Dunit = g/cm3
  Dvalue = 11.5
  Group = -> [Tc_element001]
  conduct = 2
  density = 1
  expand = 3
  formula = Tc
  name = G4_Tc
  specific = 4
FEATURE [App::DocumentObjectGroupPython] Ru_element001  label="Ru_element : 1"  # scripted group (container) (typed FeaturePython)
  n = 1
  ref = Ru_element
FEATURE [App::DocumentObjectGroupPython] G4_Ru  # scripted group (container) (typed FeaturePython)
  Dunit = g/cm3
  Dvalue = 12.41
  Group = -> [Ru_element001]
  conduct = 2
  density = 1
  expand = 3
  formula = Ru
  name = G4_Ru
  specific = 4
FEATURE [App::DocumentObjectGroupPython] Rh_element001  label="Rh_element : 1"  # scripted group (container) (typed FeaturePython)
  n = 1
  ref = Rh_element
FEATURE [App::DocumentObjectGroupPython] G4_Rh  # scripted group (container) (typed FeaturePython)
  Dunit = g/cm3
  Dvalue = 12.41
  Group = -> [Rh_element001]
  conduct = 2
  density = 1
  expand = 3
  formula = Rh
  name = G4_Rh
  specific = 4
FEATURE [App::DocumentObjectGroupPython] Pd_element001  label="Pd_element : 1"  # scripted group (container) (typed FeaturePython)
  n = 1
  ref = Pd_element
FEATURE [App::DocumentObjectGroupPython] G4_Pd  # scripted group (container) (typed FeaturePython)
  Dunit = g/cm3
  Dvalue = 12.02
  Group = -> [Pd_element001]
  conduct = 2
  density = 1
  expand = 3
  formula = Pd
  name = G4_Pd
  specific = 4
FEATURE [App::DocumentObjectGroupPython] Ag_element006  label="Ag_element : 004"  # scripted group (container) (typed FeaturePython)
  n = 1
  ref = Ag_element
FEATURE [App::DocumentObjectGroupPython] G4_Ag  # scripted group (container) (typed FeaturePython)
  Dunit = g/cm3
  Dvalue = 10.5
  Group = -> [Ag_element006]
  conduct = 2
  density = 1
  expand = 3
  formula = Ag
  name = G4_Ag
  specific = 4
FEATURE [App::DocumentObjectGroupPython] Cd_element003  label="Cd_element : 003"  # scripted group (container) (typed FeaturePython)
  n = 1
  ref = Cd_element
FEATURE [App::DocumentObjectGroupPython] G4_Cd  # scripted group (container) (typed FeaturePython)
  Dunit = g/cm3
  Dvalue = 8.65
  Group = -> [Cd_element003]
  conduct = 2
  density = 1
  expand = 3
  formula = Cd
  name = G4_Cd
  specific = 4
FEATURE [App::DocumentObjectGroupPython] In_element001  label="In_element : 1"  # scripted group (container) (typed FeaturePython)
  n = 1
  ref = In_element
FEATURE [App::DocumentObjectGroupPython] G4_In  # scripted group (container) (typed FeaturePython)
  Dunit = g/cm3
  Dvalue = 7.31
  Group = -> [In_element001]
  conduct = 2
  density = 1
  expand = 3
  formula = In
  name = G4_In
  specific = 4
FEATURE [App::DocumentObjectGroupPython] Sn_element001  label="Sn_element : 1"  # scripted group (container) (typed FeaturePython)
  n = 1
  ref = Sn_element
FEATURE [App::DocumentObjectGroupPython] G4_Sn  # scripted group (container) (typed FeaturePython)
  Dunit = g/cm3
  Dvalue = 7.31
  Group = -> [Sn_element001]
  conduct = 2
  density = 1
  expand = 3
  formula = Sn
  name = G4_Sn
  specific = 4
FEATURE [App::DocumentObjectGroupPython] Sb_element001  label="Sb_element : 1"  # scripted group (container) (typed FeaturePython)
  n = 1
  ref = Sb_element
FEATURE [App::DocumentObjectGroupPython] G4_Sb  # scripted group (container) (typed FeaturePython)
  Dunit = g/cm3
  Dvalue = 6.691
  Group = -> [Sb_element001]
  conduct = 2
  density = 1
  expand = 3
  formula = Sb
  name = G4_Sb
  specific = 4
FEATURE [App::DocumentObjectGroupPython] Te_element002  label="Te_element : 002"  # scripted group (container) (typed FeaturePython)
  n = 1
  ref = Te_element
FEATURE [App::DocumentObjectGroupPython] G4_Te  # scripted group (container) (typed FeaturePython)
  Dunit = g/cm3
  Dvalue = 6.24
  Group = -> [Te_element002]
  conduct = 2
  density = 1
  expand = 3
  formula = Te
  name = G4_Te
  specific = 4
FEATURE [App::DocumentObjectGroupPython] I_element010  label="I_element : 006"  # scripted group (container) (typed FeaturePython)
  n = 1
  ref = I_element
FEATURE [App::DocumentObjectGroupPython] G4_I  # scripted group (container) (typed FeaturePython)
  Dunit = g/cm3
  Dvalue = 4.93
  Group = -> [I_element010]
  conduct = 2
  density = 1
  expand = 3
  formula = I
  name = G4_I
  specific = 4
FEATURE [App::DocumentObjectGroupPython] Xe_element001  label="Xe_element : 1"  # scripted group (container) (typed FeaturePython)
  n = 1
  ref = Xe_element
FEATURE [App::DocumentObjectGroupPython] G4_Xe  # scripted group (container) (typed FeaturePython)
  Dunit = g/cm3
  Dvalue = 0.00548536
  Group = -> [Xe_element001]
  conduct = 2
  density = 1
  expand = 3
  formula = Xe
  name = G4_Xe
  specific = 4
FEATURE [App::DocumentObjectGroupPython] Cs_element003  label="Cs_element : 003"  # scripted group (container) (typed FeaturePython)
  n = 1
  ref = Cs_element
FEATURE [App::DocumentObjectGroupPython] G4_Cs  # scripted group (container) (typed FeaturePython)
  Dunit = g/cm3
  Dvalue = 1.873
  Group = -> [Cs_element003]
  conduct = 2
  density = 1
  expand = 3
  formula = Cs
  name = G4_Cs
  specific = 4
FEATURE [App::DocumentObjectGroupPython] Ba_element003  label="Ba_element : 003"  # scripted group (container) (typed FeaturePython)
  n = 1
  ref = Ba_element
FEATURE [App::DocumentObjectGroupPython] G4_Ba  # scripted group (container) (typed FeaturePython)
  Dunit = g/cm3
  Dvalue = 3.5
  Group = -> [Ba_element003]
  conduct = 2
  density = 1
  expand = 3
  formula = Ba
  name = G4_Ba
  specific = 4
FEATURE [App::DocumentObjectGroupPython] La_element003  label="La_element : 003"  # scripted group (container) (typed FeaturePython)
  n = 1
  ref = La_element
FEATURE [App::DocumentObjectGroupPython] G4_La  # scripted group (container) (typed FeaturePython)
  Dunit = g/cm3
  Dvalue = 6.154
  Group = -> [La_element003]
  conduct = 2
  density = 1
  expand = 3
  formula = La
  name = G4_La
  specific = 4
FEATURE [App::DocumentObjectGroupPython] Ce_element002  label="Ce_element : 1"  # scripted group (container) (typed FeaturePython)
  n = 1
  ref = Ce_element
FEATURE [App::DocumentObjectGroupPython] G4_Ce  # scripted group (container) (typed FeaturePython)
  Dunit = g/cm3
  Dvalue = 6.657
  Group = -> [Ce_element002]
  conduct = 2
  density = 1
  expand = 3
  formula = Ce
  name = G4_Ce
  specific = 4
FEATURE [App::DocumentObjectGroupPython] Pr_element001  label="Pr_element : 1"  # scripted group (container) (typed FeaturePython)
  n = 1
  ref = Pr_element
FEATURE [App::DocumentObjectGroupPython] G4_Pr  # scripted group (container) (typed FeaturePython)
  Dunit = g/cm3
  Dvalue = 6.71
  Group = -> [Pr_element001]
  conduct = 2
  density = 1
  expand = 3
  formula = Pr
  name = G4_Pr
  specific = 4
FEATURE [App::DocumentObjectGroupPython] Nd_element001  label="Nd_element : 1"  # scripted group (container) (typed FeaturePython)
  n = 1
  ref = Nd_element
FEATURE [App::DocumentObjectGroupPython] G4_Nd  # scripted group (container) (typed FeaturePython)
  Dunit = g/cm3
  Dvalue = 6.9
  Group = -> [Nd_element001]
  conduct = 2
  density = 1
  expand = 3
  formula = Nd
  name = G4_Nd
  specific = 4
FEATURE [App::DocumentObjectGroupPython] Pm_element001  label="Pm_element : 1"  # scripted group (container) (typed FeaturePython)
  n = 1
  ref = Pm_element
FEATURE [App::DocumentObjectGroupPython] G4_Pm  # scripted group (container) (typed FeaturePython)
  Dunit = g/cm3
  Dvalue = 7.22
  Group = -> [Pm_element001]
  conduct = 2
  density = 1
  expand = 3
  formula = Pm
  name = G4_Pm
  specific = 4
FEATURE [App::DocumentObjectGroupPython] Sm_element001  label="Sm_element : 1"  # scripted group (container) (typed FeaturePython)
  n = 1
  ref = Sm_element
FEATURE [App::DocumentObjectGroupPython] G4_Sm  # scripted group (container) (typed FeaturePython)
  Dunit = g/cm3
  Dvalue = 7.46
  Group = -> [Sm_element001]
  conduct = 2
  density = 1
  expand = 3
  formula = Sm
  name = G4_Sm
  specific = 4
FEATURE [App::DocumentObjectGroupPython] Eu_element001  label="Eu_element : 1"  # scripted group (container) (typed FeaturePython)
  n = 1
  ref = Eu_element
FEATURE [App::DocumentObjectGroupPython] G4_Eu  # scripted group (container) (typed FeaturePython)
  Dunit = g/cm3
  Dvalue = 5.243
  Group = -> [Eu_element001]
  conduct = 2
  density = 1
  expand = 3
  formula = Eu
  name = G4_Eu
  specific = 4
FEATURE [App::DocumentObjectGroupPython] Gd_element002  label="Gd_element : 1"  # scripted group (container) (typed FeaturePython)
  n = 1
  ref = Gd_element
FEATURE [App::DocumentObjectGroupPython] G4_Gd  # scripted group (container) (typed FeaturePython)
  Dunit = g/cm3
  Dvalue = 7.9004
  Group = -> [Gd_element002]
  conduct = 2
  density = 1
  expand = 3
  formula = Gd
  name = G4_Gd
  specific = 4
FEATURE [App::DocumentObjectGroupPython] Tb_element001  label="Tb_element : 1"  # scripted group (container) (typed FeaturePython)
  n = 1
  ref = Tb_element
FEATURE [App::DocumentObjectGroupPython] G4_Tb  # scripted group (container) (typed FeaturePython)
  Dunit = g/cm3
  Dvalue = 8.229
  Group = -> [Tb_element001]
  conduct = 2
  density = 1
  expand = 3
  formula = Tb
  name = G4_Tb
  specific = 4
FEATURE [App::DocumentObjectGroupPython] Dy_element001  label="Dy_element : 1"  # scripted group (container) (typed FeaturePython)
  n = 1
  ref = Dy_element
FEATURE [App::DocumentObjectGroupPython] G4_Dy  # scripted group (container) (typed FeaturePython)
  Dunit = g/cm3
  Dvalue = 8.55
  Group = -> [Dy_element001]
  conduct = 2
  density = 1
  expand = 3
  formula = Dy
  name = G4_Dy
  specific = 4
FEATURE [App::DocumentObjectGroupPython] Ho_element001  label="Ho_element : 1"  # scripted group (container) (typed FeaturePython)
  n = 1
  ref = Ho_element
FEATURE [App::DocumentObjectGroupPython] G4_Ho  # scripted group (container) (typed FeaturePython)
  Dunit = g/cm3
  Dvalue = 8.795
  Group = -> [Ho_element001]
  conduct = 2
  density = 1
  expand = 3
  formula = Ho
  name = G4_Ho
  specific = 4
FEATURE [App::DocumentObjectGroupPython] Er_element001  label="Er_element : 1"  # scripted group (container) (typed FeaturePython)
  n = 1
  ref = Er_element
FEATURE [App::DocumentObjectGroupPython] G4_Er  # scripted group (container) (typed FeaturePython)
  Dunit = g/cm3
  Dvalue = 9.066
  Group = -> [Er_element001]
  conduct = 2
  density = 1
  expand = 3
  formula = Er
  name = G4_Er
  specific = 4
FEATURE [App::DocumentObjectGroupPython] Tm_element001  label="Tm_element : 1"  # scripted group (container) (typed FeaturePython)
  n = 1
  ref = Tm_element
FEATURE [App::DocumentObjectGroupPython] G4_Tm  # scripted group (container) (typed FeaturePython)
  Dunit = g/cm3
  Dvalue = 9.321
  Group = -> [Tm_element001]
  conduct = 2
  density = 1
  expand = 3
  formula = Tm
  name = G4_Tm
  specific = 4
FEATURE [App::DocumentObjectGroupPython] Yb_element001  label="Yb_element : 1"  # scripted group (container) (typed FeaturePython)
  n = 1
  ref = Yb_element
FEATURE [App::DocumentObjectGroupPython] G4_Yb  # scripted group (container) (typed FeaturePython)
  Dunit = g/cm3
  Dvalue = 6.73
  Group = -> [Yb_element001]
  conduct = 2
  density = 1
  expand = 3
  formula = Yb
  name = G4_Yb
  specific = 4
FEATURE [App::DocumentObjectGroupPython] Lu_element001  label="Lu_element : 1"  # scripted group (container) (typed FeaturePython)
  n = 1
  ref = Lu_element
FEATURE [App::DocumentObjectGroupPython] G4_Lu  # scripted group (container) (typed FeaturePython)
  Dunit = g/cm3
  Dvalue = 9.84
  Group = -> [Lu_element001]
  conduct = 2
  density = 1
  expand = 3
  formula = Lu
  name = G4_Lu
  specific = 4
FEATURE [App::DocumentObjectGroupPython] Hf_element001  label="Hf_element : 1"  # scripted group (container) (typed FeaturePython)
  n = 1
  ref = Hf_element
FEATURE [App::DocumentObjectGroupPython] G4_Hf  # scripted group (container) (typed FeaturePython)
  Dunit = g/cm3
  Dvalue = 13.31
  Group = -> [Hf_element001]
  conduct = 2
  density = 1
  expand = 3
  formula = Hf
  name = G4_Hf
  specific = 4
FEATURE [App::DocumentObjectGroupPython] Ta_element001  label="Ta_element : 1"  # scripted group (container) (typed FeaturePython)
  n = 1
  ref = Ta_element
FEATURE [App::DocumentObjectGroupPython] G4_Ta  # scripted group (container) (typed FeaturePython)
  Dunit = g/cm3
  Dvalue = 16.654
  Group = -> [Ta_element001]
  conduct = 2
  density = 1
  expand = 3
  formula = Ta
  name = G4_Ta
  specific = 4
FEATURE [App::DocumentObjectGroupPython] W_element004  label="W_element : 004"  # scripted group (container) (typed FeaturePython)
  n = 1
  ref = W_element
FEATURE [App::DocumentObjectGroupPython] G4_W  # scripted group (container) (typed FeaturePython)
  Dunit = g/cm3
  Dvalue = 19.3
  Group = -> [W_element004]
  conduct = 2
  density = 1
  expand = 3
  formula = W
  name = G4_W
  specific = 4
FEATURE [App::DocumentObjectGroupPython] Re_element001  label="Re_element : 1"  # scripted group (container) (typed FeaturePython)
  n = 1
  ref = Re_element
FEATURE [App::DocumentObjectGroupPython] G4_Re  # scripted group (container) (typed FeaturePython)
  Dunit = g/cm3
  Dvalue = 21.02
  Group = -> [Re_element001]
  conduct = 2
  density = 1
  expand = 3
  formula = Re
  name = G4_Re
  specific = 4
FEATURE [App::DocumentObjectGroupPython] Os_element001  label="Os_element : 1"  # scripted group (container) (typed FeaturePython)
  n = 1
  ref = Os_element
FEATURE [App::DocumentObjectGroupPython] G4_Os  # scripted group (container) (typed FeaturePython)
  Dunit = g/cm3
  Dvalue = 22.57
  Group = -> [Os_element001]
  conduct = 2
  density = 1
  expand = 3
  formula = Os
  name = G4_Os
  specific = 4
FEATURE [App::DocumentObjectGroupPython] Ir_element001  label="Ir_element : 1"  # scripted group (container) (typed FeaturePython)
  n = 1
  ref = Ir_element
FEATURE [App::DocumentObjectGroupPython] G4_Ir  # scripted group (container) (typed FeaturePython)
  Dunit = g/cm3
  Dvalue = 22.42
  Group = -> [Ir_element001]
  conduct = 2
  density = 1
  expand = 3
  formula = Ir
  name = G4_Ir
  specific = 4
FEATURE [App::DocumentObjectGroupPython] Pt_element001  label="Pt_element : 1"  # scripted group (container) (typed FeaturePython)
  n = 1
  ref = Pt_element
FEATURE [App::DocumentObjectGroupPython] G4_Pt  # scripted group (container) (typed FeaturePython)
  Dunit = g/cm3
  Dvalue = 21.45
  Group = -> [Pt_element001]
  conduct = 2
  density = 1
  expand = 3
  formula = Pt
  name = G4_Pt
  specific = 4
FEATURE [App::DocumentObjectGroupPython] Au_element001  label="Au_element : 1"  # scripted group (container) (typed FeaturePython)
  n = 1
  ref = Au_element
FEATURE [App::DocumentObjectGroupPython] G4_Au  # scripted group (container) (typed FeaturePython)
  Dunit = g/cm3
  Dvalue = 19.32
  Group = -> [Au_element001]
  conduct = 2
  density = 1
  expand = 3
  formula = Au
  name = G4_Au
  specific = 4
FEATURE [App::DocumentObjectGroupPython] Hg_element002  label="Hg_element : 002"  # scripted group (container) (typed FeaturePython)
  n = 1
  ref = Hg_element
FEATURE [App::DocumentObjectGroupPython] G4_Hg  # scripted group (container) (typed FeaturePython)
  Dunit = g/cm3
  Dvalue = 13.546
  Group = -> [Hg_element002]
  conduct = 2
  density = 1
  expand = 3
  formula = Hg
  name = G4_Hg
  specific = 4
FEATURE [App::DocumentObjectGroupPython] Tl_element002  label="Tl_element : 002"  # scripted group (container) (typed FeaturePython)
  n = 1
  ref = Tl_element
FEATURE [App::DocumentObjectGroupPython] G4_Tl  # scripted group (container) (typed FeaturePython)
  Dunit = g/cm3
  Dvalue = 11.72
  Group = -> [Tl_element002]
  conduct = 2
  density = 1
  expand = 3
  formula = Tl
  name = G4_Tl
  specific = 4
FEATURE [App::DocumentObjectGroupPython] Pb_element003  label="Pb_element : 1"  # scripted group (container) (typed FeaturePython)
  n = 1
  ref = Pb_element
FEATURE [App::DocumentObjectGroupPython] G4_Pb  # scripted group (container) (typed FeaturePython)
  Dunit = g/cm3
  Dvalue = 11.35
  Group = -> [Pb_element003]
  conduct = 2
  density = 1
  expand = 3
  formula = Pb
  name = G4_Pb
  specific = 4
FEATURE [App::DocumentObjectGroupPython] Bi_element002  label="Bi_element : 1"  # scripted group (container) (typed FeaturePython)
  n = 1
  ref = Bi_element
FEATURE [App::DocumentObjectGroupPython] G4_Bi  # scripted group (container) (typed FeaturePython)
  Dunit = g/cm3
  Dvalue = 9.747
  Group = -> [Bi_element002]
  conduct = 2
  density = 1
  expand = 3
  formula = Bi
  name = G4_Bi
  specific = 4
FEATURE [App::DocumentObjectGroupPython] Po_element001  label="Po_element : 1"  # scripted group (container) (typed FeaturePython)
  n = 1
  ref = Po_element
FEATURE [App::DocumentObjectGroupPython] G4_Po  # scripted group (container) (typed FeaturePython)
  Dunit = g/cm3
  Dvalue = 9.32
  Group = -> [Po_element001]
  conduct = 2
  density = 1
  expand = 3
  formula = Po
  name = G4_Po
  specific = 4
FEATURE [App::DocumentObjectGroupPython] At_element001  label="At_element : 1"  # scripted group (container) (typed FeaturePython)
  n = 1
  ref = At_element
FEATURE [App::DocumentObjectGroupPython] G4_At  # scripted group (container) (typed FeaturePython)
  Dunit = g/cm3
  Dvalue = 9.32
  Group = -> [At_element001]
  conduct = 2
  density = 1
  expand = 3
  formula = At
  name = G4_At
  specific = 4
FEATURE [App::DocumentObjectGroupPython] Rn_element001  label="Rn_element : 1"  # scripted group (container) (typed FeaturePython)
  n = 1
  ref = Rn_element
FEATURE [App::DocumentObjectGroupPython] G4_Rn  # scripted group (container) (typed FeaturePython)
  Dunit = g/cm3
  Dvalue = 0.00900662
  Group = -> [Rn_element001]
  conduct = 2
  density = 1
  expand = 3
  formula = Rn
  name = G4_Rn
  specific = 4
FEATURE [App::DocumentObjectGroupPython] Fr_element001  label="Fr_element : 1"  # scripted group (container) (typed FeaturePython)
  n = 1
  ref = Fr_element
FEATURE [App::DocumentObjectGroupPython] G4_Fr  # scripted group (container) (typed FeaturePython)
  Dunit = g/cm3
  Dvalue = 1
  Group = -> [Fr_element001]
  conduct = 2
  density = 1
  expand = 3
  formula = Fr
  name = G4_Fr
  specific = 4
FEATURE [App::DocumentObjectGroupPython] Ra_element001  label="Ra_element : 1"  # scripted group (container) (typed FeaturePython)
  n = 1
  ref = Ra_element
FEATURE [App::DocumentObjectGroupPython] G4_Ra  # scripted group (container) (typed FeaturePython)
  Dunit = g/cm3
  Dvalue = 5
  Group = -> [Ra_element001]
  conduct = 2
  density = 1
  expand = 3
  formula = Ra
  name = G4_Ra
  specific = 4
FEATURE [App::DocumentObjectGroupPython] Ac_element001  label="Ac_element : 1"  # scripted group (container) (typed FeaturePython)
  n = 1
  ref = Ac_element
FEATURE [App::DocumentObjectGroupPython] G4_Ac  # scripted group (container) (typed FeaturePython)
  Dunit = g/cm3
  Dvalue = 10.07
  Group = -> [Ac_element001]
  conduct = 2
  density = 1
  expand = 3
  formula = Ac
  name = G4_Ac
  specific = 4
FEATURE [App::DocumentObjectGroupPython] Th_element001  label="Th_element : 1"  # scripted group (container) (typed FeaturePython)
  n = 1
  ref = Th_element
FEATURE [App::DocumentObjectGroupPython] G4_Th  # scripted group (container) (typed FeaturePython)
  Dunit = g/cm3
  Dvalue = 11.72
  Group = -> [Th_element001]
  conduct = 2
  density = 1
  expand = 3
  formula = Th
  name = G4_Th
  specific = 4
FEATURE [App::DocumentObjectGroupPython] Pa_element001  label="Pa_element : 1"  # scripted group (container) (typed FeaturePython)
  n = 1
  ref = Pa_element
FEATURE [App::DocumentObjectGroupPython] G4_Pa  # scripted group (container) (typed FeaturePython)
  Dunit = g/cm3
  Dvalue = 15.37
  Group = -> [Pa_element001]
  conduct = 2
  density = 1
  expand = 3
  formula = Pa
  name = G4_Pa
  specific = 4
FEATURE [App::DocumentObjectGroupPython] U_element004  label="U_element : 004"  # scripted group (container) (typed FeaturePython)
  n = 1
  ref = U_element
FEATURE [App::DocumentObjectGroupPython] G4_U  # scripted group (container) (typed FeaturePython)
  Dunit = g/cm3
  Dvalue = 18.95
  Group = -> [U_element004]
  conduct = 2
  density = 1
  expand = 3
  formula = U
  name = G4_U
  specific = 4
FEATURE [App::DocumentObjectGroupPython] Np_element001  label="Np_element : 1"  # scripted group (container) (typed FeaturePython)
  n = 1
  ref = Np_element
FEATURE [App::DocumentObjectGroupPython] G4_Np  # scripted group (container) (typed FeaturePython)
  Dunit = g/cm3
  Dvalue = 20.25
  Group = -> [Np_element001]
  conduct = 2
  density = 1
  expand = 3
  formula = Np
  name = G4_Np
  specific = 4
FEATURE [App::DocumentObjectGroupPython] Pu_element002  label="Pu_element : 002"  # scripted group (container) (typed FeaturePython)
  n = 1
  ref = Pu_element
FEATURE [App::DocumentObjectGroupPython] G4_Pu  # scripted group (container) (typed FeaturePython)
  Dunit = g/cm3
  Dvalue = 19.84
  Group = -> [Pu_element002]
  conduct = 2
  density = 1
  expand = 3
  formula = Pu
  name = G4_Pu
  specific = 4
FEATURE [App::DocumentObjectGroupPython] Am_element001  label="Am_element : 1"  # scripted group (container) (typed FeaturePython)
  n = 1
  ref = Am_element
FEATURE [App::DocumentObjectGroupPython] G4_Am  # scripted group (container) (typed FeaturePython)
  Dunit = g/cm3
  Dvalue = 13.67
  Group = -> [Am_element001]
  conduct = 2
  density = 1
  expand = 3
  formula = Am
  name = G4_Am
  specific = 4
FEATURE [App::DocumentObjectGroupPython] Cm_element001  label="Cm_element : 1"  # scripted group (container) (typed FeaturePython)
  n = 1
  ref = Cm_element
FEATURE [App::DocumentObjectGroupPython] G4_Cm  # scripted group (container) (typed FeaturePython)
  Dunit = g/cm3
  Dvalue = 13.51
  Group = -> [Cm_element001]
  conduct = 2
  density = 1
  expand = 3
  formula = Cm
  name = G4_Cm
  specific = 4
FEATURE [App::DocumentObjectGroupPython] Bk_element001  label="Bk_element : 1"  # scripted group (container) (typed FeaturePython)
  n = 1
  ref = Bk_element
FEATURE [App::DocumentObjectGroupPython] G4_Bk  # scripted group (container) (typed FeaturePython)
  Dunit = g/cm3
  Dvalue = 14
  Group = -> [Bk_element001]
  conduct = 2
  density = 1
  expand = 3
  formula = Bk
  name = G4_Bk
  specific = 4
FEATURE [App::DocumentObjectGroupPython] Cf_element001  label="Cf_element : 1"  # scripted group (container) (typed FeaturePython)
  n = 1
  ref = Cf_element
FEATURE [App::DocumentObjectGroupPython] G4_Cf  # scripted group (container) (typed FeaturePython)
  Dunit = g/cm3
  Dvalue = 10
  Group = -> [Cf_element001]
  conduct = 2
  density = 1
  expand = 3
  formula = Cf
  name = G4_Cf
  specific = 4
FEATURE [App::DocumentObjectGroupPython] Element  # scripted group (container) (typed FeaturePython)
  Group = -> [G4_H,G4_He,G4_Li,G4_Be,G4_B,G4_C,G4_N,G4_O,G4_F,G4_Ne,G4_Na,G4_Mg,G4_Al,G4_Si,G4_P,G4_S,G4_Cl,G4_Ar,G4_K,G4_Ca,G4_Sc,G4_Ti,G4_V,G4_Cr,G4_Mn,G4_Fe,G4_Co,G4_Ni,G4_Cu,G4_Zn,G4_Ga,G4_Ge,G4_As,G4_Se,G4_Br,G4_Kr,G4_Rb,G4_Sr,G4_Y,G4_Zr,G4_Nb,G4_Mo,G4_Tc,G4_Ru,G4_Rh,G4_Pd,G4_Ag,G4_Cd,G4_In,G4_Sn,G4_Sb,G4_Te,G4_I,G4_Xe,G4_Cs,G4_Ba,G4_La,G4_Ce,G4_Pr,G4_Nd,G4_Pm,G4_Sm,G4_Eu,G4_Gd,G4_Tb,G4_Dy,G4_Ho,G4_Er,+30 more]
FEATURE [App::DocumentObjectGroupPython] H_element114  label="H_element : 063"  # scripted group (container) (typed FeaturePython)
  n = 2
  ref = H_element
FEATURE [App::DocumentObjectGroupPython] G4_lH2  # scripted group (container) (typed FeaturePython)
  Dunit = g/cm3
  Dvalue = 0.0708
  Group = -> [H_element114]
  conduct = 2
  density = 1
  expand = 3
  formula = G4_lH2
  name = G4_lH2
  specific = 4
FEATURE [App::DocumentObjectGroupPython] N_element049  label="N_element : 022"  # scripted group (container) (typed FeaturePython)
  n = 2
  ref = N_element
FEATURE [App::DocumentObjectGroupPython] G4_lN2  # scripted group (container) (typed FeaturePython)
  Dunit = g/cm3
  Dvalue = 0.807
  Group = -> [N_element049]
  conduct = 2
  density = 1
  expand = 3
  formula = G4_lN2
  name = G4_lN2
  specific = 4
FEATURE [App::DocumentObjectGroupPython] O_element106  label="O_element : 060"  # scripted group (container) (typed FeaturePython)
  n = 2
  ref = O_element
FEATURE [App::DocumentObjectGroupPython] G4_lO2  # scripted group (container) (typed FeaturePython)
  Dunit = g/cm3
  Dvalue = 1.141
  Group = -> [O_element106]
  conduct = 2
  density = 1
  expand = 3
  formula = G4_lO2
  name = G4_lO2
  specific = 4
FEATURE [App::DocumentObjectGroupPython] Ar  label="Ar : 1"  # scripted group (container) (typed FeaturePython)
  n = 1
  ref = Ar
FEATURE [App::DocumentObjectGroupPython] G4_lAr  # scripted group (container) (typed FeaturePython)
  Dunit = g/cm3
  Dvalue = 1.396
  Group = -> [Ar]
  conduct = 2
  density = 1
  expand = 3
  formula = G4_lAr
  name = G4_lAr
  specific = 4
FEATURE [App::DocumentObjectGroupPython] Br  label="Br : 1"  # scripted group (container) (typed FeaturePython)
  n = 1
  ref = Br
FEATURE [App::DocumentObjectGroupPython] G4_lBr  # scripted group (container) (typed FeaturePython)
  Dunit = g/cm3
  Dvalue = 3.1028
  Group = -> [Br]
  conduct = 2
  density = 1
  expand = 3
  formula = G4_lBr
  name = G4_lBr
  specific = 4
FEATURE [App::DocumentObjectGroupPython] Kr  label="Kr : 1"  # scripted group (container) (typed FeaturePython)
  n = 1
  ref = Kr
FEATURE [App::DocumentObjectGroupPython] G4_lKr  # scripted group (container) (typed FeaturePython)
  Dunit = g/cm3
  Dvalue = 2.418
  Group = -> [Kr]
  conduct = 2
  density = 1
  expand = 3
  formula = G4_lKr
  name = G4_lKr
  specific = 4
FEATURE [App::DocumentObjectGroupPython] Xe  label="Xe : 1"  # scripted group (container) (typed FeaturePython)
  n = 1
  ref = Xe
FEATURE [App::DocumentObjectGroupPython] G4_lXe  # scripted group (container) (typed FeaturePython)
  Dunit = g/cm3
  Dvalue = 2.953
  Group = -> [Xe]
  conduct = 2
  density = 1
  expand = 3
  formula = G4_lXe
  name = G4_lXe
  specific = 4
FEATURE [App::DocumentObjectGroupPython] O_element107  label="O_element : 061"  # scripted group (container) (typed FeaturePython)
  n = 4
  ref = O_element
FEATURE [App::DocumentObjectGroupPython] Pb_element004  label="Pb_element : 002"  # scripted group (container) (typed FeaturePython)
  n = 1
  ref = Pb_element
FEATURE [App::DocumentObjectGroupPython] W_element005  label="W_element : 005"  # scripted group (container) (typed FeaturePython)
  n = 1
  ref = W_element
FEATURE [App::DocumentObjectGroupPython] G4_PbWO4  # scripted group (container) (typed FeaturePython)
  Dunit = g/cm3
  Dvalue = 8.28
  Group = -> [O_element107,Pb_element004,W_element005]
  conduct = 2
  density = 1
  expand = 3
  formula = G4_PbWO4
  name = G4_PbWO4
  specific = 4
FEATURE [App::DocumentObjectGroupPython] alactic  label="alactic : 1"  # scripted group (container) (typed FeaturePython)
  n = 1
  ref = alactic
FEATURE [App::DocumentObjectGroupPython] G4_Galactic  # scripted group (container) (typed FeaturePython)
  Dunit = g/cm3
  Dvalue = 0
  Group = -> [alactic]
  conduct = 2
  density = 1
  expand = 3
  formula = G4_Galactic
  name = G4_Galactic
  specific = 4
FEATURE [App::DocumentObjectGroupPython] RAPHITE_POROUS  label="RAPHITE_POROUS : 1"  # scripted group (container) (typed FeaturePython)
  n = 1
  ref = RAPHITE_POROUS
FEATURE [App::DocumentObjectGroupPython] G4_GRAPHITE_POROUS  # scripted group (container) (typed FeaturePython)
  Dunit = g/cm3
  Dvalue = 1.7
  Group = -> [RAPHITE_POROUS]
  conduct = 2
  density = 1
  expand = 3
  formula = G4_GRAPHITE_POROUS
  name = G4_GRAPHITE_POROUS
  specific = 4
FEATURE [App::DocumentObjectGroupPython] H_element115  label="H_element : 0.150"  # scripted group (container) (typed FeaturePython)
  n = 0.080538
FEATURE [App::DocumentObjectGroupPython] C_element125  label="C_element : 0.600"  # scripted group (container) (typed FeaturePython)
  n = 0.599848
FEATURE [App::DocumentObjectGroupPython] O_element108  label="O_element : 0.320"  # scripted group (container) (typed FeaturePython)
  n = 0.319614
FEATURE [App::DocumentObjectGroupPython] G4_LUCITE  # scripted group (container) (typed FeaturePython)
  Dunit = g/cm3
  Dvalue = 1.19
  Group = -> [H_element115,C_element125,O_element108]
  conduct = 2
  density = 1
  expand = 3
  formula = G4_LUCITE
  name = G4_LUCITE
  specific = 4
FEATURE [App::DocumentObjectGroupPython] Cu_element002  label="Cu_element : 62"  # scripted group (container) (typed FeaturePython)
  n = 62
  ref = Cu_element
FEATURE [App::DocumentObjectGroupPython] Zn_element002  label="Zn_element : 35"  # scripted group (container) (typed FeaturePython)
  n = 35
  ref = Zn_element
FEATURE [App::DocumentObjectGroupPython] Pb_element005  label="Pb_element : 3"  # scripted group (container) (typed FeaturePython)
  n = 3
  ref = Pb_element
FEATURE [App::DocumentObjectGroupPython] G4_BRASS  # scripted group (container) (typed FeaturePython)
  Dunit = g/cm3
  Dvalue = 8.52
  Group = -> [Cu_element002,Zn_element002,Pb_element005]
  conduct = 2
  density = 1
  expand = 3
  formula = G4_BRASS
  name = G4_BRASS
  specific = 4
FEATURE [App::DocumentObjectGroupPython] Cu_element003  label="Cu_element : 89"  # scripted group (container) (typed FeaturePython)
  n = 89
  ref = Cu_element
FEATURE [App::DocumentObjectGroupPython] Zn_element003  label="Zn_element : 9"  # scripted group (container) (typed FeaturePython)
  n = 9
  ref = Zn_element
FEATURE [App::DocumentObjectGroupPython] Pb_element006  label="Pb_element : 2"  # scripted group (container) (typed FeaturePython)
  n = 2
  ref = Pb_element
FEATURE [App::DocumentObjectGroupPython] G4_BRONZE  # scripted group (container) (typed FeaturePython)
  Dunit = g/cm3
  Dvalue = 8.82
  Group = -> [Cu_element003,Zn_element003,Pb_element006]
  conduct = 2
  density = 1
  expand = 3
  formula = G4_BRONZE
  name = G4_BRONZE
  specific = 4
FEATURE [App::DocumentObjectGroupPython] Fe_element008  label="Fe_element : 74"  # scripted group (container) (typed FeaturePython)
  n = 74
  ref = Fe_element
FEATURE [App::DocumentObjectGroupPython] Cr_element002  label="Cr_element : 18"  # scripted group (container) (typed FeaturePython)
  n = 18
  ref = Cr_element
FEATURE [App::DocumentObjectGroupPython] Ni_element002  label="Ni_element : 8"  # scripted group (container) (typed FeaturePython)
  n = 8
  ref = Ni_element
FEATURE [App::DocumentObjectGroupPython] G4_STAINLESS_STEEL  label="G4_STAINLESS-STEEL"  # scripted group (container) (typed FeaturePython)
  Dunit = g/cm3
  Dvalue = 8
  Group = -> [Fe_element008,Cr_element002,Ni_element002]
  conduct = 2
  density = 1
  expand = 3
  formula = G4_STAINLESS-STEEL
  name = G4_STAINLESS-STEEL
  specific = 4
FEATURE [App::DocumentObjectGroupPython] H_element116  label="H_element : 064"  # scripted group (container) (typed FeaturePython)
  n = 18
  ref = H_element
FEATURE [App::DocumentObjectGroupPython] C_element126  label="C_element : 071"  # scripted group (container) (typed FeaturePython)
  n = 12
  ref = C_element
FEATURE [App::DocumentObjectGroupPython] O_element109  label="O_element : 062"  # scripted group (container) (typed FeaturePython)
  n = 7
  ref = O_element
FEATURE [App::DocumentObjectGroupPython] G4_CR39  # scripted group (container) (typed FeaturePython)
  Dunit = g/cm3
  Dvalue = 1.32
  Group = -> [H_element116,C_element126,O_element109]
  conduct = 2
  density = 1
  expand = 3
  formula = G4_CR39
  name = G4_CR39
  specific = 4
FEATURE [App::DocumentObjectGroupPython] H_element117  label="H_element : 38"  # scripted group (container) (typed FeaturePython)
  n = 38
  ref = H_element
FEATURE [App::DocumentObjectGroupPython] C_element127  label="C_element : 072"  # scripted group (container) (typed FeaturePython)
  n = 18
  ref = C_element
FEATURE [App::DocumentObjectGroupPython] O_element110  label="O_element : 063"  # scripted group (container) (typed FeaturePython)
  n = 1
  ref = O_element
FEATURE [App::DocumentObjectGroupPython] G4_OCTADECANOL  # scripted group (container) (typed FeaturePython)
  Dunit = g/cm3
  Dvalue = 0.812
  Group = -> [H_element117,C_element127,O_element110]
  conduct = 2
  density = 1
  expand = 3
  formula = G4_OCTADECANOL
  name = G4_OCTADECANOL
  specific = 4
FEATURE [App::DocumentObjectGroupPython] HEP  # scripted group (container) (typed FeaturePython)
  Group = -> [G4_lH2,G4_lN2,G4_lO2,G4_lAr,G4_lBr,G4_lKr,G4_lXe,G4_PbWO4,G4_Galactic,G4_GRAPHITE_POROUS,G4_LUCITE,G4_BRASS,G4_BRONZE,G4_STAINLESS_STEEL,G4_CR39,G4_OCTADECANOL]
FEATURE [App::DocumentObjectGroupPython] C_element128  label="C_element : 073"  # scripted group (container) (typed FeaturePython)
  n = 14
  ref = C_element
FEATURE [App::DocumentObjectGroupPython] H_element118  label="H_element : 065"  # scripted group (container) (typed FeaturePython)
  n = 10
  ref = H_element
FEATURE [App::DocumentObjectGroupPython] O_element111  label="O_element : 064"  # scripted group (container) (typed FeaturePython)
  n = 2
  ref = O_element
FEATURE [App::DocumentObjectGroupPython] N_element050  label="N_element : 023"  # scripted group (container) (typed FeaturePython)
  n = 2
  ref = N_element
FEATURE [App::DocumentObjectGroupPython] G4_KEVLAR  # scripted group (container) (typed FeaturePython)
  Dunit = g/cm3
  Dvalue = 1.44
  Group = -> [C_element128,H_element118,O_element111,N_element050]
  conduct = 2
  density = 1
  expand = 3
  formula = G4_KEVLAR
  name = G4_KEVLAR
  specific = 4
FEATURE [App::DocumentObjectGroupPython] C_element129  label="C_element : 074"  # scripted group (container) (typed FeaturePython)
  n = 10
  ref = C_element
FEATURE [App::DocumentObjectGroupPython] H_element119  label="H_element : 066"  # scripted group (container) (typed FeaturePython)
  n = 8
  ref = H_element
FEATURE [App::DocumentObjectGroupPython] O_element112  label="O_element : 065"  # scripted group (container) (typed FeaturePython)
  n = 4
  ref = O_element
FEATURE [App::DocumentObjectGroupPython] G4_DACRON  # scripted group (container) (typed FeaturePython)
  Dunit = g/cm3
  Dvalue = 1.4
  Group = -> [C_element129,H_element119,O_element112]
  conduct = 2
  density = 1
  expand = 3
  formula = G4_DACRON
  name = G4_DACRON
  specific = 4
FEATURE [App::DocumentObjectGroupPython] C_element130  label="C_element : 075"  # scripted group (container) (typed FeaturePython)
  n = 4
  ref = C_element
FEATURE [App::DocumentObjectGroupPython] H_element120  label="H_element : 067"  # scripted group (container) (typed FeaturePython)
  n = 5
  ref = H_element
FEATURE [App::DocumentObjectGroupPython] Cl_element030  label="Cl_element : 016"  # scripted group (container) (typed FeaturePython)
  n = 1
  ref = Cl_element
FEATURE [App::DocumentObjectGroupPython] G4_NEOPRENE  # scripted group (container) (typed FeaturePython)
  Dunit = g/cm3
  Dvalue = 1.23
  Group = -> [C_element130,H_element120,Cl_element030]
  conduct = 2
  density = 1
  expand = 3
  formula = G4_NEOPRENE
  name = G4_NEOPRENE
  specific = 4
FEATURE [App::DocumentObjectGroupPython] Space  # scripted group (container) (typed FeaturePython)
  Group = -> [G4_KEVLAR,G4_DACRON,G4_NEOPRENE]
FEATURE [App::DocumentObjectGroupPython] H_element121  label="H_element : 068"  # scripted group (container) (typed FeaturePython)
  n = 5
  ref = H_element
FEATURE [App::DocumentObjectGroupPython] C_element131  label="C_element : 076"  # scripted group (container) (typed FeaturePython)
  n = 4
  ref = C_element
FEATURE [App::DocumentObjectGroupPython] N_element051  label="N_element : 3"  # scripted group (container) (typed FeaturePython)
  n = 3
  ref = N_element
FEATURE [App::DocumentObjectGroupPython] O_element113  label="O_element : 066"  # scripted group (container) (typed FeaturePython)
  n = 1
  ref = O_element
FEATURE [App::DocumentObjectGroupPython] G4_CYTOSINE  # scripted group (container) (typed FeaturePython)
  Dunit = g/cm3
  Dvalue = 1.55
  Group = -> [H_element121,C_element131,N_element051,O_element113]
  conduct = 2
  density = 1
  expand = 3
  formula = G4_CYTOSINE
  name = G4_CYTOSINE
  specific = 4
FEATURE [App::DocumentObjectGroupPython] H_element122  label="H_element : 069"  # scripted group (container) (typed FeaturePython)
  n = 6
  ref = H_element
FEATURE [App::DocumentObjectGroupPython] C_element132  label="C_element : 077"  # scripted group (container) (typed FeaturePython)
  n = 5
  ref = C_element
FEATURE [App::DocumentObjectGroupPython] N_element052  label="N_element : 024"  # scripted group (container) (typed FeaturePython)
  n = 2
  ref = N_element
FEATURE [App::DocumentObjectGroupPython] O_element114  label="O_element : 067"  # scripted group (container) (typed FeaturePython)
  n = 2
  ref = O_element
FEATURE [App::DocumentObjectGroupPython] G4_THYMINE  # scripted group (container) (typed FeaturePython)
  Dunit = g/cm3
  Dvalue = 1.23
  Group = -> [H_element122,C_element132,N_element052,O_element114]
  conduct = 2
  density = 1
  expand = 3
  formula = G4_THYMINE
  name = G4_THYMINE
  specific = 4
FEATURE [App::DocumentObjectGroupPython] H_element123  label="H_element : 070"  # scripted group (container) (typed FeaturePython)
  n = 4
  ref = H_element
FEATURE [App::DocumentObjectGroupPython] C_element133  label="C_element : 078"  # scripted group (container) (typed FeaturePython)
  n = 4
  ref = C_element
FEATURE [App::DocumentObjectGroupPython] N_element053  label="N_element : 025"  # scripted group (container) (typed FeaturePython)
  n = 2
  ref = N_element
FEATURE [App::DocumentObjectGroupPython] O_element115  label="O_element : 068"  # scripted group (container) (typed FeaturePython)
  n = 2
  ref = O_element
FEATURE [App::DocumentObjectGroupPython] G4_URACIL  # scripted group (container) (typed FeaturePython)
  Dunit = g/cm3
  Dvalue = 1.32
  Group = -> [H_element123,C_element133,N_element053,O_element115]
  conduct = 2
  density = 1
  expand = 3
  formula = G4_URACIL
  name = G4_URACIL
  specific = 4
FEATURE [App::DocumentObjectGroupPython] H_element124  label="H_element : 071"  # scripted group (container) (typed FeaturePython)
  n = 4
  ref = H_element
FEATURE [App::DocumentObjectGroupPython] C_element134  label="C_element : 079"  # scripted group (container) (typed FeaturePython)
  n = 5
  ref = C_element
FEATURE [App::DocumentObjectGroupPython] N_element054  label="N_element : 026"  # scripted group (container) (typed FeaturePython)
  n = 5
  ref = N_element
FEATURE [App::DocumentObjectGroupPython] G4_DNA_ADENINE  # scripted group (container) (typed FeaturePython)
  Dunit = g/cm3
  Dvalue = 1
  Group = -> [H_element124,C_element134,N_element054]
  conduct = 2
  density = 1
  expand = 3
  formula = G4_DNA_ADENINE
  name = G4_DNA_ADENINE
  specific = 4
FEATURE [App::DocumentObjectGroupPython] H_element125  label="H_element : 072"  # scripted group (container) (typed FeaturePython)
  n = 4
  ref = H_element
FEATURE [App::DocumentObjectGroupPython] C_element135  label="C_element : 080"  # scripted group (container) (typed FeaturePython)
  n = 5
  ref = C_element
FEATURE [App::DocumentObjectGroupPython] N_element055  label="N_element : 027"  # scripted group (container) (typed FeaturePython)
  n = 5
  ref = N_element
FEATURE [App::DocumentObjectGroupPython] O_element116  label="O_element : 069"  # scripted group (container) (typed FeaturePython)
  n = 1
  ref = O_element
FEATURE [App::DocumentObjectGroupPython] G4_DNA_GUANINE  # scripted group (container) (typed FeaturePython)
  Dunit = g/cm3
  Dvalue = 1
  Group = -> [H_element125,C_element135,N_element055,O_element116]
  conduct = 2
  density = 1
  expand = 3
  formula = G4_DNA_GUANINE
  name = G4_DNA_GUANINE
  specific = 4
FEATURE [App::DocumentObjectGroupPython] H_element126  label="H_element : 073"  # scripted group (container) (typed FeaturePython)
  n = 4
  ref = H_element
FEATURE [App::DocumentObjectGroupPython] C_element136  label="C_element : 081"  # scripted group (container) (typed FeaturePython)
  n = 4
  ref = C_element
FEATURE [App::DocumentObjectGroupPython] N_element056  label="N_element : 028"  # scripted group (container) (typed FeaturePython)
  n = 3
  ref = N_element
FEATURE [App::DocumentObjectGroupPython] O_element117  label="O_element : 070"  # scripted group (container) (typed FeaturePython)
  n = 1
  ref = O_element
FEATURE [App::DocumentObjectGroupPython] G4_DNA_CYTOSINE  # scripted group (container) (typed FeaturePython)
  Dunit = g/cm3
  Dvalue = 1
  Group = -> [H_element126,C_element136,N_element056,O_element117]
  conduct = 2
  density = 1
  expand = 3
  formula = G4_DNA_CYTOSINE
  name = G4_DNA_CYTOSINE
  specific = 4
FEATURE [App::DocumentObjectGroupPython] H_element127  label="H_element : 074"  # scripted group (container) (typed FeaturePython)
  n = 5
  ref = H_element
FEATURE [App::DocumentObjectGroupPython] C_element137  label="C_element : 082"  # scripted group (container) (typed FeaturePython)
  n = 5
  ref = C_element
FEATURE [App::DocumentObjectGroupPython] N_element057  label="N_element : 029"  # scripted group (container) (typed FeaturePython)
  n = 2
  ref = N_element
FEATURE [App::DocumentObjectGroupPython] O_element118  label="O_element : 071"  # scripted group (container) (typed FeaturePython)
  n = 2
  ref = O_element
FEATURE [App::DocumentObjectGroupPython] G4_DNA_THYMINE  # scripted group (container) (typed FeaturePython)
  Dunit = g/cm3
  Dvalue = 1
  Group = -> [H_element127,C_element137,N_element057,O_element118]
  conduct = 2
  density = 1
  expand = 3
  formula = G4_DNA_THYMINE
  name = G4_DNA_THYMINE
  specific = 4
FEATURE [App::DocumentObjectGroupPython] H_element128  label="H_element : 075"  # scripted group (container) (typed FeaturePython)
  n = 3
  ref = H_element
FEATURE [App::DocumentObjectGroupPython] C_element138  label="C_element : 083"  # scripted group (container) (typed FeaturePython)
  n = 4
  ref = C_element
FEATURE [App::DocumentObjectGroupPython] N_element058  label="N_element : 030"  # scripted group (container) (typed FeaturePython)
  n = 2
  ref = N_element
FEATURE [App::DocumentObjectGroupPython] O_element119  label="O_element : 072"  # scripted group (container) (typed FeaturePython)
  n = 2
  ref = O_element
FEATURE [App::DocumentObjectGroupPython] G4_DNA_URACIL  # scripted group (container) (typed FeaturePython)
  Dunit = g/cm3
  Dvalue = 1
  Group = -> [H_element128,C_element138,N_element058,O_element119]
  conduct = 2
  density = 1
  expand = 3
  formula = G4_DNA_URACIL
  name = G4_DNA_URACIL
  specific = 4
FEATURE [App::DocumentObjectGroupPython] H_element129  label="H_element : 076"  # scripted group (container) (typed FeaturePython)
  n = 10
  ref = H_element
FEATURE [App::DocumentObjectGroupPython] C_element139  label="C_element : 084"  # scripted group (container) (typed FeaturePython)
  n = 10
  ref = C_element
FEATURE [App::DocumentObjectGroupPython] N_element059  label="N_element : 031"  # scripted group (container) (typed FeaturePython)
  n = 5
  ref = N_element
FEATURE [App::DocumentObjectGroupPython] O_element120  label="O_element : 073"  # scripted group (container) (typed FeaturePython)
  n = 4
  ref = O_element
FEATURE [App::DocumentObjectGroupPython] G4_DNA_ADENOSINE  # scripted group (container) (typed FeaturePython)
  Dunit = g/cm3
  Dvalue = 1
  Group = -> [H_element129,C_element139,N_element059,O_element120]
  conduct = 2
  density = 1
  expand = 3
  formula = G4_DNA_ADENOSINE
  name = G4_DNA_ADENOSINE
  specific = 4
FEATURE [App::DocumentObjectGroupPython] H_element130  label="H_element : 077"  # scripted group (container) (typed FeaturePython)
  n = 10
  ref = H_element
FEATURE [App::DocumentObjectGroupPython] C_element140  label="C_element : 085"  # scripted group (container) (typed FeaturePython)
  n = 10
  ref = C_element
FEATURE [App::DocumentObjectGroupPython] N_element060  label="N_element : 032"  # scripted group (container) (typed FeaturePython)
  n = 5
  ref = N_element
FEATURE [App::DocumentObjectGroupPython] O_element121  label="O_element : 074"  # scripted group (container) (typed FeaturePython)
  n = 5
  ref = O_element
FEATURE [App::DocumentObjectGroupPython] G4_DNA_GUANOSINE  # scripted group (container) (typed FeaturePython)
  Dunit = g/cm3
  Dvalue = 1
  Group = -> [H_element130,C_element140,N_element060,O_element121]
  conduct = 2
  density = 1
  expand = 3
  formula = G4_DNA_GUANOSINE
  name = G4_DNA_GUANOSINE
  specific = 4
FEATURE [App::DocumentObjectGroupPython] H_element131  label="H_element : 078"  # scripted group (container) (typed FeaturePython)
  n = 10
  ref = H_element
FEATURE [App::DocumentObjectGroupPython] C_element141  label="C_element : 086"  # scripted group (container) (typed FeaturePython)
  n = 9
  ref = C_element
FEATURE [App::DocumentObjectGroupPython] N_element061  label="N_element : 033"  # scripted group (container) (typed FeaturePython)
  n = 3
  ref = N_element
FEATURE [App::DocumentObjectGroupPython] O_element122  label="O_element : 075"  # scripted group (container) (typed FeaturePython)
  n = 5
  ref = O_element
FEATURE [App::DocumentObjectGroupPython] G4_DNA_CYTIDINE  # scripted group (container) (typed FeaturePython)
  Dunit = g/cm3
  Dvalue = 1
  Group = -> [H_element131,C_element141,N_element061,O_element122]
  conduct = 2
  density = 1
  expand = 3
  formula = G4_DNA_CYTIDINE
  name = G4_DNA_CYTIDINE
  specific = 4
FEATURE [App::DocumentObjectGroupPython] H_element132  label="H_element : 079"  # scripted group (container) (typed FeaturePython)
  n = 9
  ref = H_element
FEATURE [App::DocumentObjectGroupPython] C_element142  label="C_element : 087"  # scripted group (container) (typed FeaturePython)
  n = 9
  ref = C_element
FEATURE [App::DocumentObjectGroupPython] N_element062  label="N_element : 034"  # scripted group (container) (typed FeaturePython)
  n = 2
  ref = N_element
FEATURE [App::DocumentObjectGroupPython] O_element123  label="O_element : 076"  # scripted group (container) (typed FeaturePython)
  n = 6
  ref = O_element
FEATURE [App::DocumentObjectGroupPython] G4_DNA_URIDINE  # scripted group (container) (typed FeaturePython)
  Dunit = g/cm3
  Dvalue = 1
  Group = -> [H_element132,C_element142,N_element062,O_element123]
  conduct = 2
  density = 1
  expand = 3
  formula = G4_DNA_URIDINE
  name = G4_DNA_URIDINE
  specific = 4
FEATURE [App::DocumentObjectGroupPython] H_element133  label="H_element : 080"  # scripted group (container) (typed FeaturePython)
  n = 11
  ref = H_element
FEATURE [App::DocumentObjectGroupPython] C_element143  label="C_element : 088"  # scripted group (container) (typed FeaturePython)
  n = 10
  ref = C_element
FEATURE [App::DocumentObjectGroupPython] N_element063  label="N_element : 035"  # scripted group (container) (typed FeaturePython)
  n = 2
  ref = N_element
FEATURE [App::DocumentObjectGroupPython] O_element124  label="O_element : 077"  # scripted group (container) (typed FeaturePython)
  n = 6
  ref = O_element
FEATURE [App::DocumentObjectGroupPython] G4_DNA_METHYLURIDINE  # scripted group (container) (typed FeaturePython)
  Dunit = g/cm3
  Dvalue = 1
  Group = -> [H_element133,C_element143,N_element063,O_element124]
  conduct = 2
  density = 1
  expand = 3
  formula = G4_DNA_METHYLURIDINE
  name = G4_DNA_METHYLURIDINE
  specific = 4
FEATURE [App::DocumentObjectGroupPython] P_element014  label="P_element : 003"  # scripted group (container) (typed FeaturePython)
  n = 1
  ref = P_element
FEATURE [App::DocumentObjectGroupPython] O_element125  label="O_element : 078"  # scripted group (container) (typed FeaturePython)
  n = 3
  ref = O_element
FEATURE [App::DocumentObjectGroupPython] G4_DNA_MONOPHOSPHATE  # scripted group (container) (typed FeaturePython)
  Dunit = g/cm3
  Dvalue = 1
  Group = -> [P_element014,O_element125]
  conduct = 2
  density = 1
  expand = 3
  formula = G4_DNA_MONOPHOSPHATE
  name = G4_DNA_MONOPHOSPHATE
  specific = 4
FEATURE [App::DocumentObjectGroupPython] H_element134  label="H_element : 081"  # scripted group (container) (typed FeaturePython)
  n = 10
  ref = H_element
FEATURE [App::DocumentObjectGroupPython] C_element144  label="C_element : 089"  # scripted group (container) (typed FeaturePython)
  n = 10
  ref = C_element
FEATURE [App::DocumentObjectGroupPython] N_element064  label="N_element : 036"  # scripted group (container) (typed FeaturePython)
  n = 5
  ref = N_element
FEATURE [App::DocumentObjectGroupPython] O_element126  label="O_element : 079"  # scripted group (container) (typed FeaturePython)
  n = 7
  ref = O_element
FEATURE [App::DocumentObjectGroupPython] P_element015  label="P_element : 004"  # scripted group (container) (typed FeaturePython)
  n = 1
  ref = P_element
FEATURE [App::DocumentObjectGroupPython] G4_DNA_A  # scripted group (container) (typed FeaturePython)
  Dunit = g/cm3
  Dvalue = 1
  Group = -> [H_element134,C_element144,N_element064,O_element126,P_element015]
  conduct = 2
  density = 1
  expand = 3
  formula = G4_DNA_A
  name = G4_DNA_A
  specific = 4
FEATURE [App::DocumentObjectGroupPython] H_element135  label="H_element : 082"  # scripted group (container) (typed FeaturePython)
  n = 10
  ref = H_element
FEATURE [App::DocumentObjectGroupPython] C_element145  label="C_element : 090"  # scripted group (container) (typed FeaturePython)
  n = 10
  ref = C_element
FEATURE [App::DocumentObjectGroupPython] N_element065  label="N_element : 037"  # scripted group (container) (typed FeaturePython)
  n = 5
  ref = N_element
FEATURE [App::DocumentObjectGroupPython] O_element127  label="O_element : 8"  # scripted group (container) (typed FeaturePython)
  n = 8
  ref = O_element
FEATURE [App::DocumentObjectGroupPython] P_element016  label="P_element : 005"  # scripted group (container) (typed FeaturePython)
  n = 1
  ref = P_element
FEATURE [App::DocumentObjectGroupPython] G4_DNA_G  # scripted group (container) (typed FeaturePython)
  Dunit = g/cm3
  Dvalue = 1
  Group = -> [H_element135,C_element145,N_element065,O_element127,P_element016]
  conduct = 2
  density = 1
  expand = 3
  formula = G4_DNA_G
  name = G4_DNA_G
  specific = 4
FEATURE [App::DocumentObjectGroupPython] H_element136  label="H_element : 083"  # scripted group (container) (typed FeaturePython)
  n = 10
  ref = H_element
FEATURE [App::DocumentObjectGroupPython] C_element146  label="C_element : 091"  # scripted group (container) (typed FeaturePython)
  n = 9
  ref = C_element
FEATURE [App::DocumentObjectGroupPython] N_element066  label="N_element : 038"  # scripted group (container) (typed FeaturePython)
  n = 3
  ref = N_element
FEATURE [App::DocumentObjectGroupPython] O_element128  label="O_element : 080"  # scripted group (container) (typed FeaturePython)
  n = 8
  ref = O_element
FEATURE [App::DocumentObjectGroupPython] P_element017  label="P_element : 006"  # scripted group (container) (typed FeaturePython)
  n = 1
  ref = P_element
FEATURE [App::DocumentObjectGroupPython] G4_DNA_C  # scripted group (container) (typed FeaturePython)
  Dunit = g/cm3
  Dvalue = 1
  Group = -> [H_element136,C_element146,N_element066,O_element128,P_element017]
  conduct = 2
  density = 1
  expand = 3
  formula = G4_DNA_C
  name = G4_DNA_C
  specific = 4
FEATURE [App::DocumentObjectGroupPython] H_element137  label="H_element : 084"  # scripted group (container) (typed FeaturePython)
  n = 9
  ref = H_element
FEATURE [App::DocumentObjectGroupPython] C_element147  label="C_element : 092"  # scripted group (container) (typed FeaturePython)
  n = 9
  ref = C_element
FEATURE [App::DocumentObjectGroupPython] N_element067  label="N_element : 039"  # scripted group (container) (typed FeaturePython)
  n = 2
  ref = N_element
FEATURE [App::DocumentObjectGroupPython] O_element129  label="O_element : 9"  # scripted group (container) (typed FeaturePython)
  n = 9
  ref = O_element
FEATURE [App::DocumentObjectGroupPython] P_element018  label="P_element : 007"  # scripted group (container) (typed FeaturePython)
  n = 1
  ref = P_element
FEATURE [App::DocumentObjectGroupPython] G4_DNA_U  # scripted group (container) (typed FeaturePython)
  Dunit = g/cm3
  Dvalue = 1
  Group = -> [H_element137,C_element147,N_element067,O_element129,P_element018]
  conduct = 2
  density = 1
  expand = 3
  formula = G4_DNA_U
  name = G4_DNA_U
  specific = 4
FEATURE [App::DocumentObjectGroupPython] H_element138  label="H_element : 085"  # scripted group (container) (typed FeaturePython)
  n = 11
  ref = H_element
FEATURE [App::DocumentObjectGroupPython] C_element148  label="C_element : 093"  # scripted group (container) (typed FeaturePython)
  n = 10
  ref = C_element
FEATURE [App::DocumentObjectGroupPython] N_element068  label="N_element : 040"  # scripted group (container) (typed FeaturePython)
  n = 2
  ref = N_element
FEATURE [App::DocumentObjectGroupPython] O_element130  label="O_element : 081"  # scripted group (container) (typed FeaturePython)
  n = 9
  ref = O_element
FEATURE [App::DocumentObjectGroupPython] P_element019  label="P_element : 008"  # scripted group (container) (typed FeaturePython)
  n = 1
  ref = P_element
FEATURE [App::DocumentObjectGroupPython] G4_DNA_MU  # scripted group (container) (typed FeaturePython)
  Dunit = g/cm3
  Dvalue = 1
  Group = -> [H_element138,C_element148,N_element068,O_element130,P_element019]
  conduct = 2
  density = 1
  expand = 3
  formula = G4_DNA_MU
  name = G4_DNA_MU
  specific = 4
FEATURE [App::DocumentObjectGroupPython] BioChemical  # scripted group (container) (typed FeaturePython)
  Group = -> [G4_CYTOSINE,G4_THYMINE,G4_URACIL,G4_DNA_ADENINE,G4_DNA_GUANINE,G4_DNA_CYTOSINE,G4_DNA_THYMINE,G4_DNA_URACIL,G4_DNA_ADENOSINE,G4_DNA_GUANOSINE,G4_DNA_CYTIDINE,G4_DNA_URIDINE,G4_DNA_METHYLURIDINE,G4_DNA_MONOPHOSPHATE,G4_DNA_A,G4_DNA_G,G4_DNA_C,G4_DNA_U,G4_DNA_MU]
FEATURE [App::DocumentObjectGroupPython] G4Materials  # scripted group (container) (typed FeaturePython)
  Group = -> [NIST,Element,HEP,Space,BioChemical]
  version = 1
FEATURE [App::DocumentObjectGroupPython] Geant4  # scripted group (container) (typed FeaturePython)
  Group = -> [G4Isotopes,G4Elements,G4Materials]
FEATURE [App::DocumentObjectGroupPython] Materials  # scripted group (container) (typed FeaturePython)
  Group = -> [Geant4]
FEATURE [Part::FeaturePython] GDMLBox_WorldBox  # WARN: FeaturePython — macro-defined, semantics opaque (R4)
  lunit = 2
  material = 5
  x = 100
  y = 100
  z = 100
FEATURE [Sketcher::SketchObject] Sketch001
  ArcFitTolerance = 0
  FullyConstrained = false
  MakeInternals = false
  Placement = pos=(0,0,0) rot=(1,0,0;1.5708rad)
  sketch-geometry (5):
    g0: Ellipse CenterX=30.6351 CenterY=6.78706 CenterZ=0 NormalX=0 NormalY=0 NormalZ=1 MajorRadius=17.5631 MinorRadius=6.80538 AngleXU=0.511231
    g1: LineSegment [constr] StartX=45.9527 StartY=15.3798 StartZ=0 EndX=15.3176 EndY=-1.80572 EndZ=0
    g2: LineSegment [constr] StartX=27.3056 StartY=12.7223 StartZ=0 EndX=33.9647 EndY=0.85179 EndZ=0
    g3: GeomPoint [constr] X=44.756 Y=14.7085 Z=0
    g4: GeomPoint [constr] X=16.5142 Y=-1.13443 Z=0
  constraints (1):
    c: InternalAlignment(g1-g4 -> g0) x4
FEATURE [Part::Revolution] Revolve
  Angle = 360
  Axis = (0,0,1)
  Base = (0,0,0)
  FaceMakerClass = Part::FaceMakerBullseye
  Solid = true
  Source = -> Sketch001
  Symmetric = false
  material = 5
FEATURE [App::Part] Part
  Group = -> [Sketch001,Revolve]
  Origin = -> Origin001
FEATURE [App::Part] worldVOL
  Group = -> [GDMLBox_WorldBox,Part]
  Origin = -> Origin
